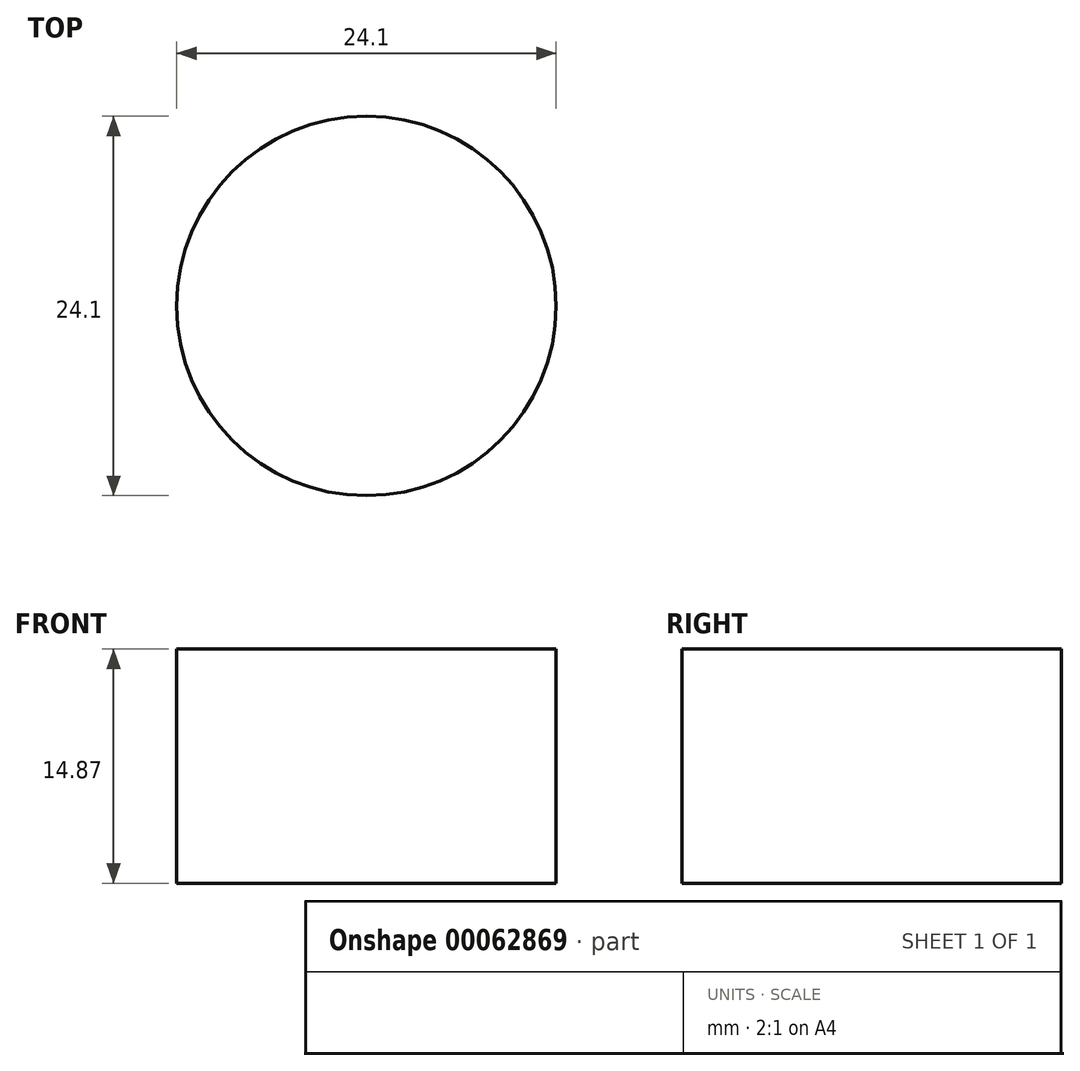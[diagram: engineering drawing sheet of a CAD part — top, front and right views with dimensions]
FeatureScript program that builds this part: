
annotation { "Feature Type Name" : "Feature", "Feature Type Description" : "" }
export const myFeature = defineFeature(function(context is Context, id is Id, definition is map)
    precondition{}
    {
        {
            var Q0;
            Q0=qCreatedBy(makeId("Front.planeOp"),FACE);
            var sketch = newSketch(context, id + "F0", { "sketchPlane" : qUnion([Q0])});
            skLineSegment(sketch, "E0", {"start": v(0, 16.36) * mm, "end": v(0, -28.8) * mm});
            skLineSegment(sketch, "E1", {"start": v(0, 16.36) * mm, "end": v(15.92, 16.36) * mm});
            skLineSegment(sketch, "E2", {"start": v(15.92, 16.36) * mm, "end": v(15.92, -28.8) * mm});
            skLineSegment(sketch, "E3", {"start": v(15.92, -28.8) * mm, "end": v(0, -28.8) * mm});
            skLineSegment(sketch, "E4", {"start": v(0, -28.8) * mm, "end": v(12.05, -28.8) * mm});
            skLineSegment(sketch, "E5", {"start": v(15.92, 16.36) * mm, "end": v(12.05, 16.36) * mm});
            skLineSegment(sketch, "E6", {"start": v(15.92, 16.36) * mm, "end": v(15.92, 12.22) * mm});
            skPoint(sketch, "E7", {"position": v(13.99, 16.36) * mm});
            skPoint(sketch, "E8", {"position": v(15.92, 14.29) * mm});
            skPoint(sketch, "E9", {"position": v(-63.86, 47.5) * mm});
            skLineSegment(sketch, "E10", {"start": v(12.05, 16.36) * mm, "end": v(12.05, -28.8) * mm});
            skLineSegment(sketch, "E11", {"start": v(15.92, -28.8) * mm, "end": v(15.92, -18.05) * mm});
            skLineSegment(sketch, "E12", {"start": v(15.92, -28.8) * mm, "end": v(15.92, -13.8) * mm});
            skLineSegment(sketch, "E13", {"start": v(15.92, -13.8) * mm, "end": v(15.92, -18.55) * mm});
            skLineSegment(sketch, "E14", {"start": v(15.92, -13.8) * mm, "end": v(15.42, -13.8) * mm});
            skLineSegment(sketch, "E15", {"start": v(15.42, -13.8) * mm, "end": v(15.42, -18.55) * mm});
            skLineSegment(sketch, "E16", {"start": v(15.42, -18.55) * mm, "end": v(15.92, -18.55) * mm});
            skLineSegment(sketch, "E17", {"start": v(0, -13.93) * mm, "end": v(8.68, -13.93) * mm});
            skLineSegment(sketch, "E18", {"start": v(8.68, -13.93) * mm, "end": v(12.05, -13.93) * mm});
            skLineSegment(sketch, "E19", {"start": v(8.68, -13.93) * mm, "end": v(8.68, -28.8) * mm});
            skFitSpline(sketch, "E20", {"points": [v(12.05, 16.36) * mm, v(14.39, 15.38) * mm, v(15.92, 12.9) * mm], "startDerivative": vector(3.11, 0) * mm, "endDerivative": vector(0, -5.55) * mm});
            skSolve(sketch);
        }
        {
            var Q0;
            {var subQ0=sQuery(id+"F0.wireOp",EDGE,"d632429b-8b9d-4d76-a169-94f976e06c24");var subQ1=sQuery(id+"F0.wireOp",EDGE,"9AcJyGnw-STYi-GIwg-dRD0-rNDVPBwUBnKr");var subQ2=makeQuery(id+"F0.imprint","INTERSECT",VERTEX,{"disambiguationData":[OD(0.0)],"derivedFrom":[subQ1,subQ0]});Q0=makeQuery(id+"F0.imprint","IMPRINT",FACE,{"disambiguationData":[TD([[makeQuery(id+"F0.imprint","IMPRINT",EDGE,{"disambiguationData":[TD([[subQ2,-1.0]])],"derivedFrom":subQ1}),1.0]])]});}
            var Q1;
            {var subQ1=sQuery(id+"F0.wireOp",EDGE,"E6");var subQ3=sQuery(id+"F0.wireOp",EDGE,"d632429b-8b9d-4d76-a169-94f976e06c24");var subQ4=makeQuery(id+"F0.imprint","INTERSECT",VERTEX,{"derivedFrom":[subQ1,subQ3]});Q1=makeQuery(id+"F0.imprint","IMPRINT",FACE,{"disambiguationData":[TD([[makeQuery(id+"F0.imprint","IMPRINT",EDGE,{"disambiguationData":[TD([[subQ4,1.0]])],"derivedFrom":subQ3}),-1.0]])]});}
            var Q2;
            {var subQ1=sQuery(id+"F0.wireOp",EDGE,"E5");var subQ3=sQuery(id+"F0.wireOp",EDGE,"d632429b-8b9d-4d76-a169-94f976e06c24");var subQ4=makeQuery(id+"F0.imprint","INTERSECT",VERTEX,{"derivedFrom":[subQ1,subQ3]});Q2=makeQuery(id+"F0.imprint","IMPRINT",FACE,{"disambiguationData":[TD([[makeQuery(id+"F0.imprint","IMPRINT",EDGE,{"disambiguationData":[TD([[subQ4,-1.0]])],"derivedFrom":subQ3}),-1.0]])]});}
            var Q3;
            {var subQ1=sQuery(id+"F0.wireOp",EDGE,"9AcJyGnw-STYi-GIwg-dRD0-rNDVPBwUBnKr");var subQ3=sQuery(id+"F0.wireOp",EDGE,"d632429b-8b9d-4d76-a169-94f976e06c24");var subQ4=makeQuery(id+"F0.imprint","INTERSECT",VERTEX,{"disambiguationData":[OD(0.0)],"derivedFrom":[subQ1,subQ3]});Q3=makeQuery(id+"F0.imprint","IMPRINT",FACE,{"disambiguationData":[TD([[makeQuery(id+"F0.imprint","IMPRINT",EDGE,{"disambiguationData":[TD([[subQ4,-1.0]])],"derivedFrom":subQ3}),-1.0]])]});}
            var Q4;
            {var subQ4=sQuery(id+"F0.wireOp",EDGE,"E18");Q4=makeQuery(id+"F0.imprint","IMPRINT",FACE,{"disambiguationData":[TD([[makeQuery(id+"F0.imprint","IMPRINT",EDGE,{"derivedFrom":subQ4}),-1.0]])]});}
            var Q5;
            {var subQ1=sQuery(id+"F0.wireOp",EDGE,"E3");Q5=makeQuery(id+"F0.imprint","IMPRINT",FACE,{"disambiguationData":[TD([[makeQuery(id+"F0.imprint","IMPRINT",EDGE,{"derivedFrom":subQ1}),-1.0]])]});}
            var Q6;
            Q6=sQuery(id+"F0.wireOp",EDGE,"E0");
            revolve(context, id + "F1", {"entities" : qUnion([Q0, Q1, Q2, Q3, Q4, Q5]), "axis" : qUnion([Q6]), "revolveType" : RevolveType.FULL});
        }
        {
            var Q0;
            Q0=qCreatedBy(makeId("Front.planeOp"),FACE);
            var sketch = newSketch(context, id + "F2", { "sketchPlane" : qUnion([Q0])});
            skCircle(sketch, "E21", {"center": v(18.2, -22.31) * mm, "radius": 3 * mm});
            skLineSegment(sketch, "E22", {"start": v(18.2, -22.31) * mm, "end": v(18.2, -40.74) * mm});
            skLineSegment(sketch, "E23", {"start": v(21.2, -22.31) * mm, "end": v(18.2, -22.31) * mm});
            skLineSegment(sketch, "E24", {"start": v(18.2, -40.74) * mm, "end": v(21.2, -40.74) * mm});
            skLineSegment(sketch, "E25", {"start": v(21.2, -22.31) * mm, "end": v(21.2, -40.74) * mm});
            skLineSegment(sketch, "E26", {"start": v(18.2, -22.31) * mm, "end": v(18.2, -19.31) * mm});
            skSolve(sketch);
        }
        {
            var Q0;
            {var subQ0=sQuery(id+"F2.wireOp",EDGE,"E23");Q0=makeQuery(id+"F2.imprint","IMPRINT",FACE,{"disambiguationData":[TD([[makeQuery(id+"F2.imprint","IMPRINT",EDGE,{"derivedFrom":subQ0}),-1.0]])]});}
            var Q1;
            {var subQ0=sQuery(id+"F2.wireOp",EDGE,"E23");Q1=makeQuery(id+"F2.imprint","IMPRINT",FACE,{"disambiguationData":[TD([[makeQuery(id+"F2.imprint","IMPRINT",EDGE,{"derivedFrom":subQ0}),1.0]])]});}
            var Q2;
            {var subQ4=sQuery(id+"F2.wireOp",EDGE,"E24");Q2=makeQuery(id+"F2.imprint","IMPRINT",FACE,{"disambiguationData":[TD([[makeQuery(id+"F2.imprint","IMPRINT",EDGE,{"derivedFrom":subQ4}),1.0]])]});}
            var Q3;
            Q3=sQuery(id+"F2.wireOp",EDGE,"E22");
            revolve(context, id + "F3", {"entities" : qUnion([Q0, Q1, Q2]), "axis" : qUnion([Q3]), "revolveType" : RevolveType.FULL});
        }
        {
            var Q0;
            Q0=qCreatedBy(makeId("Front.planeOp"),FACE);
            var sketch = newSketch(context, id + "F4", { "sketchPlane" : qUnion([Q0])});
            skLineSegment(sketch, "E27.bottom", {"start": v(0, 43.24) * mm, "end": v(-13.77, 43.24) * mm});
            skLineSegment(sketch, "E27.top", {"start": v(0, 31.16) * mm, "end": v(-13.77, 31.16) * mm});
            skLineSegment(sketch, "E27.left", {"start": v(0, 43.24) * mm, "end": v(0, 31.16) * mm});
            skLineSegment(sketch, "E27.right", {"start": v(-13.77, 43.24) * mm, "end": v(-13.77, 31.16) * mm});
            skSolve(sketch);
        }
        {
            var Q0;
            Q0=qSketchRegion(id+"F4",true);
            extrude(context, id + "F5", {"entities" : qUnion([Q0]), "depth" : 25 * mm});
        }
        {
            var Q0;
            Q0=makeQuery(id+"F3.opRevolve","SWEPT_BODY",BODY,{"disambiguationData":[OSD([sQuery(id+"F2.wireOp",EDGE,"E21"),sQuery(id+"F2.wireOp",EDGE,"E22"),sQuery(id+"F2.wireOp",EDGE,"E24"),sQuery(id+"F2.wireOp",EDGE,"E25"),sQuery(id+"F2.wireOp",EDGE,"E26")])]});
            var Q1;
            Q1=makeQuery(id+"F5.opExtrude","CAP_EDGE",EDGE,{"disambiguationData":[OSD([sQuery(id+"F4.wireOp",EDGE,"E27.left")])],"isStart":true});
            transform(context, id + "F6", {"entities" : qUnion([Q0]), "transformType" : TransformType.ROTATION, "transformAxis" : qUnion([Q1]), "angle" : 22.5 * degree, "makeCopy" : true});
        }
        {
            var Q0;
            Q0=makeQuery(id+"F6.opPattern","COPY",BODY,{"derivedFrom":makeQuery(id+"F3.opRevolve","SWEPT_BODY",BODY,{"disambiguationData":[OSD([sQuery(id+"F2.wireOp",EDGE,"E21"),sQuery(id+"F2.wireOp",EDGE,"E22"),sQuery(id+"F2.wireOp",EDGE,"E24"),sQuery(id+"F2.wireOp",EDGE,"E25"),sQuery(id+"F2.wireOp",EDGE,"E26")])]}),"instanceName":"1"});
            var Q1;
            Q1=makeQuery(id+"F3.opRevolve","SWEPT_BODY",BODY,{"disambiguationData":[OSD([sQuery(id+"F2.wireOp",EDGE,"E21"),sQuery(id+"F2.wireOp",EDGE,"E22"),sQuery(id+"F2.wireOp",EDGE,"E24"),sQuery(id+"F2.wireOp",EDGE,"E25"),sQuery(id+"F2.wireOp",EDGE,"E26")])]});
            var Q2;
            Q2=makeQuery(id+"F5.opExtrude","CAP_EDGE",EDGE,{"disambiguationData":[OSD([sQuery(id+"F4.wireOp",EDGE,"E27.left")])],"isStart":true});
            transform(context, id + "F7", {"entities" : qUnion([Q0, Q1]), "transformType" : TransformType.ROTATION, "transformAxis" : qUnion([Q2]), "angle" : 45 * degree, "makeCopy" : true});
        }
        {
            var Q0;
            Q0=makeQuery(id+"F3.opRevolve","SWEPT_BODY",BODY,{"disambiguationData":[OSD([sQuery(id+"F2.wireOp",EDGE,"E21"),sQuery(id+"F2.wireOp",EDGE,"E22"),sQuery(id+"F2.wireOp",EDGE,"E24"),sQuery(id+"F2.wireOp",EDGE,"E25"),sQuery(id+"F2.wireOp",EDGE,"E26")])]});
            var Q1;
            Q1=makeQuery(id+"F6.opPattern","COPY",BODY,{"derivedFrom":makeQuery(id+"F3.opRevolve","SWEPT_BODY",BODY,{"disambiguationData":[OSD([sQuery(id+"F2.wireOp",EDGE,"E21"),sQuery(id+"F2.wireOp",EDGE,"E22"),sQuery(id+"F2.wireOp",EDGE,"E24"),sQuery(id+"F2.wireOp",EDGE,"E25"),sQuery(id+"F2.wireOp",EDGE,"E26")])]}),"instanceName":"1"});
            var Q2;
            Q2=makeQuery(id+"F7.opPattern","COPY",BODY,{"derivedFrom":makeQuery(id+"F3.opRevolve","SWEPT_BODY",BODY,{"disambiguationData":[OSD([sQuery(id+"F2.wireOp",EDGE,"E21"),sQuery(id+"F2.wireOp",EDGE,"E22"),sQuery(id+"F2.wireOp",EDGE,"E24"),sQuery(id+"F2.wireOp",EDGE,"E25"),sQuery(id+"F2.wireOp",EDGE,"E26")])]}),"instanceName":"1"});
            var Q3;
            Q3=makeQuery(id+"F7.opPattern","COPY",BODY,{"derivedFrom":makeQuery(id+"F6.opPattern","COPY",BODY,{"derivedFrom":makeQuery(id+"F3.opRevolve","SWEPT_BODY",BODY,{"disambiguationData":[OSD([sQuery(id+"F2.wireOp",EDGE,"E21"),sQuery(id+"F2.wireOp",EDGE,"E22"),sQuery(id+"F2.wireOp",EDGE,"E24"),sQuery(id+"F2.wireOp",EDGE,"E25"),sQuery(id+"F2.wireOp",EDGE,"E26")])]}),"instanceName":"1"}),"instanceName":"1"});
            var Q4;
            Q4=makeQuery(id+"F5.opExtrude","CAP_EDGE",EDGE,{"disambiguationData":[OSD([sQuery(id+"F4.wireOp",EDGE,"E27.left")])],"isStart":true});
            transform(context, id + "F8", {"entities" : qUnion([Q0, Q1, Q2, Q3]), "transformType" : TransformType.ROTATION, "transformAxis" : qUnion([Q4]), "angle" : 90 * degree, "makeCopy" : true});
        }
        {
            var Q0;
            Q0=makeQuery(id+"F3.opRevolve","SWEPT_BODY",BODY,{"disambiguationData":[OSD([sQuery(id+"F2.wireOp",EDGE,"E21"),sQuery(id+"F2.wireOp",EDGE,"E22"),sQuery(id+"F2.wireOp",EDGE,"E24"),sQuery(id+"F2.wireOp",EDGE,"E25"),sQuery(id+"F2.wireOp",EDGE,"E26")])]});
            var Q1;
            Q1=makeQuery(id+"F6.opPattern","COPY",BODY,{"derivedFrom":makeQuery(id+"F3.opRevolve","SWEPT_BODY",BODY,{"disambiguationData":[OSD([sQuery(id+"F2.wireOp",EDGE,"E21"),sQuery(id+"F2.wireOp",EDGE,"E22"),sQuery(id+"F2.wireOp",EDGE,"E24"),sQuery(id+"F2.wireOp",EDGE,"E25"),sQuery(id+"F2.wireOp",EDGE,"E26")])]}),"instanceName":"1"});
            var Q2;
            Q2=makeQuery(id+"F7.opPattern","COPY",BODY,{"derivedFrom":makeQuery(id+"F3.opRevolve","SWEPT_BODY",BODY,{"disambiguationData":[OSD([sQuery(id+"F2.wireOp",EDGE,"E21"),sQuery(id+"F2.wireOp",EDGE,"E22"),sQuery(id+"F2.wireOp",EDGE,"E24"),sQuery(id+"F2.wireOp",EDGE,"E25"),sQuery(id+"F2.wireOp",EDGE,"E26")])]}),"instanceName":"1"});
            var Q3;
            Q3=makeQuery(id+"F7.opPattern","COPY",BODY,{"derivedFrom":makeQuery(id+"F6.opPattern","COPY",BODY,{"derivedFrom":makeQuery(id+"F3.opRevolve","SWEPT_BODY",BODY,{"disambiguationData":[OSD([sQuery(id+"F2.wireOp",EDGE,"E21"),sQuery(id+"F2.wireOp",EDGE,"E22"),sQuery(id+"F2.wireOp",EDGE,"E24"),sQuery(id+"F2.wireOp",EDGE,"E25"),sQuery(id+"F2.wireOp",EDGE,"E26")])]}),"instanceName":"1"}),"instanceName":"1"});
            var Q4;
            Q4=makeQuery(id+"F8.opPattern","COPY",BODY,{"derivedFrom":makeQuery(id+"F3.opRevolve","SWEPT_BODY",BODY,{"disambiguationData":[OSD([sQuery(id+"F2.wireOp",EDGE,"E21"),sQuery(id+"F2.wireOp",EDGE,"E22"),sQuery(id+"F2.wireOp",EDGE,"E24"),sQuery(id+"F2.wireOp",EDGE,"E25"),sQuery(id+"F2.wireOp",EDGE,"E26")])]}),"instanceName":"1"});
            var Q5;
            Q5=makeQuery(id+"F8.opPattern","COPY",BODY,{"derivedFrom":makeQuery(id+"F6.opPattern","COPY",BODY,{"derivedFrom":makeQuery(id+"F3.opRevolve","SWEPT_BODY",BODY,{"disambiguationData":[OSD([sQuery(id+"F2.wireOp",EDGE,"E21"),sQuery(id+"F2.wireOp",EDGE,"E22"),sQuery(id+"F2.wireOp",EDGE,"E24"),sQuery(id+"F2.wireOp",EDGE,"E25"),sQuery(id+"F2.wireOp",EDGE,"E26")])]}),"instanceName":"1"}),"instanceName":"1"});
            var Q6;
            Q6=makeQuery(id+"F8.opPattern","COPY",BODY,{"derivedFrom":makeQuery(id+"F7.opPattern","COPY",BODY,{"derivedFrom":makeQuery(id+"F3.opRevolve","SWEPT_BODY",BODY,{"disambiguationData":[OSD([sQuery(id+"F2.wireOp",EDGE,"E21"),sQuery(id+"F2.wireOp",EDGE,"E22"),sQuery(id+"F2.wireOp",EDGE,"E24"),sQuery(id+"F2.wireOp",EDGE,"E25"),sQuery(id+"F2.wireOp",EDGE,"E26")])]}),"instanceName":"1"}),"instanceName":"1"});
            var Q7;
            Q7=makeQuery(id+"F8.opPattern","COPY",BODY,{"derivedFrom":makeQuery(id+"F7.opPattern","COPY",BODY,{"derivedFrom":makeQuery(id+"F6.opPattern","COPY",BODY,{"derivedFrom":makeQuery(id+"F3.opRevolve","SWEPT_BODY",BODY,{"disambiguationData":[OSD([sQuery(id+"F2.wireOp",EDGE,"E21"),sQuery(id+"F2.wireOp",EDGE,"E22"),sQuery(id+"F2.wireOp",EDGE,"E24"),sQuery(id+"F2.wireOp",EDGE,"E25"),sQuery(id+"F2.wireOp",EDGE,"E26")])]}),"instanceName":"1"}),"instanceName":"1"}),"instanceName":"1"});
            var Q8;
            Q8=makeQuery(id+"F5.opExtrude","CAP_EDGE",EDGE,{"disambiguationData":[OSD([sQuery(id+"F4.wireOp",EDGE,"E27.left")])],"isStart":true});
            transform(context, id + "F9", {"entities" : qUnion([Q0, Q1, Q2, Q3, Q4, Q5, Q6, Q7]), "transformType" : TransformType.ROTATION, "transformAxis" : qUnion([Q8]), "angle" : 180 * degree, "makeCopy" : true});
        }
        {
            var Q0;
            Q0=makeQuery(id+"F8.opPattern","COPY",BODY,{"derivedFrom":makeQuery(id+"F7.opPattern","COPY",BODY,{"derivedFrom":makeQuery(id+"F6.opPattern","COPY",BODY,{"derivedFrom":makeQuery(id+"F3.opRevolve","SWEPT_BODY",BODY,{"disambiguationData":[OSD([sQuery(id+"F2.wireOp",EDGE,"E21"),sQuery(id+"F2.wireOp",EDGE,"E22"),sQuery(id+"F2.wireOp",EDGE,"E24"),sQuery(id+"F2.wireOp",EDGE,"E25"),sQuery(id+"F2.wireOp",EDGE,"E26")])]}),"instanceName":"1"}),"instanceName":"1"}),"instanceName":"1"});
            var Q1;
            Q1=makeQuery(id+"F9.opPattern","COPY",BODY,{"derivedFrom":makeQuery(id+"F3.opRevolve","SWEPT_BODY",BODY,{"disambiguationData":[OSD([sQuery(id+"F2.wireOp",EDGE,"E21"),sQuery(id+"F2.wireOp",EDGE,"E22"),sQuery(id+"F2.wireOp",EDGE,"E24"),sQuery(id+"F2.wireOp",EDGE,"E25"),sQuery(id+"F2.wireOp",EDGE,"E26")])]}),"instanceName":"1"});
            var Q2;
            Q2=makeQuery(id+"F9.opPattern","COPY",BODY,{"derivedFrom":makeQuery(id+"F6.opPattern","COPY",BODY,{"derivedFrom":makeQuery(id+"F3.opRevolve","SWEPT_BODY",BODY,{"disambiguationData":[OSD([sQuery(id+"F2.wireOp",EDGE,"E21"),sQuery(id+"F2.wireOp",EDGE,"E22"),sQuery(id+"F2.wireOp",EDGE,"E24"),sQuery(id+"F2.wireOp",EDGE,"E25"),sQuery(id+"F2.wireOp",EDGE,"E26")])]}),"instanceName":"1"}),"instanceName":"1"});
            var Q3;
            Q3=makeQuery(id+"F8.opPattern","COPY",BODY,{"derivedFrom":makeQuery(id+"F6.opPattern","COPY",BODY,{"derivedFrom":makeQuery(id+"F3.opRevolve","SWEPT_BODY",BODY,{"disambiguationData":[OSD([sQuery(id+"F2.wireOp",EDGE,"E21"),sQuery(id+"F2.wireOp",EDGE,"E22"),sQuery(id+"F2.wireOp",EDGE,"E24"),sQuery(id+"F2.wireOp",EDGE,"E25"),sQuery(id+"F2.wireOp",EDGE,"E26")])]}),"instanceName":"1"}),"instanceName":"1"});
            var Q4;
            Q4=makeQuery(id+"F8.opPattern","COPY",BODY,{"derivedFrom":makeQuery(id+"F7.opPattern","COPY",BODY,{"derivedFrom":makeQuery(id+"F3.opRevolve","SWEPT_BODY",BODY,{"disambiguationData":[OSD([sQuery(id+"F2.wireOp",EDGE,"E21"),sQuery(id+"F2.wireOp",EDGE,"E22"),sQuery(id+"F2.wireOp",EDGE,"E24"),sQuery(id+"F2.wireOp",EDGE,"E25"),sQuery(id+"F2.wireOp",EDGE,"E26")])]}),"instanceName":"1"}),"instanceName":"1"});
            var Q5;
            Q5=makeQuery(id+"F8.opPattern","COPY",BODY,{"derivedFrom":makeQuery(id+"F3.opRevolve","SWEPT_BODY",BODY,{"disambiguationData":[OSD([sQuery(id+"F2.wireOp",EDGE,"E21"),sQuery(id+"F2.wireOp",EDGE,"E22"),sQuery(id+"F2.wireOp",EDGE,"E24"),sQuery(id+"F2.wireOp",EDGE,"E25"),sQuery(id+"F2.wireOp",EDGE,"E26")])]}),"instanceName":"1"});
            var Q6;
            Q6=makeQuery(id+"F7.opPattern","COPY",BODY,{"derivedFrom":makeQuery(id+"F6.opPattern","COPY",BODY,{"derivedFrom":makeQuery(id+"F3.opRevolve","SWEPT_BODY",BODY,{"disambiguationData":[OSD([sQuery(id+"F2.wireOp",EDGE,"E21"),sQuery(id+"F2.wireOp",EDGE,"E22"),sQuery(id+"F2.wireOp",EDGE,"E24"),sQuery(id+"F2.wireOp",EDGE,"E25"),sQuery(id+"F2.wireOp",EDGE,"E26")])]}),"instanceName":"1"}),"instanceName":"1"});
            var Q7;
            Q7=makeQuery(id+"F7.opPattern","COPY",BODY,{"derivedFrom":makeQuery(id+"F3.opRevolve","SWEPT_BODY",BODY,{"disambiguationData":[OSD([sQuery(id+"F2.wireOp",EDGE,"E21"),sQuery(id+"F2.wireOp",EDGE,"E22"),sQuery(id+"F2.wireOp",EDGE,"E24"),sQuery(id+"F2.wireOp",EDGE,"E25"),sQuery(id+"F2.wireOp",EDGE,"E26")])]}),"instanceName":"1"});
            var Q8;
            Q8=makeQuery(id+"F6.opPattern","COPY",BODY,{"derivedFrom":makeQuery(id+"F3.opRevolve","SWEPT_BODY",BODY,{"disambiguationData":[OSD([sQuery(id+"F2.wireOp",EDGE,"E21"),sQuery(id+"F2.wireOp",EDGE,"E22"),sQuery(id+"F2.wireOp",EDGE,"E24"),sQuery(id+"F2.wireOp",EDGE,"E25"),sQuery(id+"F2.wireOp",EDGE,"E26")])]}),"instanceName":"1"});
            var Q9;
            Q9=makeQuery(id+"F3.opRevolve","SWEPT_BODY",BODY,{"disambiguationData":[OSD([sQuery(id+"F2.wireOp",EDGE,"E21"),sQuery(id+"F2.wireOp",EDGE,"E22"),sQuery(id+"F2.wireOp",EDGE,"E24"),sQuery(id+"F2.wireOp",EDGE,"E25"),sQuery(id+"F2.wireOp",EDGE,"E26")])]});
            var Q10;
            Q10=makeQuery(id+"F9.opPattern","COPY",BODY,{"derivedFrom":makeQuery(id+"F8.opPattern","COPY",BODY,{"derivedFrom":makeQuery(id+"F7.opPattern","COPY",BODY,{"derivedFrom":makeQuery(id+"F6.opPattern","COPY",BODY,{"derivedFrom":makeQuery(id+"F3.opRevolve","SWEPT_BODY",BODY,{"disambiguationData":[OSD([sQuery(id+"F2.wireOp",EDGE,"E21"),sQuery(id+"F2.wireOp",EDGE,"E22"),sQuery(id+"F2.wireOp",EDGE,"E24"),sQuery(id+"F2.wireOp",EDGE,"E25"),sQuery(id+"F2.wireOp",EDGE,"E26")])]}),"instanceName":"1"}),"instanceName":"1"}),"instanceName":"1"}),"instanceName":"1"});
            var Q11;
            Q11=makeQuery(id+"F9.opPattern","COPY",BODY,{"derivedFrom":makeQuery(id+"F8.opPattern","COPY",BODY,{"derivedFrom":makeQuery(id+"F7.opPattern","COPY",BODY,{"derivedFrom":makeQuery(id+"F3.opRevolve","SWEPT_BODY",BODY,{"disambiguationData":[OSD([sQuery(id+"F2.wireOp",EDGE,"E21"),sQuery(id+"F2.wireOp",EDGE,"E22"),sQuery(id+"F2.wireOp",EDGE,"E24"),sQuery(id+"F2.wireOp",EDGE,"E25"),sQuery(id+"F2.wireOp",EDGE,"E26")])]}),"instanceName":"1"}),"instanceName":"1"}),"instanceName":"1"});
            var Q12;
            Q12=makeQuery(id+"F9.opPattern","COPY",BODY,{"derivedFrom":makeQuery(id+"F8.opPattern","COPY",BODY,{"derivedFrom":makeQuery(id+"F6.opPattern","COPY",BODY,{"derivedFrom":makeQuery(id+"F3.opRevolve","SWEPT_BODY",BODY,{"disambiguationData":[OSD([sQuery(id+"F2.wireOp",EDGE,"E21"),sQuery(id+"F2.wireOp",EDGE,"E22"),sQuery(id+"F2.wireOp",EDGE,"E24"),sQuery(id+"F2.wireOp",EDGE,"E25"),sQuery(id+"F2.wireOp",EDGE,"E26")])]}),"instanceName":"1"}),"instanceName":"1"}),"instanceName":"1"});
            var Q13;
            Q13=makeQuery(id+"F9.opPattern","COPY",BODY,{"derivedFrom":makeQuery(id+"F8.opPattern","COPY",BODY,{"derivedFrom":makeQuery(id+"F3.opRevolve","SWEPT_BODY",BODY,{"disambiguationData":[OSD([sQuery(id+"F2.wireOp",EDGE,"E21"),sQuery(id+"F2.wireOp",EDGE,"E22"),sQuery(id+"F2.wireOp",EDGE,"E24"),sQuery(id+"F2.wireOp",EDGE,"E25"),sQuery(id+"F2.wireOp",EDGE,"E26")])]}),"instanceName":"1"}),"instanceName":"1"});
            var Q14;
            Q14=makeQuery(id+"F9.opPattern","COPY",BODY,{"derivedFrom":makeQuery(id+"F7.opPattern","COPY",BODY,{"derivedFrom":makeQuery(id+"F6.opPattern","COPY",BODY,{"derivedFrom":makeQuery(id+"F3.opRevolve","SWEPT_BODY",BODY,{"disambiguationData":[OSD([sQuery(id+"F2.wireOp",EDGE,"E21"),sQuery(id+"F2.wireOp",EDGE,"E22"),sQuery(id+"F2.wireOp",EDGE,"E24"),sQuery(id+"F2.wireOp",EDGE,"E25"),sQuery(id+"F2.wireOp",EDGE,"E26")])]}),"instanceName":"1"}),"instanceName":"1"}),"instanceName":"1"});
            var Q15;
            Q15=makeQuery(id+"F9.opPattern","COPY",BODY,{"derivedFrom":makeQuery(id+"F7.opPattern","COPY",BODY,{"derivedFrom":makeQuery(id+"F3.opRevolve","SWEPT_BODY",BODY,{"disambiguationData":[OSD([sQuery(id+"F2.wireOp",EDGE,"E21"),sQuery(id+"F2.wireOp",EDGE,"E22"),sQuery(id+"F2.wireOp",EDGE,"E24"),sQuery(id+"F2.wireOp",EDGE,"E25"),sQuery(id+"F2.wireOp",EDGE,"E26")])]}),"instanceName":"1"}),"instanceName":"1"});
            var Q16;
            Q16=makeQuery(id+"F1.opRevolve","SWEPT_BODY",BODY,{"disambiguationData":[OSD([sQuery(id+"F0.wireOp",EDGE,"E2"),sQuery(id+"F0.wireOp",EDGE,"E3"),sQuery(id+"F0.wireOp",EDGE,"E5"),sQuery(id+"F0.wireOp",EDGE,"E6"),sQuery(id+"F0.wireOp",EDGE,"d632429b-8b9d-4d76-a169-94f976e06c24"),sQuery(id+"F0.wireOp",EDGE,"E10"),sQuery(id+"F0.wireOp",EDGE,"E11"),sQuery(id+"F0.wireOp",EDGE,"mPbeVBwt-LSE7-foui-vcjy-5yCH7zzkyHPw"),sQuery(id+"F0.wireOp",EDGE,"A7bMU6j7-EvYy-TxjT-9eZQ-hZ58iMjyQqAi"),sQuery(id+"F0.wireOp",EDGE,"rTNWqyM8-7bZb-OHbZ-suaX-VuzeamaOtf12")])]});
            booleanBodies(context, id + "F10", {"operationType" : BooleanOperationType.SUBTRACTION, "tools" : qUnion([Q0, Q1, Q2, Q3, Q4, Q5, Q6, Q7, Q8, Q9, Q10, Q11, Q12, Q13, Q14, Q15]), "targets" : qUnion([Q16])});
        }
        {
            var Q0;
            Q0=qCreatedBy(makeId("Front.planeOp"),FACE);
            var sketch = newSketch(context, id + "F11", { "sketchPlane" : qUnion([Q0])});
            skLineSegment(sketch, "E28", {"start": v(0, 31.16) * mm, "end": v(0, -45.64) * mm});
            skCircle(sketch, "E29", {"center": v(0, 5.07) * mm, "radius": 2.11 * mm});
            skSolve(sketch);
        }
        {
            var Q0;
            {var subQ0=sQuery(id+"F11.wireOp",EDGE,"E29");var subQ1=sQuery(id+"F11.wireOp",EDGE,"E28");var subQ2=makeQuery(id+"F11.imprint","INTERSECT",VERTEX,{"disambiguationData":[OD(0.0)],"derivedFrom":[subQ1,subQ0]});Q0=makeQuery(id+"F11.imprint","IMPRINT",FACE,{"disambiguationData":[TD([[makeQuery(id+"F11.imprint","IMPRINT",EDGE,{"disambiguationData":[TD([[subQ2,1.0]])],"derivedFrom":subQ1}),1.0]])]});}
            var Q1;
            {var subQ0=sQuery(id+"F11.wireOp",EDGE,"E29");var subQ1=sQuery(id+"F11.wireOp",EDGE,"E28");var subQ2=makeQuery(id+"F11.imprint","INTERSECT",VERTEX,{"disambiguationData":[OD(0.0)],"derivedFrom":[subQ1,subQ0]});Q1=makeQuery(id+"F11.imprint","IMPRINT",FACE,{"disambiguationData":[TD([[makeQuery(id+"F11.imprint","IMPRINT",EDGE,{"disambiguationData":[TD([[subQ2,1.0]])],"derivedFrom":subQ1}),-1.0]])]});}
            extrude(context, id + "F12", {"entities" : qUnion([Q0, Q1]), "operationType" : NewBodyOperationType.REMOVE, "endBound" : BoundingType.SYMMETRIC, "oppositeDirection" : true, "depth" : 45 * mm});
        }
        {
            var Q0;
            Q0=qCreatedBy(makeId("Top.planeOp"),FACE);
            var sketch = newSketch(context, id + "F13", { "sketchPlane" : qUnion([Q0])});
            skCircle(sketch, "E30", {"center": v(0, 0) * mm, "radius": 15.72 * mm});
            skLineSegment(sketch, "E31.rect.bottom", {"start": v(0.25, 15.97) * mm, "end": v(-0.25, 15.97) * mm});
            skLineSegment(sketch, "E31.rect.top", {"start": v(0.25, 15.47) * mm, "end": v(-0.25, 15.47) * mm});
            skLineSegment(sketch, "E31.rect.left", {"start": v(0.25, 15.97) * mm, "end": v(0.25, 15.47) * mm});
            skLineSegment(sketch, "E31.rect.right", {"start": v(-0.25, 15.97) * mm, "end": v(-0.25, 15.47) * mm});
            skPoint(sketch, "E31.rect.middle", {"position": v(0, 15.72) * mm});
            skSolve(sketch);
        }
        {
            var Q0;
            {var subQ5=sQuery(id+"F13.wireOp",EDGE,"E31.rect.bottom");Q0=makeQuery(id+"F13.imprint","IMPRINT",FACE,{"disambiguationData":[TD([[makeQuery(id+"F13.imprint","IMPRINT",EDGE,{"derivedFrom":subQ5}),1.0]])]});}
            var Q1;
            {var subQ5=sQuery(id+"F13.wireOp",EDGE,"E31.rect.top");Q1=makeQuery(id+"F13.imprint","IMPRINT",FACE,{"disambiguationData":[TD([[makeQuery(id+"F13.imprint","IMPRINT",EDGE,{"derivedFrom":subQ5}),-1.0]])]});}
            extrude(context, id + "F14", {"entities" : qUnion([Q0, Q1]), "depth" : 26.8 * mm});
        }
        {
            var Q0;
            Q0=makeQuery(id+"F14.opExtrude","SWEPT_BODY",BODY,{"disambiguationData":[OSD([sQuery(id+"F13.wireOp",EDGE,"E31.rect.bottom"),sQuery(id+"F13.wireOp",EDGE,"E31.rect.top"),sQuery(id+"F13.wireOp",EDGE,"E31.rect.left"),sQuery(id+"F13.wireOp",EDGE,"E31.rect.right")])]});
            transform(context, id + "F15", {"entities" : qUnion([Q0]), "transformType" : TransformType.TRANSLATION_3D, "dx" : 0 * mm, "dy" : 0 * mm, "dz" : -13.9 * mm, "makeCopy" : false});
        }
        {
            var Q0;
            Q0=makeQuery(id+"F14.opExtrude","SWEPT_BODY",BODY,{"disambiguationData":[OSD([sQuery(id+"F13.wireOp",EDGE,"E31.rect.bottom"),sQuery(id+"F13.wireOp",EDGE,"E31.rect.top"),sQuery(id+"F13.wireOp",EDGE,"E31.rect.left"),sQuery(id+"F13.wireOp",EDGE,"E31.rect.right")])]});
            var Q1;
            Q1=makeQuery(id+"F5.opExtrude","CAP_EDGE",EDGE,{"disambiguationData":[OSD([sQuery(id+"F4.wireOp",EDGE,"E27.left")])],"isStart":true});
            transform(context, id + "F16", {"entities" : qUnion([Q0]), "transformType" : TransformType.ROTATION, "transformAxis" : qUnion([Q1]), "angle" : 3.6 * degree, "makeCopy" : true});
        }
        {
            var Q0;
            Q0=makeQuery(id+"F16.opPattern","COPY",BODY,{"derivedFrom":makeQuery(id+"F14.opExtrude","SWEPT_BODY",BODY,{"disambiguationData":[OSD([sQuery(id+"F13.wireOp",EDGE,"E31.rect.bottom"),sQuery(id+"F13.wireOp",EDGE,"E31.rect.top"),sQuery(id+"F13.wireOp",EDGE,"E31.rect.left"),sQuery(id+"F13.wireOp",EDGE,"E31.rect.right")])]}),"instanceName":"1"});
            var Q1;
            Q1=makeQuery(id+"F14.opExtrude","SWEPT_BODY",BODY,{"disambiguationData":[OSD([sQuery(id+"F13.wireOp",EDGE,"E31.rect.bottom"),sQuery(id+"F13.wireOp",EDGE,"E31.rect.top"),sQuery(id+"F13.wireOp",EDGE,"E31.rect.left"),sQuery(id+"F13.wireOp",EDGE,"E31.rect.right")])]});
            var Q2;
            Q2=makeQuery(id+"F5.opExtrude","CAP_EDGE",EDGE,{"disambiguationData":[OSD([sQuery(id+"F4.wireOp",EDGE,"E27.left")])],"isStart":true});
            transform(context, id + "F17", {"entities" : qUnion([Q0, Q1]), "transformType" : TransformType.ROTATION, "transformAxis" : qUnion([Q2]), "angle" : 7.2 * degree, "makeCopy" : true});
        }
        {
            var Q0;
            Q0=makeQuery(id+"F17.opPattern","COPY",BODY,{"derivedFrom":makeQuery(id+"F16.opPattern","COPY",BODY,{"derivedFrom":makeQuery(id+"F14.opExtrude","SWEPT_BODY",BODY,{"disambiguationData":[OSD([sQuery(id+"F13.wireOp",EDGE,"E31.rect.bottom"),sQuery(id+"F13.wireOp",EDGE,"E31.rect.top"),sQuery(id+"F13.wireOp",EDGE,"E31.rect.left"),sQuery(id+"F13.wireOp",EDGE,"E31.rect.right")])]}),"instanceName":"1"}),"instanceName":"1"});
            var Q1;
            Q1=makeQuery(id+"F17.opPattern","COPY",BODY,{"derivedFrom":makeQuery(id+"F14.opExtrude","SWEPT_BODY",BODY,{"disambiguationData":[OSD([sQuery(id+"F13.wireOp",EDGE,"E31.rect.bottom"),sQuery(id+"F13.wireOp",EDGE,"E31.rect.top"),sQuery(id+"F13.wireOp",EDGE,"E31.rect.left"),sQuery(id+"F13.wireOp",EDGE,"E31.rect.right")])]}),"instanceName":"1"});
            var Q2;
            Q2=makeQuery(id+"F16.opPattern","COPY",BODY,{"derivedFrom":makeQuery(id+"F14.opExtrude","SWEPT_BODY",BODY,{"disambiguationData":[OSD([sQuery(id+"F13.wireOp",EDGE,"E31.rect.bottom"),sQuery(id+"F13.wireOp",EDGE,"E31.rect.top"),sQuery(id+"F13.wireOp",EDGE,"E31.rect.left"),sQuery(id+"F13.wireOp",EDGE,"E31.rect.right")])]}),"instanceName":"1"});
            var Q3;
            Q3=makeQuery(id+"F14.opExtrude","SWEPT_BODY",BODY,{"disambiguationData":[OSD([sQuery(id+"F13.wireOp",EDGE,"E31.rect.bottom"),sQuery(id+"F13.wireOp",EDGE,"E31.rect.top"),sQuery(id+"F13.wireOp",EDGE,"E31.rect.left"),sQuery(id+"F13.wireOp",EDGE,"E31.rect.right")])]});
            var Q4;
            Q4=makeQuery(id+"F5.opExtrude","CAP_EDGE",EDGE,{"disambiguationData":[OSD([sQuery(id+"F4.wireOp",EDGE,"E27.left")])],"isStart":true});
            transform(context, id + "F18", {"entities" : qUnion([Q0, Q1, Q2, Q3]), "transformType" : TransformType.ROTATION, "transformAxis" : qUnion([Q4]), "angle" : 14.4 * degree, "makeCopy" : true});
        }
        {
            var Q0;
            Q0=makeQuery(id+"F18.opPattern","COPY",BODY,{"derivedFrom":makeQuery(id+"F17.opPattern","COPY",BODY,{"derivedFrom":makeQuery(id+"F16.opPattern","COPY",BODY,{"derivedFrom":makeQuery(id+"F14.opExtrude","SWEPT_BODY",BODY,{"disambiguationData":[OSD([sQuery(id+"F13.wireOp",EDGE,"E31.rect.bottom"),sQuery(id+"F13.wireOp",EDGE,"E31.rect.top"),sQuery(id+"F13.wireOp",EDGE,"E31.rect.left"),sQuery(id+"F13.wireOp",EDGE,"E31.rect.right")])]}),"instanceName":"1"}),"instanceName":"1"}),"instanceName":"1"});
            var Q1;
            Q1=makeQuery(id+"F18.opPattern","COPY",BODY,{"derivedFrom":makeQuery(id+"F17.opPattern","COPY",BODY,{"derivedFrom":makeQuery(id+"F14.opExtrude","SWEPT_BODY",BODY,{"disambiguationData":[OSD([sQuery(id+"F13.wireOp",EDGE,"E31.rect.bottom"),sQuery(id+"F13.wireOp",EDGE,"E31.rect.top"),sQuery(id+"F13.wireOp",EDGE,"E31.rect.left"),sQuery(id+"F13.wireOp",EDGE,"E31.rect.right")])]}),"instanceName":"1"}),"instanceName":"1"});
            var Q2;
            Q2=makeQuery(id+"F18.opPattern","COPY",BODY,{"derivedFrom":makeQuery(id+"F16.opPattern","COPY",BODY,{"derivedFrom":makeQuery(id+"F14.opExtrude","SWEPT_BODY",BODY,{"disambiguationData":[OSD([sQuery(id+"F13.wireOp",EDGE,"E31.rect.bottom"),sQuery(id+"F13.wireOp",EDGE,"E31.rect.top"),sQuery(id+"F13.wireOp",EDGE,"E31.rect.left"),sQuery(id+"F13.wireOp",EDGE,"E31.rect.right")])]}),"instanceName":"1"}),"instanceName":"1"});
            var Q3;
            Q3=makeQuery(id+"F18.opPattern","COPY",BODY,{"derivedFrom":makeQuery(id+"F14.opExtrude","SWEPT_BODY",BODY,{"disambiguationData":[OSD([sQuery(id+"F13.wireOp",EDGE,"E31.rect.bottom"),sQuery(id+"F13.wireOp",EDGE,"E31.rect.top"),sQuery(id+"F13.wireOp",EDGE,"E31.rect.left"),sQuery(id+"F13.wireOp",EDGE,"E31.rect.right")])]}),"instanceName":"1"});
            var Q4;
            Q4=makeQuery(id+"F17.opPattern","COPY",BODY,{"derivedFrom":makeQuery(id+"F16.opPattern","COPY",BODY,{"derivedFrom":makeQuery(id+"F14.opExtrude","SWEPT_BODY",BODY,{"disambiguationData":[OSD([sQuery(id+"F13.wireOp",EDGE,"E31.rect.bottom"),sQuery(id+"F13.wireOp",EDGE,"E31.rect.top"),sQuery(id+"F13.wireOp",EDGE,"E31.rect.left"),sQuery(id+"F13.wireOp",EDGE,"E31.rect.right")])]}),"instanceName":"1"}),"instanceName":"1"});
            var Q5;
            Q5=makeQuery(id+"F17.opPattern","COPY",BODY,{"derivedFrom":makeQuery(id+"F14.opExtrude","SWEPT_BODY",BODY,{"disambiguationData":[OSD([sQuery(id+"F13.wireOp",EDGE,"E31.rect.bottom"),sQuery(id+"F13.wireOp",EDGE,"E31.rect.top"),sQuery(id+"F13.wireOp",EDGE,"E31.rect.left"),sQuery(id+"F13.wireOp",EDGE,"E31.rect.right")])]}),"instanceName":"1"});
            var Q6;
            Q6=makeQuery(id+"F16.opPattern","COPY",BODY,{"derivedFrom":makeQuery(id+"F14.opExtrude","SWEPT_BODY",BODY,{"disambiguationData":[OSD([sQuery(id+"F13.wireOp",EDGE,"E31.rect.bottom"),sQuery(id+"F13.wireOp",EDGE,"E31.rect.top"),sQuery(id+"F13.wireOp",EDGE,"E31.rect.left"),sQuery(id+"F13.wireOp",EDGE,"E31.rect.right")])]}),"instanceName":"1"});
            var Q7;
            Q7=makeQuery(id+"F14.opExtrude","SWEPT_BODY",BODY,{"disambiguationData":[OSD([sQuery(id+"F13.wireOp",EDGE,"E31.rect.bottom"),sQuery(id+"F13.wireOp",EDGE,"E31.rect.top"),sQuery(id+"F13.wireOp",EDGE,"E31.rect.left"),sQuery(id+"F13.wireOp",EDGE,"E31.rect.right")])]});
            var Q8;
            Q8=makeQuery(id+"F5.opExtrude","CAP_EDGE",EDGE,{"disambiguationData":[OSD([sQuery(id+"F4.wireOp",EDGE,"E27.left")])],"isStart":true});
            transform(context, id + "F19", {"entities" : qUnion([Q0, Q1, Q2, Q3, Q4, Q5, Q6, Q7]), "transformType" : TransformType.ROTATION, "transformAxis" : qUnion([Q8]), "angle" : 28.8 * degree, "makeCopy" : true});
        }
        {
            var Q0;
            Q0=makeQuery(id+"F14.opExtrude","SWEPT_BODY",BODY,{"disambiguationData":[OSD([sQuery(id+"F13.wireOp",EDGE,"E31.rect.bottom"),sQuery(id+"F13.wireOp",EDGE,"E31.rect.top"),sQuery(id+"F13.wireOp",EDGE,"E31.rect.left"),sQuery(id+"F13.wireOp",EDGE,"E31.rect.right")])]});
            var Q1;
            Q1=makeQuery(id+"F16.opPattern","COPY",BODY,{"derivedFrom":makeQuery(id+"F14.opExtrude","SWEPT_BODY",BODY,{"disambiguationData":[OSD([sQuery(id+"F13.wireOp",EDGE,"E31.rect.bottom"),sQuery(id+"F13.wireOp",EDGE,"E31.rect.top"),sQuery(id+"F13.wireOp",EDGE,"E31.rect.left"),sQuery(id+"F13.wireOp",EDGE,"E31.rect.right")])]}),"instanceName":"1"});
            var Q2;
            Q2=makeQuery(id+"F17.opPattern","COPY",BODY,{"derivedFrom":makeQuery(id+"F14.opExtrude","SWEPT_BODY",BODY,{"disambiguationData":[OSD([sQuery(id+"F13.wireOp",EDGE,"E31.rect.bottom"),sQuery(id+"F13.wireOp",EDGE,"E31.rect.top"),sQuery(id+"F13.wireOp",EDGE,"E31.rect.left"),sQuery(id+"F13.wireOp",EDGE,"E31.rect.right")])]}),"instanceName":"1"});
            var Q3;
            Q3=makeQuery(id+"F17.opPattern","COPY",BODY,{"derivedFrom":makeQuery(id+"F16.opPattern","COPY",BODY,{"derivedFrom":makeQuery(id+"F14.opExtrude","SWEPT_BODY",BODY,{"disambiguationData":[OSD([sQuery(id+"F13.wireOp",EDGE,"E31.rect.bottom"),sQuery(id+"F13.wireOp",EDGE,"E31.rect.top"),sQuery(id+"F13.wireOp",EDGE,"E31.rect.left"),sQuery(id+"F13.wireOp",EDGE,"E31.rect.right")])]}),"instanceName":"1"}),"instanceName":"1"});
            var Q4;
            Q4=makeQuery(id+"F18.opPattern","COPY",BODY,{"derivedFrom":makeQuery(id+"F14.opExtrude","SWEPT_BODY",BODY,{"disambiguationData":[OSD([sQuery(id+"F13.wireOp",EDGE,"E31.rect.bottom"),sQuery(id+"F13.wireOp",EDGE,"E31.rect.top"),sQuery(id+"F13.wireOp",EDGE,"E31.rect.left"),sQuery(id+"F13.wireOp",EDGE,"E31.rect.right")])]}),"instanceName":"1"});
            var Q5;
            Q5=makeQuery(id+"F18.opPattern","COPY",BODY,{"derivedFrom":makeQuery(id+"F16.opPattern","COPY",BODY,{"derivedFrom":makeQuery(id+"F14.opExtrude","SWEPT_BODY",BODY,{"disambiguationData":[OSD([sQuery(id+"F13.wireOp",EDGE,"E31.rect.bottom"),sQuery(id+"F13.wireOp",EDGE,"E31.rect.top"),sQuery(id+"F13.wireOp",EDGE,"E31.rect.left"),sQuery(id+"F13.wireOp",EDGE,"E31.rect.right")])]}),"instanceName":"1"}),"instanceName":"1"});
            var Q6;
            Q6=makeQuery(id+"F18.opPattern","COPY",BODY,{"derivedFrom":makeQuery(id+"F17.opPattern","COPY",BODY,{"derivedFrom":makeQuery(id+"F14.opExtrude","SWEPT_BODY",BODY,{"disambiguationData":[OSD([sQuery(id+"F13.wireOp",EDGE,"E31.rect.bottom"),sQuery(id+"F13.wireOp",EDGE,"E31.rect.top"),sQuery(id+"F13.wireOp",EDGE,"E31.rect.left"),sQuery(id+"F13.wireOp",EDGE,"E31.rect.right")])]}),"instanceName":"1"}),"instanceName":"1"});
            var Q7;
            Q7=makeQuery(id+"F18.opPattern","COPY",BODY,{"derivedFrom":makeQuery(id+"F17.opPattern","COPY",BODY,{"derivedFrom":makeQuery(id+"F16.opPattern","COPY",BODY,{"derivedFrom":makeQuery(id+"F14.opExtrude","SWEPT_BODY",BODY,{"disambiguationData":[OSD([sQuery(id+"F13.wireOp",EDGE,"E31.rect.bottom"),sQuery(id+"F13.wireOp",EDGE,"E31.rect.top"),sQuery(id+"F13.wireOp",EDGE,"E31.rect.left"),sQuery(id+"F13.wireOp",EDGE,"E31.rect.right")])]}),"instanceName":"1"}),"instanceName":"1"}),"instanceName":"1"});
            var Q8;
            Q8=makeQuery(id+"F19.opPattern","COPY",BODY,{"derivedFrom":makeQuery(id+"F14.opExtrude","SWEPT_BODY",BODY,{"disambiguationData":[OSD([sQuery(id+"F13.wireOp",EDGE,"E31.rect.bottom"),sQuery(id+"F13.wireOp",EDGE,"E31.rect.top"),sQuery(id+"F13.wireOp",EDGE,"E31.rect.left"),sQuery(id+"F13.wireOp",EDGE,"E31.rect.right")])]}),"instanceName":"1"});
            var Q9;
            Q9=makeQuery(id+"F19.opPattern","COPY",BODY,{"derivedFrom":makeQuery(id+"F16.opPattern","COPY",BODY,{"derivedFrom":makeQuery(id+"F14.opExtrude","SWEPT_BODY",BODY,{"disambiguationData":[OSD([sQuery(id+"F13.wireOp",EDGE,"E31.rect.bottom"),sQuery(id+"F13.wireOp",EDGE,"E31.rect.top"),sQuery(id+"F13.wireOp",EDGE,"E31.rect.left"),sQuery(id+"F13.wireOp",EDGE,"E31.rect.right")])]}),"instanceName":"1"}),"instanceName":"1"});
            var Q10;
            Q10=makeQuery(id+"F19.opPattern","COPY",BODY,{"derivedFrom":makeQuery(id+"F17.opPattern","COPY",BODY,{"derivedFrom":makeQuery(id+"F14.opExtrude","SWEPT_BODY",BODY,{"disambiguationData":[OSD([sQuery(id+"F13.wireOp",EDGE,"E31.rect.bottom"),sQuery(id+"F13.wireOp",EDGE,"E31.rect.top"),sQuery(id+"F13.wireOp",EDGE,"E31.rect.left"),sQuery(id+"F13.wireOp",EDGE,"E31.rect.right")])]}),"instanceName":"1"}),"instanceName":"1"});
            var Q11;
            Q11=makeQuery(id+"F19.opPattern","COPY",BODY,{"derivedFrom":makeQuery(id+"F17.opPattern","COPY",BODY,{"derivedFrom":makeQuery(id+"F16.opPattern","COPY",BODY,{"derivedFrom":makeQuery(id+"F14.opExtrude","SWEPT_BODY",BODY,{"disambiguationData":[OSD([sQuery(id+"F13.wireOp",EDGE,"E31.rect.bottom"),sQuery(id+"F13.wireOp",EDGE,"E31.rect.top"),sQuery(id+"F13.wireOp",EDGE,"E31.rect.left"),sQuery(id+"F13.wireOp",EDGE,"E31.rect.right")])]}),"instanceName":"1"}),"instanceName":"1"}),"instanceName":"1"});
            var Q12;
            Q12=makeQuery(id+"F19.opPattern","COPY",BODY,{"derivedFrom":makeQuery(id+"F18.opPattern","COPY",BODY,{"derivedFrom":makeQuery(id+"F14.opExtrude","SWEPT_BODY",BODY,{"disambiguationData":[OSD([sQuery(id+"F13.wireOp",EDGE,"E31.rect.bottom"),sQuery(id+"F13.wireOp",EDGE,"E31.rect.top"),sQuery(id+"F13.wireOp",EDGE,"E31.rect.left"),sQuery(id+"F13.wireOp",EDGE,"E31.rect.right")])]}),"instanceName":"1"}),"instanceName":"1"});
            var Q13;
            Q13=makeQuery(id+"F19.opPattern","COPY",BODY,{"derivedFrom":makeQuery(id+"F18.opPattern","COPY",BODY,{"derivedFrom":makeQuery(id+"F16.opPattern","COPY",BODY,{"derivedFrom":makeQuery(id+"F14.opExtrude","SWEPT_BODY",BODY,{"disambiguationData":[OSD([sQuery(id+"F13.wireOp",EDGE,"E31.rect.bottom"),sQuery(id+"F13.wireOp",EDGE,"E31.rect.top"),sQuery(id+"F13.wireOp",EDGE,"E31.rect.left"),sQuery(id+"F13.wireOp",EDGE,"E31.rect.right")])]}),"instanceName":"1"}),"instanceName":"1"}),"instanceName":"1"});
            var Q14;
            Q14=makeQuery(id+"F19.opPattern","COPY",BODY,{"derivedFrom":makeQuery(id+"F18.opPattern","COPY",BODY,{"derivedFrom":makeQuery(id+"F17.opPattern","COPY",BODY,{"derivedFrom":makeQuery(id+"F14.opExtrude","SWEPT_BODY",BODY,{"disambiguationData":[OSD([sQuery(id+"F13.wireOp",EDGE,"E31.rect.bottom"),sQuery(id+"F13.wireOp",EDGE,"E31.rect.top"),sQuery(id+"F13.wireOp",EDGE,"E31.rect.left"),sQuery(id+"F13.wireOp",EDGE,"E31.rect.right")])]}),"instanceName":"1"}),"instanceName":"1"}),"instanceName":"1"});
            var Q15;
            Q15=makeQuery(id+"F19.opPattern","COPY",BODY,{"derivedFrom":makeQuery(id+"F18.opPattern","COPY",BODY,{"derivedFrom":makeQuery(id+"F17.opPattern","COPY",BODY,{"derivedFrom":makeQuery(id+"F16.opPattern","COPY",BODY,{"derivedFrom":makeQuery(id+"F14.opExtrude","SWEPT_BODY",BODY,{"disambiguationData":[OSD([sQuery(id+"F13.wireOp",EDGE,"E31.rect.bottom"),sQuery(id+"F13.wireOp",EDGE,"E31.rect.top"),sQuery(id+"F13.wireOp",EDGE,"E31.rect.left"),sQuery(id+"F13.wireOp",EDGE,"E31.rect.right")])]}),"instanceName":"1"}),"instanceName":"1"}),"instanceName":"1"}),"instanceName":"1"});
            var Q16;
            Q16=makeQuery(id+"F5.opExtrude","CAP_EDGE",EDGE,{"disambiguationData":[OSD([sQuery(id+"F4.wireOp",EDGE,"E27.left")])],"isStart":true});
            transform(context, id + "F20", {"entities" : qUnion([Q0, Q1, Q2, Q3, Q4, Q5, Q6, Q7, Q8, Q9, Q10, Q11, Q12, Q13, Q14, Q15]), "transformType" : TransformType.ROTATION, "transformAxis" : qUnion([Q16]), "angle" : 57.6 * degree, "makeCopy" : true});
        }
        {
            var Q0;
            Q0=makeQuery(id+"F14.opExtrude","SWEPT_BODY",BODY,{"disambiguationData":[OSD([sQuery(id+"F13.wireOp",EDGE,"E31.rect.bottom"),sQuery(id+"F13.wireOp",EDGE,"E31.rect.top"),sQuery(id+"F13.wireOp",EDGE,"E31.rect.left"),sQuery(id+"F13.wireOp",EDGE,"E31.rect.right")])]});
            var Q1;
            Q1=makeQuery(id+"F16.opPattern","COPY",BODY,{"derivedFrom":makeQuery(id+"F14.opExtrude","SWEPT_BODY",BODY,{"disambiguationData":[OSD([sQuery(id+"F13.wireOp",EDGE,"E31.rect.bottom"),sQuery(id+"F13.wireOp",EDGE,"E31.rect.top"),sQuery(id+"F13.wireOp",EDGE,"E31.rect.left"),sQuery(id+"F13.wireOp",EDGE,"E31.rect.right")])]}),"instanceName":"1"});
            var Q2;
            Q2=makeQuery(id+"F17.opPattern","COPY",BODY,{"derivedFrom":makeQuery(id+"F14.opExtrude","SWEPT_BODY",BODY,{"disambiguationData":[OSD([sQuery(id+"F13.wireOp",EDGE,"E31.rect.bottom"),sQuery(id+"F13.wireOp",EDGE,"E31.rect.top"),sQuery(id+"F13.wireOp",EDGE,"E31.rect.left"),sQuery(id+"F13.wireOp",EDGE,"E31.rect.right")])]}),"instanceName":"1"});
            var Q3;
            Q3=makeQuery(id+"F17.opPattern","COPY",BODY,{"derivedFrom":makeQuery(id+"F16.opPattern","COPY",BODY,{"derivedFrom":makeQuery(id+"F14.opExtrude","SWEPT_BODY",BODY,{"disambiguationData":[OSD([sQuery(id+"F13.wireOp",EDGE,"E31.rect.bottom"),sQuery(id+"F13.wireOp",EDGE,"E31.rect.top"),sQuery(id+"F13.wireOp",EDGE,"E31.rect.left"),sQuery(id+"F13.wireOp",EDGE,"E31.rect.right")])]}),"instanceName":"1"}),"instanceName":"1"});
            var Q4;
            Q4=makeQuery(id+"F18.opPattern","COPY",BODY,{"derivedFrom":makeQuery(id+"F14.opExtrude","SWEPT_BODY",BODY,{"disambiguationData":[OSD([sQuery(id+"F13.wireOp",EDGE,"E31.rect.bottom"),sQuery(id+"F13.wireOp",EDGE,"E31.rect.top"),sQuery(id+"F13.wireOp",EDGE,"E31.rect.left"),sQuery(id+"F13.wireOp",EDGE,"E31.rect.right")])]}),"instanceName":"1"});
            var Q5;
            Q5=makeQuery(id+"F18.opPattern","COPY",BODY,{"derivedFrom":makeQuery(id+"F16.opPattern","COPY",BODY,{"derivedFrom":makeQuery(id+"F14.opExtrude","SWEPT_BODY",BODY,{"disambiguationData":[OSD([sQuery(id+"F13.wireOp",EDGE,"E31.rect.bottom"),sQuery(id+"F13.wireOp",EDGE,"E31.rect.top"),sQuery(id+"F13.wireOp",EDGE,"E31.rect.left"),sQuery(id+"F13.wireOp",EDGE,"E31.rect.right")])]}),"instanceName":"1"}),"instanceName":"1"});
            var Q6;
            Q6=makeQuery(id+"F18.opPattern","COPY",BODY,{"derivedFrom":makeQuery(id+"F17.opPattern","COPY",BODY,{"derivedFrom":makeQuery(id+"F14.opExtrude","SWEPT_BODY",BODY,{"disambiguationData":[OSD([sQuery(id+"F13.wireOp",EDGE,"E31.rect.bottom"),sQuery(id+"F13.wireOp",EDGE,"E31.rect.top"),sQuery(id+"F13.wireOp",EDGE,"E31.rect.left"),sQuery(id+"F13.wireOp",EDGE,"E31.rect.right")])]}),"instanceName":"1"}),"instanceName":"1"});
            var Q7;
            Q7=makeQuery(id+"F18.opPattern","COPY",BODY,{"derivedFrom":makeQuery(id+"F17.opPattern","COPY",BODY,{"derivedFrom":makeQuery(id+"F16.opPattern","COPY",BODY,{"derivedFrom":makeQuery(id+"F14.opExtrude","SWEPT_BODY",BODY,{"disambiguationData":[OSD([sQuery(id+"F13.wireOp",EDGE,"E31.rect.bottom"),sQuery(id+"F13.wireOp",EDGE,"E31.rect.top"),sQuery(id+"F13.wireOp",EDGE,"E31.rect.left"),sQuery(id+"F13.wireOp",EDGE,"E31.rect.right")])]}),"instanceName":"1"}),"instanceName":"1"}),"instanceName":"1"});
            var Q8;
            Q8=makeQuery(id+"F19.opPattern","COPY",BODY,{"derivedFrom":makeQuery(id+"F14.opExtrude","SWEPT_BODY",BODY,{"disambiguationData":[OSD([sQuery(id+"F13.wireOp",EDGE,"E31.rect.bottom"),sQuery(id+"F13.wireOp",EDGE,"E31.rect.top"),sQuery(id+"F13.wireOp",EDGE,"E31.rect.left"),sQuery(id+"F13.wireOp",EDGE,"E31.rect.right")])]}),"instanceName":"1"});
            var Q9;
            Q9=makeQuery(id+"F19.opPattern","COPY",BODY,{"derivedFrom":makeQuery(id+"F16.opPattern","COPY",BODY,{"derivedFrom":makeQuery(id+"F14.opExtrude","SWEPT_BODY",BODY,{"disambiguationData":[OSD([sQuery(id+"F13.wireOp",EDGE,"E31.rect.bottom"),sQuery(id+"F13.wireOp",EDGE,"E31.rect.top"),sQuery(id+"F13.wireOp",EDGE,"E31.rect.left"),sQuery(id+"F13.wireOp",EDGE,"E31.rect.right")])]}),"instanceName":"1"}),"instanceName":"1"});
            var Q10;
            Q10=makeQuery(id+"F19.opPattern","COPY",BODY,{"derivedFrom":makeQuery(id+"F17.opPattern","COPY",BODY,{"derivedFrom":makeQuery(id+"F14.opExtrude","SWEPT_BODY",BODY,{"disambiguationData":[OSD([sQuery(id+"F13.wireOp",EDGE,"E31.rect.bottom"),sQuery(id+"F13.wireOp",EDGE,"E31.rect.top"),sQuery(id+"F13.wireOp",EDGE,"E31.rect.left"),sQuery(id+"F13.wireOp",EDGE,"E31.rect.right")])]}),"instanceName":"1"}),"instanceName":"1"});
            var Q11;
            Q11=makeQuery(id+"F19.opPattern","COPY",BODY,{"derivedFrom":makeQuery(id+"F17.opPattern","COPY",BODY,{"derivedFrom":makeQuery(id+"F16.opPattern","COPY",BODY,{"derivedFrom":makeQuery(id+"F14.opExtrude","SWEPT_BODY",BODY,{"disambiguationData":[OSD([sQuery(id+"F13.wireOp",EDGE,"E31.rect.bottom"),sQuery(id+"F13.wireOp",EDGE,"E31.rect.top"),sQuery(id+"F13.wireOp",EDGE,"E31.rect.left"),sQuery(id+"F13.wireOp",EDGE,"E31.rect.right")])]}),"instanceName":"1"}),"instanceName":"1"}),"instanceName":"1"});
            var Q12;
            Q12=makeQuery(id+"F19.opPattern","COPY",BODY,{"derivedFrom":makeQuery(id+"F18.opPattern","COPY",BODY,{"derivedFrom":makeQuery(id+"F14.opExtrude","SWEPT_BODY",BODY,{"disambiguationData":[OSD([sQuery(id+"F13.wireOp",EDGE,"E31.rect.bottom"),sQuery(id+"F13.wireOp",EDGE,"E31.rect.top"),sQuery(id+"F13.wireOp",EDGE,"E31.rect.left"),sQuery(id+"F13.wireOp",EDGE,"E31.rect.right")])]}),"instanceName":"1"}),"instanceName":"1"});
            var Q13;
            Q13=makeQuery(id+"F19.opPattern","COPY",BODY,{"derivedFrom":makeQuery(id+"F18.opPattern","COPY",BODY,{"derivedFrom":makeQuery(id+"F16.opPattern","COPY",BODY,{"derivedFrom":makeQuery(id+"F14.opExtrude","SWEPT_BODY",BODY,{"disambiguationData":[OSD([sQuery(id+"F13.wireOp",EDGE,"E31.rect.bottom"),sQuery(id+"F13.wireOp",EDGE,"E31.rect.top"),sQuery(id+"F13.wireOp",EDGE,"E31.rect.left"),sQuery(id+"F13.wireOp",EDGE,"E31.rect.right")])]}),"instanceName":"1"}),"instanceName":"1"}),"instanceName":"1"});
            var Q14;
            Q14=makeQuery(id+"F19.opPattern","COPY",BODY,{"derivedFrom":makeQuery(id+"F18.opPattern","COPY",BODY,{"derivedFrom":makeQuery(id+"F17.opPattern","COPY",BODY,{"derivedFrom":makeQuery(id+"F14.opExtrude","SWEPT_BODY",BODY,{"disambiguationData":[OSD([sQuery(id+"F13.wireOp",EDGE,"E31.rect.bottom"),sQuery(id+"F13.wireOp",EDGE,"E31.rect.top"),sQuery(id+"F13.wireOp",EDGE,"E31.rect.left"),sQuery(id+"F13.wireOp",EDGE,"E31.rect.right")])]}),"instanceName":"1"}),"instanceName":"1"}),"instanceName":"1"});
            var Q15;
            Q15=makeQuery(id+"F19.opPattern","COPY",BODY,{"derivedFrom":makeQuery(id+"F18.opPattern","COPY",BODY,{"derivedFrom":makeQuery(id+"F17.opPattern","COPY",BODY,{"derivedFrom":makeQuery(id+"F16.opPattern","COPY",BODY,{"derivedFrom":makeQuery(id+"F14.opExtrude","SWEPT_BODY",BODY,{"disambiguationData":[OSD([sQuery(id+"F13.wireOp",EDGE,"E31.rect.bottom"),sQuery(id+"F13.wireOp",EDGE,"E31.rect.top"),sQuery(id+"F13.wireOp",EDGE,"E31.rect.left"),sQuery(id+"F13.wireOp",EDGE,"E31.rect.right")])]}),"instanceName":"1"}),"instanceName":"1"}),"instanceName":"1"}),"instanceName":"1"});
            var Q16;
            Q16=makeQuery(id+"F20.opPattern","COPY",BODY,{"derivedFrom":makeQuery(id+"F14.opExtrude","SWEPT_BODY",BODY,{"disambiguationData":[OSD([sQuery(id+"F13.wireOp",EDGE,"E31.rect.bottom"),sQuery(id+"F13.wireOp",EDGE,"E31.rect.top"),sQuery(id+"F13.wireOp",EDGE,"E31.rect.left"),sQuery(id+"F13.wireOp",EDGE,"E31.rect.right")])]}),"instanceName":"1"});
            var Q17;
            Q17=makeQuery(id+"F20.opPattern","COPY",BODY,{"derivedFrom":makeQuery(id+"F16.opPattern","COPY",BODY,{"derivedFrom":makeQuery(id+"F14.opExtrude","SWEPT_BODY",BODY,{"disambiguationData":[OSD([sQuery(id+"F13.wireOp",EDGE,"E31.rect.bottom"),sQuery(id+"F13.wireOp",EDGE,"E31.rect.top"),sQuery(id+"F13.wireOp",EDGE,"E31.rect.left"),sQuery(id+"F13.wireOp",EDGE,"E31.rect.right")])]}),"instanceName":"1"}),"instanceName":"1"});
            var Q18;
            Q18=makeQuery(id+"F20.opPattern","COPY",BODY,{"derivedFrom":makeQuery(id+"F17.opPattern","COPY",BODY,{"derivedFrom":makeQuery(id+"F14.opExtrude","SWEPT_BODY",BODY,{"disambiguationData":[OSD([sQuery(id+"F13.wireOp",EDGE,"E31.rect.bottom"),sQuery(id+"F13.wireOp",EDGE,"E31.rect.top"),sQuery(id+"F13.wireOp",EDGE,"E31.rect.left"),sQuery(id+"F13.wireOp",EDGE,"E31.rect.right")])]}),"instanceName":"1"}),"instanceName":"1"});
            var Q19;
            Q19=makeQuery(id+"F20.opPattern","COPY",BODY,{"derivedFrom":makeQuery(id+"F17.opPattern","COPY",BODY,{"derivedFrom":makeQuery(id+"F16.opPattern","COPY",BODY,{"derivedFrom":makeQuery(id+"F14.opExtrude","SWEPT_BODY",BODY,{"disambiguationData":[OSD([sQuery(id+"F13.wireOp",EDGE,"E31.rect.bottom"),sQuery(id+"F13.wireOp",EDGE,"E31.rect.top"),sQuery(id+"F13.wireOp",EDGE,"E31.rect.left"),sQuery(id+"F13.wireOp",EDGE,"E31.rect.right")])]}),"instanceName":"1"}),"instanceName":"1"}),"instanceName":"1"});
            var Q20;
            Q20=makeQuery(id+"F20.opPattern","COPY",BODY,{"derivedFrom":makeQuery(id+"F18.opPattern","COPY",BODY,{"derivedFrom":makeQuery(id+"F14.opExtrude","SWEPT_BODY",BODY,{"disambiguationData":[OSD([sQuery(id+"F13.wireOp",EDGE,"E31.rect.bottom"),sQuery(id+"F13.wireOp",EDGE,"E31.rect.top"),sQuery(id+"F13.wireOp",EDGE,"E31.rect.left"),sQuery(id+"F13.wireOp",EDGE,"E31.rect.right")])]}),"instanceName":"1"}),"instanceName":"1"});
            var Q21;
            Q21=makeQuery(id+"F20.opPattern","COPY",BODY,{"derivedFrom":makeQuery(id+"F18.opPattern","COPY",BODY,{"derivedFrom":makeQuery(id+"F16.opPattern","COPY",BODY,{"derivedFrom":makeQuery(id+"F14.opExtrude","SWEPT_BODY",BODY,{"disambiguationData":[OSD([sQuery(id+"F13.wireOp",EDGE,"E31.rect.bottom"),sQuery(id+"F13.wireOp",EDGE,"E31.rect.top"),sQuery(id+"F13.wireOp",EDGE,"E31.rect.left"),sQuery(id+"F13.wireOp",EDGE,"E31.rect.right")])]}),"instanceName":"1"}),"instanceName":"1"}),"instanceName":"1"});
            var Q22;
            Q22=makeQuery(id+"F20.opPattern","COPY",BODY,{"derivedFrom":makeQuery(id+"F18.opPattern","COPY",BODY,{"derivedFrom":makeQuery(id+"F17.opPattern","COPY",BODY,{"derivedFrom":makeQuery(id+"F14.opExtrude","SWEPT_BODY",BODY,{"disambiguationData":[OSD([sQuery(id+"F13.wireOp",EDGE,"E31.rect.bottom"),sQuery(id+"F13.wireOp",EDGE,"E31.rect.top"),sQuery(id+"F13.wireOp",EDGE,"E31.rect.left"),sQuery(id+"F13.wireOp",EDGE,"E31.rect.right")])]}),"instanceName":"1"}),"instanceName":"1"}),"instanceName":"1"});
            var Q23;
            Q23=makeQuery(id+"F20.opPattern","COPY",BODY,{"derivedFrom":makeQuery(id+"F18.opPattern","COPY",BODY,{"derivedFrom":makeQuery(id+"F17.opPattern","COPY",BODY,{"derivedFrom":makeQuery(id+"F16.opPattern","COPY",BODY,{"derivedFrom":makeQuery(id+"F14.opExtrude","SWEPT_BODY",BODY,{"disambiguationData":[OSD([sQuery(id+"F13.wireOp",EDGE,"E31.rect.bottom"),sQuery(id+"F13.wireOp",EDGE,"E31.rect.top"),sQuery(id+"F13.wireOp",EDGE,"E31.rect.left"),sQuery(id+"F13.wireOp",EDGE,"E31.rect.right")])]}),"instanceName":"1"}),"instanceName":"1"}),"instanceName":"1"}),"instanceName":"1"});
            var Q24;
            Q24=makeQuery(id+"F20.opPattern","COPY",BODY,{"derivedFrom":makeQuery(id+"F19.opPattern","COPY",BODY,{"derivedFrom":makeQuery(id+"F14.opExtrude","SWEPT_BODY",BODY,{"disambiguationData":[OSD([sQuery(id+"F13.wireOp",EDGE,"E31.rect.bottom"),sQuery(id+"F13.wireOp",EDGE,"E31.rect.top"),sQuery(id+"F13.wireOp",EDGE,"E31.rect.left"),sQuery(id+"F13.wireOp",EDGE,"E31.rect.right")])]}),"instanceName":"1"}),"instanceName":"1"});
            var Q25;
            Q25=makeQuery(id+"F20.opPattern","COPY",BODY,{"derivedFrom":makeQuery(id+"F19.opPattern","COPY",BODY,{"derivedFrom":makeQuery(id+"F16.opPattern","COPY",BODY,{"derivedFrom":makeQuery(id+"F14.opExtrude","SWEPT_BODY",BODY,{"disambiguationData":[OSD([sQuery(id+"F13.wireOp",EDGE,"E31.rect.bottom"),sQuery(id+"F13.wireOp",EDGE,"E31.rect.top"),sQuery(id+"F13.wireOp",EDGE,"E31.rect.left"),sQuery(id+"F13.wireOp",EDGE,"E31.rect.right")])]}),"instanceName":"1"}),"instanceName":"1"}),"instanceName":"1"});
            var Q26;
            Q26=makeQuery(id+"F20.opPattern","COPY",BODY,{"derivedFrom":makeQuery(id+"F19.opPattern","COPY",BODY,{"derivedFrom":makeQuery(id+"F17.opPattern","COPY",BODY,{"derivedFrom":makeQuery(id+"F14.opExtrude","SWEPT_BODY",BODY,{"disambiguationData":[OSD([sQuery(id+"F13.wireOp",EDGE,"E31.rect.bottom"),sQuery(id+"F13.wireOp",EDGE,"E31.rect.top"),sQuery(id+"F13.wireOp",EDGE,"E31.rect.left"),sQuery(id+"F13.wireOp",EDGE,"E31.rect.right")])]}),"instanceName":"1"}),"instanceName":"1"}),"instanceName":"1"});
            var Q27;
            Q27=makeQuery(id+"F20.opPattern","COPY",BODY,{"derivedFrom":makeQuery(id+"F19.opPattern","COPY",BODY,{"derivedFrom":makeQuery(id+"F17.opPattern","COPY",BODY,{"derivedFrom":makeQuery(id+"F16.opPattern","COPY",BODY,{"derivedFrom":makeQuery(id+"F14.opExtrude","SWEPT_BODY",BODY,{"disambiguationData":[OSD([sQuery(id+"F13.wireOp",EDGE,"E31.rect.bottom"),sQuery(id+"F13.wireOp",EDGE,"E31.rect.top"),sQuery(id+"F13.wireOp",EDGE,"E31.rect.left"),sQuery(id+"F13.wireOp",EDGE,"E31.rect.right")])]}),"instanceName":"1"}),"instanceName":"1"}),"instanceName":"1"}),"instanceName":"1"});
            var Q28;
            Q28=makeQuery(id+"F20.opPattern","COPY",BODY,{"derivedFrom":makeQuery(id+"F19.opPattern","COPY",BODY,{"derivedFrom":makeQuery(id+"F18.opPattern","COPY",BODY,{"derivedFrom":makeQuery(id+"F14.opExtrude","SWEPT_BODY",BODY,{"disambiguationData":[OSD([sQuery(id+"F13.wireOp",EDGE,"E31.rect.bottom"),sQuery(id+"F13.wireOp",EDGE,"E31.rect.top"),sQuery(id+"F13.wireOp",EDGE,"E31.rect.left"),sQuery(id+"F13.wireOp",EDGE,"E31.rect.right")])]}),"instanceName":"1"}),"instanceName":"1"}),"instanceName":"1"});
            var Q29;
            Q29=makeQuery(id+"F20.opPattern","COPY",BODY,{"derivedFrom":makeQuery(id+"F19.opPattern","COPY",BODY,{"derivedFrom":makeQuery(id+"F18.opPattern","COPY",BODY,{"derivedFrom":makeQuery(id+"F16.opPattern","COPY",BODY,{"derivedFrom":makeQuery(id+"F14.opExtrude","SWEPT_BODY",BODY,{"disambiguationData":[OSD([sQuery(id+"F13.wireOp",EDGE,"E31.rect.bottom"),sQuery(id+"F13.wireOp",EDGE,"E31.rect.top"),sQuery(id+"F13.wireOp",EDGE,"E31.rect.left"),sQuery(id+"F13.wireOp",EDGE,"E31.rect.right")])]}),"instanceName":"1"}),"instanceName":"1"}),"instanceName":"1"}),"instanceName":"1"});
            var Q30;
            Q30=makeQuery(id+"F20.opPattern","COPY",BODY,{"derivedFrom":makeQuery(id+"F19.opPattern","COPY",BODY,{"derivedFrom":makeQuery(id+"F18.opPattern","COPY",BODY,{"derivedFrom":makeQuery(id+"F17.opPattern","COPY",BODY,{"derivedFrom":makeQuery(id+"F14.opExtrude","SWEPT_BODY",BODY,{"disambiguationData":[OSD([sQuery(id+"F13.wireOp",EDGE,"E31.rect.bottom"),sQuery(id+"F13.wireOp",EDGE,"E31.rect.top"),sQuery(id+"F13.wireOp",EDGE,"E31.rect.left"),sQuery(id+"F13.wireOp",EDGE,"E31.rect.right")])]}),"instanceName":"1"}),"instanceName":"1"}),"instanceName":"1"}),"instanceName":"1"});
            var Q31;
            Q31=makeQuery(id+"F20.opPattern","COPY",BODY,{"derivedFrom":makeQuery(id+"F19.opPattern","COPY",BODY,{"derivedFrom":makeQuery(id+"F18.opPattern","COPY",BODY,{"derivedFrom":makeQuery(id+"F17.opPattern","COPY",BODY,{"derivedFrom":makeQuery(id+"F16.opPattern","COPY",BODY,{"derivedFrom":makeQuery(id+"F14.opExtrude","SWEPT_BODY",BODY,{"disambiguationData":[OSD([sQuery(id+"F13.wireOp",EDGE,"E31.rect.bottom"),sQuery(id+"F13.wireOp",EDGE,"E31.rect.top"),sQuery(id+"F13.wireOp",EDGE,"E31.rect.left"),sQuery(id+"F13.wireOp",EDGE,"E31.rect.right")])]}),"instanceName":"1"}),"instanceName":"1"}),"instanceName":"1"}),"instanceName":"1"}),"instanceName":"1"});
            var Q32;
            Q32=makeQuery(id+"F5.opExtrude","CAP_EDGE",EDGE,{"disambiguationData":[OSD([sQuery(id+"F4.wireOp",EDGE,"E27.left")])],"isStart":true});
            transform(context, id + "F21", {"entities" : qUnion([Q0, Q1, Q2, Q3, Q4, Q5, Q6, Q7, Q8, Q9, Q10, Q11, Q12, Q13, Q14, Q15, Q16, Q17, Q18, Q19, Q20, Q21, Q22, Q23, Q24, Q25, Q26, Q27, Q28, Q29, Q30, Q31]), "transformType" : TransformType.ROTATION, "transformAxis" : qUnion([Q32]), "angle" : 115.2 * degree, "makeCopy" : true});
        }
        {
            var Q0;
            Q0=makeQuery(id+"F21.opPattern","COPY",BODY,{"derivedFrom":makeQuery(id+"F20.opPattern","COPY",BODY,{"derivedFrom":makeQuery(id+"F19.opPattern","COPY",BODY,{"derivedFrom":makeQuery(id+"F18.opPattern","COPY",BODY,{"derivedFrom":makeQuery(id+"F17.opPattern","COPY",BODY,{"derivedFrom":makeQuery(id+"F16.opPattern","COPY",BODY,{"derivedFrom":makeQuery(id+"F14.opExtrude","SWEPT_BODY",BODY,{"disambiguationData":[OSD([sQuery(id+"F13.wireOp",EDGE,"E31.rect.bottom"),sQuery(id+"F13.wireOp",EDGE,"E31.rect.top"),sQuery(id+"F13.wireOp",EDGE,"E31.rect.left"),sQuery(id+"F13.wireOp",EDGE,"E31.rect.right")])]}),"instanceName":"1"}),"instanceName":"1"}),"instanceName":"1"}),"instanceName":"1"}),"instanceName":"1"}),"instanceName":"1"});
            var Q1;
            Q1=makeQuery(id+"F21.opPattern","COPY",BODY,{"derivedFrom":makeQuery(id+"F20.opPattern","COPY",BODY,{"derivedFrom":makeQuery(id+"F19.opPattern","COPY",BODY,{"derivedFrom":makeQuery(id+"F18.opPattern","COPY",BODY,{"derivedFrom":makeQuery(id+"F17.opPattern","COPY",BODY,{"derivedFrom":makeQuery(id+"F14.opExtrude","SWEPT_BODY",BODY,{"disambiguationData":[OSD([sQuery(id+"F13.wireOp",EDGE,"E31.rect.bottom"),sQuery(id+"F13.wireOp",EDGE,"E31.rect.top"),sQuery(id+"F13.wireOp",EDGE,"E31.rect.left"),sQuery(id+"F13.wireOp",EDGE,"E31.rect.right")])]}),"instanceName":"1"}),"instanceName":"1"}),"instanceName":"1"}),"instanceName":"1"}),"instanceName":"1"});
            var Q2;
            Q2=makeQuery(id+"F21.opPattern","COPY",BODY,{"derivedFrom":makeQuery(id+"F20.opPattern","COPY",BODY,{"derivedFrom":makeQuery(id+"F19.opPattern","COPY",BODY,{"derivedFrom":makeQuery(id+"F18.opPattern","COPY",BODY,{"derivedFrom":makeQuery(id+"F16.opPattern","COPY",BODY,{"derivedFrom":makeQuery(id+"F14.opExtrude","SWEPT_BODY",BODY,{"disambiguationData":[OSD([sQuery(id+"F13.wireOp",EDGE,"E31.rect.bottom"),sQuery(id+"F13.wireOp",EDGE,"E31.rect.top"),sQuery(id+"F13.wireOp",EDGE,"E31.rect.left"),sQuery(id+"F13.wireOp",EDGE,"E31.rect.right")])]}),"instanceName":"1"}),"instanceName":"1"}),"instanceName":"1"}),"instanceName":"1"}),"instanceName":"1"});
            var Q3;
            Q3=makeQuery(id+"F21.opPattern","COPY",BODY,{"derivedFrom":makeQuery(id+"F20.opPattern","COPY",BODY,{"derivedFrom":makeQuery(id+"F19.opPattern","COPY",BODY,{"derivedFrom":makeQuery(id+"F18.opPattern","COPY",BODY,{"derivedFrom":makeQuery(id+"F14.opExtrude","SWEPT_BODY",BODY,{"disambiguationData":[OSD([sQuery(id+"F13.wireOp",EDGE,"E31.rect.bottom"),sQuery(id+"F13.wireOp",EDGE,"E31.rect.top"),sQuery(id+"F13.wireOp",EDGE,"E31.rect.left"),sQuery(id+"F13.wireOp",EDGE,"E31.rect.right")])]}),"instanceName":"1"}),"instanceName":"1"}),"instanceName":"1"}),"instanceName":"1"});
            var Q4;
            Q4=makeQuery(id+"F21.opPattern","COPY",BODY,{"derivedFrom":makeQuery(id+"F20.opPattern","COPY",BODY,{"derivedFrom":makeQuery(id+"F19.opPattern","COPY",BODY,{"derivedFrom":makeQuery(id+"F17.opPattern","COPY",BODY,{"derivedFrom":makeQuery(id+"F16.opPattern","COPY",BODY,{"derivedFrom":makeQuery(id+"F14.opExtrude","SWEPT_BODY",BODY,{"disambiguationData":[OSD([sQuery(id+"F13.wireOp",EDGE,"E31.rect.bottom"),sQuery(id+"F13.wireOp",EDGE,"E31.rect.top"),sQuery(id+"F13.wireOp",EDGE,"E31.rect.left"),sQuery(id+"F13.wireOp",EDGE,"E31.rect.right")])]}),"instanceName":"1"}),"instanceName":"1"}),"instanceName":"1"}),"instanceName":"1"}),"instanceName":"1"});
            var Q5;
            Q5=makeQuery(id+"F21.opPattern","COPY",BODY,{"derivedFrom":makeQuery(id+"F20.opPattern","COPY",BODY,{"derivedFrom":makeQuery(id+"F19.opPattern","COPY",BODY,{"derivedFrom":makeQuery(id+"F17.opPattern","COPY",BODY,{"derivedFrom":makeQuery(id+"F14.opExtrude","SWEPT_BODY",BODY,{"disambiguationData":[OSD([sQuery(id+"F13.wireOp",EDGE,"E31.rect.bottom"),sQuery(id+"F13.wireOp",EDGE,"E31.rect.top"),sQuery(id+"F13.wireOp",EDGE,"E31.rect.left"),sQuery(id+"F13.wireOp",EDGE,"E31.rect.right")])]}),"instanceName":"1"}),"instanceName":"1"}),"instanceName":"1"}),"instanceName":"1"});
            var Q6;
            Q6=makeQuery(id+"F21.opPattern","COPY",BODY,{"derivedFrom":makeQuery(id+"F20.opPattern","COPY",BODY,{"derivedFrom":makeQuery(id+"F19.opPattern","COPY",BODY,{"derivedFrom":makeQuery(id+"F16.opPattern","COPY",BODY,{"derivedFrom":makeQuery(id+"F14.opExtrude","SWEPT_BODY",BODY,{"disambiguationData":[OSD([sQuery(id+"F13.wireOp",EDGE,"E31.rect.bottom"),sQuery(id+"F13.wireOp",EDGE,"E31.rect.top"),sQuery(id+"F13.wireOp",EDGE,"E31.rect.left"),sQuery(id+"F13.wireOp",EDGE,"E31.rect.right")])]}),"instanceName":"1"}),"instanceName":"1"}),"instanceName":"1"}),"instanceName":"1"});
            var Q7;
            Q7=makeQuery(id+"F21.opPattern","COPY",BODY,{"derivedFrom":makeQuery(id+"F20.opPattern","COPY",BODY,{"derivedFrom":makeQuery(id+"F19.opPattern","COPY",BODY,{"derivedFrom":makeQuery(id+"F14.opExtrude","SWEPT_BODY",BODY,{"disambiguationData":[OSD([sQuery(id+"F13.wireOp",EDGE,"E31.rect.bottom"),sQuery(id+"F13.wireOp",EDGE,"E31.rect.top"),sQuery(id+"F13.wireOp",EDGE,"E31.rect.left"),sQuery(id+"F13.wireOp",EDGE,"E31.rect.right")])]}),"instanceName":"1"}),"instanceName":"1"}),"instanceName":"1"});
            var Q8;
            Q8=makeQuery(id+"F21.opPattern","COPY",BODY,{"derivedFrom":makeQuery(id+"F20.opPattern","COPY",BODY,{"derivedFrom":makeQuery(id+"F18.opPattern","COPY",BODY,{"derivedFrom":makeQuery(id+"F17.opPattern","COPY",BODY,{"derivedFrom":makeQuery(id+"F16.opPattern","COPY",BODY,{"derivedFrom":makeQuery(id+"F14.opExtrude","SWEPT_BODY",BODY,{"disambiguationData":[OSD([sQuery(id+"F13.wireOp",EDGE,"E31.rect.bottom"),sQuery(id+"F13.wireOp",EDGE,"E31.rect.top"),sQuery(id+"F13.wireOp",EDGE,"E31.rect.left"),sQuery(id+"F13.wireOp",EDGE,"E31.rect.right")])]}),"instanceName":"1"}),"instanceName":"1"}),"instanceName":"1"}),"instanceName":"1"}),"instanceName":"1"});
            var Q9;
            Q9=makeQuery(id+"F21.opPattern","COPY",BODY,{"derivedFrom":makeQuery(id+"F20.opPattern","COPY",BODY,{"derivedFrom":makeQuery(id+"F18.opPattern","COPY",BODY,{"derivedFrom":makeQuery(id+"F17.opPattern","COPY",BODY,{"derivedFrom":makeQuery(id+"F14.opExtrude","SWEPT_BODY",BODY,{"disambiguationData":[OSD([sQuery(id+"F13.wireOp",EDGE,"E31.rect.bottom"),sQuery(id+"F13.wireOp",EDGE,"E31.rect.top"),sQuery(id+"F13.wireOp",EDGE,"E31.rect.left"),sQuery(id+"F13.wireOp",EDGE,"E31.rect.right")])]}),"instanceName":"1"}),"instanceName":"1"}),"instanceName":"1"}),"instanceName":"1"});
            var Q10;
            Q10=makeQuery(id+"F21.opPattern","COPY",BODY,{"derivedFrom":makeQuery(id+"F20.opPattern","COPY",BODY,{"derivedFrom":makeQuery(id+"F18.opPattern","COPY",BODY,{"derivedFrom":makeQuery(id+"F16.opPattern","COPY",BODY,{"derivedFrom":makeQuery(id+"F14.opExtrude","SWEPT_BODY",BODY,{"disambiguationData":[OSD([sQuery(id+"F13.wireOp",EDGE,"E31.rect.bottom"),sQuery(id+"F13.wireOp",EDGE,"E31.rect.top"),sQuery(id+"F13.wireOp",EDGE,"E31.rect.left"),sQuery(id+"F13.wireOp",EDGE,"E31.rect.right")])]}),"instanceName":"1"}),"instanceName":"1"}),"instanceName":"1"}),"instanceName":"1"});
            var Q11;
            Q11=makeQuery(id+"F21.opPattern","COPY",BODY,{"derivedFrom":makeQuery(id+"F20.opPattern","COPY",BODY,{"derivedFrom":makeQuery(id+"F18.opPattern","COPY",BODY,{"derivedFrom":makeQuery(id+"F14.opExtrude","SWEPT_BODY",BODY,{"disambiguationData":[OSD([sQuery(id+"F13.wireOp",EDGE,"E31.rect.bottom"),sQuery(id+"F13.wireOp",EDGE,"E31.rect.top"),sQuery(id+"F13.wireOp",EDGE,"E31.rect.left"),sQuery(id+"F13.wireOp",EDGE,"E31.rect.right")])]}),"instanceName":"1"}),"instanceName":"1"}),"instanceName":"1"});
            var Q12;
            Q12=makeQuery(id+"F21.opPattern","COPY",BODY,{"derivedFrom":makeQuery(id+"F20.opPattern","COPY",BODY,{"derivedFrom":makeQuery(id+"F17.opPattern","COPY",BODY,{"derivedFrom":makeQuery(id+"F16.opPattern","COPY",BODY,{"derivedFrom":makeQuery(id+"F14.opExtrude","SWEPT_BODY",BODY,{"disambiguationData":[OSD([sQuery(id+"F13.wireOp",EDGE,"E31.rect.bottom"),sQuery(id+"F13.wireOp",EDGE,"E31.rect.top"),sQuery(id+"F13.wireOp",EDGE,"E31.rect.left"),sQuery(id+"F13.wireOp",EDGE,"E31.rect.right")])]}),"instanceName":"1"}),"instanceName":"1"}),"instanceName":"1"}),"instanceName":"1"});
            var Q13;
            Q13=makeQuery(id+"F21.opPattern","COPY",BODY,{"derivedFrom":makeQuery(id+"F20.opPattern","COPY",BODY,{"derivedFrom":makeQuery(id+"F17.opPattern","COPY",BODY,{"derivedFrom":makeQuery(id+"F14.opExtrude","SWEPT_BODY",BODY,{"disambiguationData":[OSD([sQuery(id+"F13.wireOp",EDGE,"E31.rect.bottom"),sQuery(id+"F13.wireOp",EDGE,"E31.rect.top"),sQuery(id+"F13.wireOp",EDGE,"E31.rect.left"),sQuery(id+"F13.wireOp",EDGE,"E31.rect.right")])]}),"instanceName":"1"}),"instanceName":"1"}),"instanceName":"1"});
            var Q14;
            Q14=makeQuery(id+"F21.opPattern","COPY",BODY,{"derivedFrom":makeQuery(id+"F20.opPattern","COPY",BODY,{"derivedFrom":makeQuery(id+"F16.opPattern","COPY",BODY,{"derivedFrom":makeQuery(id+"F14.opExtrude","SWEPT_BODY",BODY,{"disambiguationData":[OSD([sQuery(id+"F13.wireOp",EDGE,"E31.rect.bottom"),sQuery(id+"F13.wireOp",EDGE,"E31.rect.top"),sQuery(id+"F13.wireOp",EDGE,"E31.rect.left"),sQuery(id+"F13.wireOp",EDGE,"E31.rect.right")])]}),"instanceName":"1"}),"instanceName":"1"}),"instanceName":"1"});
            var Q15;
            Q15=makeQuery(id+"F21.opPattern","COPY",BODY,{"derivedFrom":makeQuery(id+"F20.opPattern","COPY",BODY,{"derivedFrom":makeQuery(id+"F14.opExtrude","SWEPT_BODY",BODY,{"disambiguationData":[OSD([sQuery(id+"F13.wireOp",EDGE,"E31.rect.bottom"),sQuery(id+"F13.wireOp",EDGE,"E31.rect.top"),sQuery(id+"F13.wireOp",EDGE,"E31.rect.left"),sQuery(id+"F13.wireOp",EDGE,"E31.rect.right")])]}),"instanceName":"1"}),"instanceName":"1"});
            var Q16;
            Q16=makeQuery(id+"F5.opExtrude","CAP_EDGE",EDGE,{"disambiguationData":[OSD([sQuery(id+"F4.wireOp",EDGE,"E27.left")])],"isStart":true});
            transform(context, id + "F22", {"entities" : qUnion([Q0, Q1, Q2, Q3, Q4, Q5, Q6, Q7, Q8, Q9, Q10, Q11, Q12, Q13, Q14, Q15]), "transformType" : TransformType.ROTATION, "transformAxis" : qUnion([Q16]), "angle" : 57.6 * degree, "makeCopy" : true});
        }
        {
            var Q0;
            Q0=makeQuery(id+"F22.opPattern","COPY",BODY,{"derivedFrom":makeQuery(id+"F21.opPattern","COPY",BODY,{"derivedFrom":makeQuery(id+"F20.opPattern","COPY",BODY,{"derivedFrom":makeQuery(id+"F19.opPattern","COPY",BODY,{"derivedFrom":makeQuery(id+"F18.opPattern","COPY",BODY,{"derivedFrom":makeQuery(id+"F17.opPattern","COPY",BODY,{"derivedFrom":makeQuery(id+"F16.opPattern","COPY",BODY,{"derivedFrom":makeQuery(id+"F14.opExtrude","SWEPT_BODY",BODY,{"disambiguationData":[OSD([sQuery(id+"F13.wireOp",EDGE,"E31.rect.bottom"),sQuery(id+"F13.wireOp",EDGE,"E31.rect.top"),sQuery(id+"F13.wireOp",EDGE,"E31.rect.left"),sQuery(id+"F13.wireOp",EDGE,"E31.rect.right")])]}),"instanceName":"1"}),"instanceName":"1"}),"instanceName":"1"}),"instanceName":"1"}),"instanceName":"1"}),"instanceName":"1"}),"instanceName":"1"});
            var Q1;
            Q1=makeQuery(id+"F22.opPattern","COPY",BODY,{"derivedFrom":makeQuery(id+"F21.opPattern","COPY",BODY,{"derivedFrom":makeQuery(id+"F20.opPattern","COPY",BODY,{"derivedFrom":makeQuery(id+"F19.opPattern","COPY",BODY,{"derivedFrom":makeQuery(id+"F18.opPattern","COPY",BODY,{"derivedFrom":makeQuery(id+"F17.opPattern","COPY",BODY,{"derivedFrom":makeQuery(id+"F14.opExtrude","SWEPT_BODY",BODY,{"disambiguationData":[OSD([sQuery(id+"F13.wireOp",EDGE,"E31.rect.bottom"),sQuery(id+"F13.wireOp",EDGE,"E31.rect.top"),sQuery(id+"F13.wireOp",EDGE,"E31.rect.left"),sQuery(id+"F13.wireOp",EDGE,"E31.rect.right")])]}),"instanceName":"1"}),"instanceName":"1"}),"instanceName":"1"}),"instanceName":"1"}),"instanceName":"1"}),"instanceName":"1"});
            var Q2;
            Q2=makeQuery(id+"F22.opPattern","COPY",BODY,{"derivedFrom":makeQuery(id+"F21.opPattern","COPY",BODY,{"derivedFrom":makeQuery(id+"F20.opPattern","COPY",BODY,{"derivedFrom":makeQuery(id+"F19.opPattern","COPY",BODY,{"derivedFrom":makeQuery(id+"F18.opPattern","COPY",BODY,{"derivedFrom":makeQuery(id+"F16.opPattern","COPY",BODY,{"derivedFrom":makeQuery(id+"F14.opExtrude","SWEPT_BODY",BODY,{"disambiguationData":[OSD([sQuery(id+"F13.wireOp",EDGE,"E31.rect.bottom"),sQuery(id+"F13.wireOp",EDGE,"E31.rect.top"),sQuery(id+"F13.wireOp",EDGE,"E31.rect.left"),sQuery(id+"F13.wireOp",EDGE,"E31.rect.right")])]}),"instanceName":"1"}),"instanceName":"1"}),"instanceName":"1"}),"instanceName":"1"}),"instanceName":"1"}),"instanceName":"1"});
            var Q3;
            Q3=makeQuery(id+"F22.opPattern","COPY",BODY,{"derivedFrom":makeQuery(id+"F21.opPattern","COPY",BODY,{"derivedFrom":makeQuery(id+"F20.opPattern","COPY",BODY,{"derivedFrom":makeQuery(id+"F19.opPattern","COPY",BODY,{"derivedFrom":makeQuery(id+"F18.opPattern","COPY",BODY,{"derivedFrom":makeQuery(id+"F14.opExtrude","SWEPT_BODY",BODY,{"disambiguationData":[OSD([sQuery(id+"F13.wireOp",EDGE,"E31.rect.bottom"),sQuery(id+"F13.wireOp",EDGE,"E31.rect.top"),sQuery(id+"F13.wireOp",EDGE,"E31.rect.left"),sQuery(id+"F13.wireOp",EDGE,"E31.rect.right")])]}),"instanceName":"1"}),"instanceName":"1"}),"instanceName":"1"}),"instanceName":"1"}),"instanceName":"1"});
            var Q4;
            Q4=makeQuery(id+"F22.opPattern","COPY",BODY,{"derivedFrom":makeQuery(id+"F21.opPattern","COPY",BODY,{"derivedFrom":makeQuery(id+"F20.opPattern","COPY",BODY,{"derivedFrom":makeQuery(id+"F19.opPattern","COPY",BODY,{"derivedFrom":makeQuery(id+"F17.opPattern","COPY",BODY,{"derivedFrom":makeQuery(id+"F16.opPattern","COPY",BODY,{"derivedFrom":makeQuery(id+"F14.opExtrude","SWEPT_BODY",BODY,{"disambiguationData":[OSD([sQuery(id+"F13.wireOp",EDGE,"E31.rect.bottom"),sQuery(id+"F13.wireOp",EDGE,"E31.rect.top"),sQuery(id+"F13.wireOp",EDGE,"E31.rect.left"),sQuery(id+"F13.wireOp",EDGE,"E31.rect.right")])]}),"instanceName":"1"}),"instanceName":"1"}),"instanceName":"1"}),"instanceName":"1"}),"instanceName":"1"}),"instanceName":"1"});
            var Q5;
            Q5=makeQuery(id+"F22.opPattern","COPY",BODY,{"derivedFrom":makeQuery(id+"F21.opPattern","COPY",BODY,{"derivedFrom":makeQuery(id+"F20.opPattern","COPY",BODY,{"derivedFrom":makeQuery(id+"F19.opPattern","COPY",BODY,{"derivedFrom":makeQuery(id+"F17.opPattern","COPY",BODY,{"derivedFrom":makeQuery(id+"F14.opExtrude","SWEPT_BODY",BODY,{"disambiguationData":[OSD([sQuery(id+"F13.wireOp",EDGE,"E31.rect.bottom"),sQuery(id+"F13.wireOp",EDGE,"E31.rect.top"),sQuery(id+"F13.wireOp",EDGE,"E31.rect.left"),sQuery(id+"F13.wireOp",EDGE,"E31.rect.right")])]}),"instanceName":"1"}),"instanceName":"1"}),"instanceName":"1"}),"instanceName":"1"}),"instanceName":"1"});
            var Q6;
            Q6=makeQuery(id+"F22.opPattern","COPY",BODY,{"derivedFrom":makeQuery(id+"F21.opPattern","COPY",BODY,{"derivedFrom":makeQuery(id+"F20.opPattern","COPY",BODY,{"derivedFrom":makeQuery(id+"F19.opPattern","COPY",BODY,{"derivedFrom":makeQuery(id+"F16.opPattern","COPY",BODY,{"derivedFrom":makeQuery(id+"F14.opExtrude","SWEPT_BODY",BODY,{"disambiguationData":[OSD([sQuery(id+"F13.wireOp",EDGE,"E31.rect.bottom"),sQuery(id+"F13.wireOp",EDGE,"E31.rect.top"),sQuery(id+"F13.wireOp",EDGE,"E31.rect.left"),sQuery(id+"F13.wireOp",EDGE,"E31.rect.right")])]}),"instanceName":"1"}),"instanceName":"1"}),"instanceName":"1"}),"instanceName":"1"}),"instanceName":"1"});
            var Q7;
            Q7=makeQuery(id+"F22.opPattern","COPY",BODY,{"derivedFrom":makeQuery(id+"F21.opPattern","COPY",BODY,{"derivedFrom":makeQuery(id+"F20.opPattern","COPY",BODY,{"derivedFrom":makeQuery(id+"F19.opPattern","COPY",BODY,{"derivedFrom":makeQuery(id+"F14.opExtrude","SWEPT_BODY",BODY,{"disambiguationData":[OSD([sQuery(id+"F13.wireOp",EDGE,"E31.rect.bottom"),sQuery(id+"F13.wireOp",EDGE,"E31.rect.top"),sQuery(id+"F13.wireOp",EDGE,"E31.rect.left"),sQuery(id+"F13.wireOp",EDGE,"E31.rect.right")])]}),"instanceName":"1"}),"instanceName":"1"}),"instanceName":"1"}),"instanceName":"1"});
            var Q8;
            Q8=makeQuery(id+"F22.opPattern","COPY",BODY,{"derivedFrom":makeQuery(id+"F21.opPattern","COPY",BODY,{"derivedFrom":makeQuery(id+"F20.opPattern","COPY",BODY,{"derivedFrom":makeQuery(id+"F18.opPattern","COPY",BODY,{"derivedFrom":makeQuery(id+"F17.opPattern","COPY",BODY,{"derivedFrom":makeQuery(id+"F16.opPattern","COPY",BODY,{"derivedFrom":makeQuery(id+"F14.opExtrude","SWEPT_BODY",BODY,{"disambiguationData":[OSD([sQuery(id+"F13.wireOp",EDGE,"E31.rect.bottom"),sQuery(id+"F13.wireOp",EDGE,"E31.rect.top"),sQuery(id+"F13.wireOp",EDGE,"E31.rect.left"),sQuery(id+"F13.wireOp",EDGE,"E31.rect.right")])]}),"instanceName":"1"}),"instanceName":"1"}),"instanceName":"1"}),"instanceName":"1"}),"instanceName":"1"}),"instanceName":"1"});
            var Q9;
            Q9=makeQuery(id+"F22.opPattern","COPY",BODY,{"derivedFrom":makeQuery(id+"F21.opPattern","COPY",BODY,{"derivedFrom":makeQuery(id+"F20.opPattern","COPY",BODY,{"derivedFrom":makeQuery(id+"F18.opPattern","COPY",BODY,{"derivedFrom":makeQuery(id+"F17.opPattern","COPY",BODY,{"derivedFrom":makeQuery(id+"F14.opExtrude","SWEPT_BODY",BODY,{"disambiguationData":[OSD([sQuery(id+"F13.wireOp",EDGE,"E31.rect.bottom"),sQuery(id+"F13.wireOp",EDGE,"E31.rect.top"),sQuery(id+"F13.wireOp",EDGE,"E31.rect.left"),sQuery(id+"F13.wireOp",EDGE,"E31.rect.right")])]}),"instanceName":"1"}),"instanceName":"1"}),"instanceName":"1"}),"instanceName":"1"}),"instanceName":"1"});
            var Q10;
            Q10=makeQuery(id+"F22.opPattern","COPY",BODY,{"derivedFrom":makeQuery(id+"F21.opPattern","COPY",BODY,{"derivedFrom":makeQuery(id+"F20.opPattern","COPY",BODY,{"derivedFrom":makeQuery(id+"F18.opPattern","COPY",BODY,{"derivedFrom":makeQuery(id+"F16.opPattern","COPY",BODY,{"derivedFrom":makeQuery(id+"F14.opExtrude","SWEPT_BODY",BODY,{"disambiguationData":[OSD([sQuery(id+"F13.wireOp",EDGE,"E31.rect.bottom"),sQuery(id+"F13.wireOp",EDGE,"E31.rect.top"),sQuery(id+"F13.wireOp",EDGE,"E31.rect.left"),sQuery(id+"F13.wireOp",EDGE,"E31.rect.right")])]}),"instanceName":"1"}),"instanceName":"1"}),"instanceName":"1"}),"instanceName":"1"}),"instanceName":"1"});
            var Q11;
            Q11=makeQuery(id+"F22.opPattern","COPY",BODY,{"derivedFrom":makeQuery(id+"F21.opPattern","COPY",BODY,{"derivedFrom":makeQuery(id+"F20.opPattern","COPY",BODY,{"derivedFrom":makeQuery(id+"F18.opPattern","COPY",BODY,{"derivedFrom":makeQuery(id+"F14.opExtrude","SWEPT_BODY",BODY,{"disambiguationData":[OSD([sQuery(id+"F13.wireOp",EDGE,"E31.rect.bottom"),sQuery(id+"F13.wireOp",EDGE,"E31.rect.top"),sQuery(id+"F13.wireOp",EDGE,"E31.rect.left"),sQuery(id+"F13.wireOp",EDGE,"E31.rect.right")])]}),"instanceName":"1"}),"instanceName":"1"}),"instanceName":"1"}),"instanceName":"1"});
            var Q12;
            Q12=makeQuery(id+"F22.opPattern","COPY",BODY,{"derivedFrom":makeQuery(id+"F21.opPattern","COPY",BODY,{"derivedFrom":makeQuery(id+"F20.opPattern","COPY",BODY,{"derivedFrom":makeQuery(id+"F17.opPattern","COPY",BODY,{"derivedFrom":makeQuery(id+"F16.opPattern","COPY",BODY,{"derivedFrom":makeQuery(id+"F14.opExtrude","SWEPT_BODY",BODY,{"disambiguationData":[OSD([sQuery(id+"F13.wireOp",EDGE,"E31.rect.bottom"),sQuery(id+"F13.wireOp",EDGE,"E31.rect.top"),sQuery(id+"F13.wireOp",EDGE,"E31.rect.left"),sQuery(id+"F13.wireOp",EDGE,"E31.rect.right")])]}),"instanceName":"1"}),"instanceName":"1"}),"instanceName":"1"}),"instanceName":"1"}),"instanceName":"1"});
            var Q13;
            Q13=makeQuery(id+"F22.opPattern","COPY",BODY,{"derivedFrom":makeQuery(id+"F21.opPattern","COPY",BODY,{"derivedFrom":makeQuery(id+"F20.opPattern","COPY",BODY,{"derivedFrom":makeQuery(id+"F17.opPattern","COPY",BODY,{"derivedFrom":makeQuery(id+"F14.opExtrude","SWEPT_BODY",BODY,{"disambiguationData":[OSD([sQuery(id+"F13.wireOp",EDGE,"E31.rect.bottom"),sQuery(id+"F13.wireOp",EDGE,"E31.rect.top"),sQuery(id+"F13.wireOp",EDGE,"E31.rect.left"),sQuery(id+"F13.wireOp",EDGE,"E31.rect.right")])]}),"instanceName":"1"}),"instanceName":"1"}),"instanceName":"1"}),"instanceName":"1"});
            var Q14;
            Q14=makeQuery(id+"F22.opPattern","COPY",BODY,{"derivedFrom":makeQuery(id+"F21.opPattern","COPY",BODY,{"derivedFrom":makeQuery(id+"F20.opPattern","COPY",BODY,{"derivedFrom":makeQuery(id+"F16.opPattern","COPY",BODY,{"derivedFrom":makeQuery(id+"F14.opExtrude","SWEPT_BODY",BODY,{"disambiguationData":[OSD([sQuery(id+"F13.wireOp",EDGE,"E31.rect.bottom"),sQuery(id+"F13.wireOp",EDGE,"E31.rect.top"),sQuery(id+"F13.wireOp",EDGE,"E31.rect.left"),sQuery(id+"F13.wireOp",EDGE,"E31.rect.right")])]}),"instanceName":"1"}),"instanceName":"1"}),"instanceName":"1"}),"instanceName":"1"});
            var Q15;
            Q15=makeQuery(id+"F22.opPattern","COPY",BODY,{"derivedFrom":makeQuery(id+"F21.opPattern","COPY",BODY,{"derivedFrom":makeQuery(id+"F20.opPattern","COPY",BODY,{"derivedFrom":makeQuery(id+"F14.opExtrude","SWEPT_BODY",BODY,{"disambiguationData":[OSD([sQuery(id+"F13.wireOp",EDGE,"E31.rect.bottom"),sQuery(id+"F13.wireOp",EDGE,"E31.rect.top"),sQuery(id+"F13.wireOp",EDGE,"E31.rect.left"),sQuery(id+"F13.wireOp",EDGE,"E31.rect.right")])]}),"instanceName":"1"}),"instanceName":"1"}),"instanceName":"1"});
            var Q16;
            Q16=makeQuery(id+"F5.opExtrude","CAP_EDGE",EDGE,{"disambiguationData":[OSD([sQuery(id+"F4.wireOp",EDGE,"E27.left")])],"isStart":true});
            transform(context, id + "F23", {"entities" : qUnion([Q0, Q1, Q2, Q3, Q4, Q5, Q6, Q7, Q8, Q9, Q10, Q11, Q12, Q13, Q14, Q15]), "transformType" : TransformType.ROTATION, "transformAxis" : qUnion([Q16]), "angle" : 57.6 * degree, "makeCopy" : true});
        }
        {
            var Q0;
            Q0=makeQuery(id+"F23.opPattern","COPY",BODY,{"derivedFrom":makeQuery(id+"F22.opPattern","COPY",BODY,{"derivedFrom":makeQuery(id+"F21.opPattern","COPY",BODY,{"derivedFrom":makeQuery(id+"F20.opPattern","COPY",BODY,{"derivedFrom":makeQuery(id+"F19.opPattern","COPY",BODY,{"derivedFrom":makeQuery(id+"F18.opPattern","COPY",BODY,{"derivedFrom":makeQuery(id+"F17.opPattern","COPY",BODY,{"derivedFrom":makeQuery(id+"F16.opPattern","COPY",BODY,{"derivedFrom":makeQuery(id+"F14.opExtrude","SWEPT_BODY",BODY,{"disambiguationData":[OSD([sQuery(id+"F13.wireOp",EDGE,"E31.rect.bottom"),sQuery(id+"F13.wireOp",EDGE,"E31.rect.top"),sQuery(id+"F13.wireOp",EDGE,"E31.rect.left"),sQuery(id+"F13.wireOp",EDGE,"E31.rect.right")])]}),"instanceName":"1"}),"instanceName":"1"}),"instanceName":"1"}),"instanceName":"1"}),"instanceName":"1"}),"instanceName":"1"}),"instanceName":"1"}),"instanceName":"1"});
            var Q1;
            Q1=makeQuery(id+"F23.opPattern","COPY",BODY,{"derivedFrom":makeQuery(id+"F22.opPattern","COPY",BODY,{"derivedFrom":makeQuery(id+"F21.opPattern","COPY",BODY,{"derivedFrom":makeQuery(id+"F20.opPattern","COPY",BODY,{"derivedFrom":makeQuery(id+"F19.opPattern","COPY",BODY,{"derivedFrom":makeQuery(id+"F18.opPattern","COPY",BODY,{"derivedFrom":makeQuery(id+"F17.opPattern","COPY",BODY,{"derivedFrom":makeQuery(id+"F14.opExtrude","SWEPT_BODY",BODY,{"disambiguationData":[OSD([sQuery(id+"F13.wireOp",EDGE,"E31.rect.bottom"),sQuery(id+"F13.wireOp",EDGE,"E31.rect.top"),sQuery(id+"F13.wireOp",EDGE,"E31.rect.left"),sQuery(id+"F13.wireOp",EDGE,"E31.rect.right")])]}),"instanceName":"1"}),"instanceName":"1"}),"instanceName":"1"}),"instanceName":"1"}),"instanceName":"1"}),"instanceName":"1"}),"instanceName":"1"});
            var Q2;
            Q2=makeQuery(id+"F23.opPattern","COPY",BODY,{"derivedFrom":makeQuery(id+"F22.opPattern","COPY",BODY,{"derivedFrom":makeQuery(id+"F21.opPattern","COPY",BODY,{"derivedFrom":makeQuery(id+"F20.opPattern","COPY",BODY,{"derivedFrom":makeQuery(id+"F19.opPattern","COPY",BODY,{"derivedFrom":makeQuery(id+"F18.opPattern","COPY",BODY,{"derivedFrom":makeQuery(id+"F16.opPattern","COPY",BODY,{"derivedFrom":makeQuery(id+"F14.opExtrude","SWEPT_BODY",BODY,{"disambiguationData":[OSD([sQuery(id+"F13.wireOp",EDGE,"E31.rect.bottom"),sQuery(id+"F13.wireOp",EDGE,"E31.rect.top"),sQuery(id+"F13.wireOp",EDGE,"E31.rect.left"),sQuery(id+"F13.wireOp",EDGE,"E31.rect.right")])]}),"instanceName":"1"}),"instanceName":"1"}),"instanceName":"1"}),"instanceName":"1"}),"instanceName":"1"}),"instanceName":"1"}),"instanceName":"1"});
            var Q3;
            Q3=makeQuery(id+"F23.opPattern","COPY",BODY,{"derivedFrom":makeQuery(id+"F22.opPattern","COPY",BODY,{"derivedFrom":makeQuery(id+"F21.opPattern","COPY",BODY,{"derivedFrom":makeQuery(id+"F20.opPattern","COPY",BODY,{"derivedFrom":makeQuery(id+"F19.opPattern","COPY",BODY,{"derivedFrom":makeQuery(id+"F18.opPattern","COPY",BODY,{"derivedFrom":makeQuery(id+"F14.opExtrude","SWEPT_BODY",BODY,{"disambiguationData":[OSD([sQuery(id+"F13.wireOp",EDGE,"E31.rect.bottom"),sQuery(id+"F13.wireOp",EDGE,"E31.rect.top"),sQuery(id+"F13.wireOp",EDGE,"E31.rect.left"),sQuery(id+"F13.wireOp",EDGE,"E31.rect.right")])]}),"instanceName":"1"}),"instanceName":"1"}),"instanceName":"1"}),"instanceName":"1"}),"instanceName":"1"}),"instanceName":"1"});
            var Q4;
            Q4=makeQuery(id+"F5.opExtrude","CAP_EDGE",EDGE,{"disambiguationData":[OSD([sQuery(id+"F4.wireOp",EDGE,"E27.left")])],"isStart":true});
            transform(context, id + "F24", {"entities" : qUnion([Q0, Q1, Q2, Q3]), "transformType" : TransformType.ROTATION, "transformAxis" : qUnion([Q4]), "angle" : 14.4 * degree, "makeCopy" : true});
        }
        {
            var Q0;
            Q0=makeQuery(id+"F23.opPattern","COPY",BODY,{"derivedFrom":makeQuery(id+"F22.opPattern","COPY",BODY,{"derivedFrom":makeQuery(id+"F21.opPattern","COPY",BODY,{"derivedFrom":makeQuery(id+"F20.opPattern","COPY",BODY,{"derivedFrom":makeQuery(id+"F18.opPattern","COPY",BODY,{"derivedFrom":makeQuery(id+"F14.opExtrude","SWEPT_BODY",BODY,{"disambiguationData":[OSD([sQuery(id+"F13.wireOp",EDGE,"E31.rect.bottom"),sQuery(id+"F13.wireOp",EDGE,"E31.rect.top"),sQuery(id+"F13.wireOp",EDGE,"E31.rect.left"),sQuery(id+"F13.wireOp",EDGE,"E31.rect.right")])]}),"instanceName":"1"}),"instanceName":"1"}),"instanceName":"1"}),"instanceName":"1"}),"instanceName":"1"});
            var Q1;
            Q1=makeQuery(id+"F19.opPattern","COPY",BODY,{"derivedFrom":makeQuery(id+"F18.opPattern","COPY",BODY,{"derivedFrom":makeQuery(id+"F16.opPattern","COPY",BODY,{"derivedFrom":makeQuery(id+"F14.opExtrude","SWEPT_BODY",BODY,{"disambiguationData":[OSD([sQuery(id+"F13.wireOp",EDGE,"E31.rect.bottom"),sQuery(id+"F13.wireOp",EDGE,"E31.rect.top"),sQuery(id+"F13.wireOp",EDGE,"E31.rect.left"),sQuery(id+"F13.wireOp",EDGE,"E31.rect.right")])]}),"instanceName":"1"}),"instanceName":"1"}),"instanceName":"1"});
            var Q2;
            Q2=makeQuery(id+"F23.opPattern","COPY",BODY,{"derivedFrom":makeQuery(id+"F22.opPattern","COPY",BODY,{"derivedFrom":makeQuery(id+"F21.opPattern","COPY",BODY,{"derivedFrom":makeQuery(id+"F20.opPattern","COPY",BODY,{"derivedFrom":makeQuery(id+"F18.opPattern","COPY",BODY,{"derivedFrom":makeQuery(id+"F17.opPattern","COPY",BODY,{"derivedFrom":makeQuery(id+"F16.opPattern","COPY",BODY,{"derivedFrom":makeQuery(id+"F14.opExtrude","SWEPT_BODY",BODY,{"disambiguationData":[OSD([sQuery(id+"F13.wireOp",EDGE,"E31.rect.bottom"),sQuery(id+"F13.wireOp",EDGE,"E31.rect.top"),sQuery(id+"F13.wireOp",EDGE,"E31.rect.left"),sQuery(id+"F13.wireOp",EDGE,"E31.rect.right")])]}),"instanceName":"1"}),"instanceName":"1"}),"instanceName":"1"}),"instanceName":"1"}),"instanceName":"1"}),"instanceName":"1"}),"instanceName":"1"});
            var Q3;
            Q3=makeQuery(id+"F23.opPattern","COPY",BODY,{"derivedFrom":makeQuery(id+"F22.opPattern","COPY",BODY,{"derivedFrom":makeQuery(id+"F21.opPattern","COPY",BODY,{"derivedFrom":makeQuery(id+"F20.opPattern","COPY",BODY,{"derivedFrom":makeQuery(id+"F19.opPattern","COPY",BODY,{"derivedFrom":makeQuery(id+"F18.opPattern","COPY",BODY,{"derivedFrom":makeQuery(id+"F14.opExtrude","SWEPT_BODY",BODY,{"disambiguationData":[OSD([sQuery(id+"F13.wireOp",EDGE,"E31.rect.bottom"),sQuery(id+"F13.wireOp",EDGE,"E31.rect.top"),sQuery(id+"F13.wireOp",EDGE,"E31.rect.left"),sQuery(id+"F13.wireOp",EDGE,"E31.rect.right")])]}),"instanceName":"1"}),"instanceName":"1"}),"instanceName":"1"}),"instanceName":"1"}),"instanceName":"1"}),"instanceName":"1"});
            var Q4;
            Q4=makeQuery(id+"F23.opPattern","COPY",BODY,{"derivedFrom":makeQuery(id+"F22.opPattern","COPY",BODY,{"derivedFrom":makeQuery(id+"F21.opPattern","COPY",BODY,{"derivedFrom":makeQuery(id+"F20.opPattern","COPY",BODY,{"derivedFrom":makeQuery(id+"F17.opPattern","COPY",BODY,{"derivedFrom":makeQuery(id+"F16.opPattern","COPY",BODY,{"derivedFrom":makeQuery(id+"F14.opExtrude","SWEPT_BODY",BODY,{"disambiguationData":[OSD([sQuery(id+"F13.wireOp",EDGE,"E31.rect.bottom"),sQuery(id+"F13.wireOp",EDGE,"E31.rect.top"),sQuery(id+"F13.wireOp",EDGE,"E31.rect.left"),sQuery(id+"F13.wireOp",EDGE,"E31.rect.right")])]}),"instanceName":"1"}),"instanceName":"1"}),"instanceName":"1"}),"instanceName":"1"}),"instanceName":"1"}),"instanceName":"1"});
            var Q5;
            Q5=makeQuery(id+"F23.opPattern","COPY",BODY,{"derivedFrom":makeQuery(id+"F22.opPattern","COPY",BODY,{"derivedFrom":makeQuery(id+"F21.opPattern","COPY",BODY,{"derivedFrom":makeQuery(id+"F20.opPattern","COPY",BODY,{"derivedFrom":makeQuery(id+"F18.opPattern","COPY",BODY,{"derivedFrom":makeQuery(id+"F17.opPattern","COPY",BODY,{"derivedFrom":makeQuery(id+"F14.opExtrude","SWEPT_BODY",BODY,{"disambiguationData":[OSD([sQuery(id+"F13.wireOp",EDGE,"E31.rect.bottom"),sQuery(id+"F13.wireOp",EDGE,"E31.rect.top"),sQuery(id+"F13.wireOp",EDGE,"E31.rect.left"),sQuery(id+"F13.wireOp",EDGE,"E31.rect.right")])]}),"instanceName":"1"}),"instanceName":"1"}),"instanceName":"1"}),"instanceName":"1"}),"instanceName":"1"}),"instanceName":"1"});
            var Q6;
            Q6=makeQuery(id+"F23.opPattern","COPY",BODY,{"derivedFrom":makeQuery(id+"F22.opPattern","COPY",BODY,{"derivedFrom":makeQuery(id+"F21.opPattern","COPY",BODY,{"derivedFrom":makeQuery(id+"F20.opPattern","COPY",BODY,{"derivedFrom":makeQuery(id+"F19.opPattern","COPY",BODY,{"derivedFrom":makeQuery(id+"F18.opPattern","COPY",BODY,{"derivedFrom":makeQuery(id+"F17.opPattern","COPY",BODY,{"derivedFrom":makeQuery(id+"F14.opExtrude","SWEPT_BODY",BODY,{"disambiguationData":[OSD([sQuery(id+"F13.wireOp",EDGE,"E31.rect.bottom"),sQuery(id+"F13.wireOp",EDGE,"E31.rect.top"),sQuery(id+"F13.wireOp",EDGE,"E31.rect.left"),sQuery(id+"F13.wireOp",EDGE,"E31.rect.right")])]}),"instanceName":"1"}),"instanceName":"1"}),"instanceName":"1"}),"instanceName":"1"}),"instanceName":"1"}),"instanceName":"1"}),"instanceName":"1"});
            var Q7;
            Q7=makeQuery(id+"F21.opPattern","COPY",BODY,{"derivedFrom":makeQuery(id+"F17.opPattern","COPY",BODY,{"derivedFrom":makeQuery(id+"F16.opPattern","COPY",BODY,{"derivedFrom":makeQuery(id+"F14.opExtrude","SWEPT_BODY",BODY,{"disambiguationData":[OSD([sQuery(id+"F13.wireOp",EDGE,"E31.rect.bottom"),sQuery(id+"F13.wireOp",EDGE,"E31.rect.top"),sQuery(id+"F13.wireOp",EDGE,"E31.rect.left"),sQuery(id+"F13.wireOp",EDGE,"E31.rect.right")])]}),"instanceName":"1"}),"instanceName":"1"}),"instanceName":"1"});
            var Q8;
            Q8=makeQuery(id+"F23.opPattern","COPY",BODY,{"derivedFrom":makeQuery(id+"F22.opPattern","COPY",BODY,{"derivedFrom":makeQuery(id+"F21.opPattern","COPY",BODY,{"derivedFrom":makeQuery(id+"F20.opPattern","COPY",BODY,{"derivedFrom":makeQuery(id+"F17.opPattern","COPY",BODY,{"derivedFrom":makeQuery(id+"F14.opExtrude","SWEPT_BODY",BODY,{"disambiguationData":[OSD([sQuery(id+"F13.wireOp",EDGE,"E31.rect.bottom"),sQuery(id+"F13.wireOp",EDGE,"E31.rect.top"),sQuery(id+"F13.wireOp",EDGE,"E31.rect.left"),sQuery(id+"F13.wireOp",EDGE,"E31.rect.right")])]}),"instanceName":"1"}),"instanceName":"1"}),"instanceName":"1"}),"instanceName":"1"}),"instanceName":"1"});
            var Q9;
            Q9=makeQuery(id+"F23.opPattern","COPY",BODY,{"derivedFrom":makeQuery(id+"F22.opPattern","COPY",BODY,{"derivedFrom":makeQuery(id+"F21.opPattern","COPY",BODY,{"derivedFrom":makeQuery(id+"F20.opPattern","COPY",BODY,{"derivedFrom":makeQuery(id+"F19.opPattern","COPY",BODY,{"derivedFrom":makeQuery(id+"F17.opPattern","COPY",BODY,{"derivedFrom":makeQuery(id+"F14.opExtrude","SWEPT_BODY",BODY,{"disambiguationData":[OSD([sQuery(id+"F13.wireOp",EDGE,"E31.rect.bottom"),sQuery(id+"F13.wireOp",EDGE,"E31.rect.top"),sQuery(id+"F13.wireOp",EDGE,"E31.rect.left"),sQuery(id+"F13.wireOp",EDGE,"E31.rect.right")])]}),"instanceName":"1"}),"instanceName":"1"}),"instanceName":"1"}),"instanceName":"1"}),"instanceName":"1"}),"instanceName":"1"});
            var Q10;
            Q10=makeQuery(id+"F22.opPattern","COPY",BODY,{"derivedFrom":makeQuery(id+"F21.opPattern","COPY",BODY,{"derivedFrom":makeQuery(id+"F20.opPattern","COPY",BODY,{"derivedFrom":makeQuery(id+"F19.opPattern","COPY",BODY,{"derivedFrom":makeQuery(id+"F16.opPattern","COPY",BODY,{"derivedFrom":makeQuery(id+"F14.opExtrude","SWEPT_BODY",BODY,{"disambiguationData":[OSD([sQuery(id+"F13.wireOp",EDGE,"E31.rect.bottom"),sQuery(id+"F13.wireOp",EDGE,"E31.rect.top"),sQuery(id+"F13.wireOp",EDGE,"E31.rect.left"),sQuery(id+"F13.wireOp",EDGE,"E31.rect.right")])]}),"instanceName":"1"}),"instanceName":"1"}),"instanceName":"1"}),"instanceName":"1"}),"instanceName":"1"});
            var Q11;
            Q11=makeQuery(id+"F23.opPattern","COPY",BODY,{"derivedFrom":makeQuery(id+"F22.opPattern","COPY",BODY,{"derivedFrom":makeQuery(id+"F21.opPattern","COPY",BODY,{"derivedFrom":makeQuery(id+"F20.opPattern","COPY",BODY,{"derivedFrom":makeQuery(id+"F19.opPattern","COPY",BODY,{"derivedFrom":makeQuery(id+"F16.opPattern","COPY",BODY,{"derivedFrom":makeQuery(id+"F14.opExtrude","SWEPT_BODY",BODY,{"disambiguationData":[OSD([sQuery(id+"F13.wireOp",EDGE,"E31.rect.bottom"),sQuery(id+"F13.wireOp",EDGE,"E31.rect.top"),sQuery(id+"F13.wireOp",EDGE,"E31.rect.left"),sQuery(id+"F13.wireOp",EDGE,"E31.rect.right")])]}),"instanceName":"1"}),"instanceName":"1"}),"instanceName":"1"}),"instanceName":"1"}),"instanceName":"1"}),"instanceName":"1"});
            var Q12;
            Q12=makeQuery(id+"F19.opPattern","COPY",BODY,{"derivedFrom":makeQuery(id+"F18.opPattern","COPY",BODY,{"derivedFrom":makeQuery(id+"F17.opPattern","COPY",BODY,{"derivedFrom":makeQuery(id+"F16.opPattern","COPY",BODY,{"derivedFrom":makeQuery(id+"F14.opExtrude","SWEPT_BODY",BODY,{"disambiguationData":[OSD([sQuery(id+"F13.wireOp",EDGE,"E31.rect.bottom"),sQuery(id+"F13.wireOp",EDGE,"E31.rect.top"),sQuery(id+"F13.wireOp",EDGE,"E31.rect.left"),sQuery(id+"F13.wireOp",EDGE,"E31.rect.right")])]}),"instanceName":"1"}),"instanceName":"1"}),"instanceName":"1"}),"instanceName":"1"});
            var Q13;
            Q13=makeQuery(id+"F19.opPattern","COPY",BODY,{"derivedFrom":makeQuery(id+"F18.opPattern","COPY",BODY,{"derivedFrom":makeQuery(id+"F14.opExtrude","SWEPT_BODY",BODY,{"disambiguationData":[OSD([sQuery(id+"F13.wireOp",EDGE,"E31.rect.bottom"),sQuery(id+"F13.wireOp",EDGE,"E31.rect.top"),sQuery(id+"F13.wireOp",EDGE,"E31.rect.left"),sQuery(id+"F13.wireOp",EDGE,"E31.rect.right")])]}),"instanceName":"1"}),"instanceName":"1"});
            var Q14;
            Q14=makeQuery(id+"F18.opPattern","COPY",BODY,{"derivedFrom":makeQuery(id+"F17.opPattern","COPY",BODY,{"derivedFrom":makeQuery(id+"F14.opExtrude","SWEPT_BODY",BODY,{"disambiguationData":[OSD([sQuery(id+"F13.wireOp",EDGE,"E31.rect.bottom"),sQuery(id+"F13.wireOp",EDGE,"E31.rect.top"),sQuery(id+"F13.wireOp",EDGE,"E31.rect.left"),sQuery(id+"F13.wireOp",EDGE,"E31.rect.right")])]}),"instanceName":"1"}),"instanceName":"1"});
            var Q15;
            Q15=makeQuery(id+"F18.opPattern","COPY",BODY,{"derivedFrom":makeQuery(id+"F17.opPattern","COPY",BODY,{"derivedFrom":makeQuery(id+"F16.opPattern","COPY",BODY,{"derivedFrom":makeQuery(id+"F14.opExtrude","SWEPT_BODY",BODY,{"disambiguationData":[OSD([sQuery(id+"F13.wireOp",EDGE,"E31.rect.bottom"),sQuery(id+"F13.wireOp",EDGE,"E31.rect.top"),sQuery(id+"F13.wireOp",EDGE,"E31.rect.left"),sQuery(id+"F13.wireOp",EDGE,"E31.rect.right")])]}),"instanceName":"1"}),"instanceName":"1"}),"instanceName":"1"});
            var Q16;
            Q16=makeQuery(id+"F23.opPattern","COPY",BODY,{"derivedFrom":makeQuery(id+"F22.opPattern","COPY",BODY,{"derivedFrom":makeQuery(id+"F21.opPattern","COPY",BODY,{"derivedFrom":makeQuery(id+"F20.opPattern","COPY",BODY,{"derivedFrom":makeQuery(id+"F19.opPattern","COPY",BODY,{"derivedFrom":makeQuery(id+"F14.opExtrude","SWEPT_BODY",BODY,{"disambiguationData":[OSD([sQuery(id+"F13.wireOp",EDGE,"E31.rect.bottom"),sQuery(id+"F13.wireOp",EDGE,"E31.rect.top"),sQuery(id+"F13.wireOp",EDGE,"E31.rect.left"),sQuery(id+"F13.wireOp",EDGE,"E31.rect.right")])]}),"instanceName":"1"}),"instanceName":"1"}),"instanceName":"1"}),"instanceName":"1"}),"instanceName":"1"});
            var Q17;
            Q17=makeQuery(id+"F23.opPattern","COPY",BODY,{"derivedFrom":makeQuery(id+"F22.opPattern","COPY",BODY,{"derivedFrom":makeQuery(id+"F21.opPattern","COPY",BODY,{"derivedFrom":makeQuery(id+"F20.opPattern","COPY",BODY,{"derivedFrom":makeQuery(id+"F19.opPattern","COPY",BODY,{"derivedFrom":makeQuery(id+"F18.opPattern","COPY",BODY,{"derivedFrom":makeQuery(id+"F16.opPattern","COPY",BODY,{"derivedFrom":makeQuery(id+"F14.opExtrude","SWEPT_BODY",BODY,{"disambiguationData":[OSD([sQuery(id+"F13.wireOp",EDGE,"E31.rect.bottom"),sQuery(id+"F13.wireOp",EDGE,"E31.rect.top"),sQuery(id+"F13.wireOp",EDGE,"E31.rect.left"),sQuery(id+"F13.wireOp",EDGE,"E31.rect.right")])]}),"instanceName":"1"}),"instanceName":"1"}),"instanceName":"1"}),"instanceName":"1"}),"instanceName":"1"}),"instanceName":"1"}),"instanceName":"1"});
            var Q18;
            Q18=makeQuery(id+"F20.opPattern","COPY",BODY,{"derivedFrom":makeQuery(id+"F19.opPattern","COPY",BODY,{"derivedFrom":makeQuery(id+"F17.opPattern","COPY",BODY,{"derivedFrom":makeQuery(id+"F14.opExtrude","SWEPT_BODY",BODY,{"disambiguationData":[OSD([sQuery(id+"F13.wireOp",EDGE,"E31.rect.bottom"),sQuery(id+"F13.wireOp",EDGE,"E31.rect.top"),sQuery(id+"F13.wireOp",EDGE,"E31.rect.left"),sQuery(id+"F13.wireOp",EDGE,"E31.rect.right")])]}),"instanceName":"1"}),"instanceName":"1"}),"instanceName":"1"});
            var Q19;
            Q19=makeQuery(id+"F19.opPattern","COPY",BODY,{"derivedFrom":makeQuery(id+"F17.opPattern","COPY",BODY,{"derivedFrom":makeQuery(id+"F14.opExtrude","SWEPT_BODY",BODY,{"disambiguationData":[OSD([sQuery(id+"F13.wireOp",EDGE,"E31.rect.bottom"),sQuery(id+"F13.wireOp",EDGE,"E31.rect.top"),sQuery(id+"F13.wireOp",EDGE,"E31.rect.left"),sQuery(id+"F13.wireOp",EDGE,"E31.rect.right")])]}),"instanceName":"1"}),"instanceName":"1"});
            var Q20;
            Q20=makeQuery(id+"F20.opPattern","COPY",BODY,{"derivedFrom":makeQuery(id+"F19.opPattern","COPY",BODY,{"derivedFrom":makeQuery(id+"F18.opPattern","COPY",BODY,{"derivedFrom":makeQuery(id+"F16.opPattern","COPY",BODY,{"derivedFrom":makeQuery(id+"F14.opExtrude","SWEPT_BODY",BODY,{"disambiguationData":[OSD([sQuery(id+"F13.wireOp",EDGE,"E31.rect.bottom"),sQuery(id+"F13.wireOp",EDGE,"E31.rect.top"),sQuery(id+"F13.wireOp",EDGE,"E31.rect.left"),sQuery(id+"F13.wireOp",EDGE,"E31.rect.right")])]}),"instanceName":"1"}),"instanceName":"1"}),"instanceName":"1"}),"instanceName":"1"});
            var Q21;
            Q21=makeQuery(id+"F20.opPattern","COPY",BODY,{"derivedFrom":makeQuery(id+"F18.opPattern","COPY",BODY,{"derivedFrom":makeQuery(id+"F17.opPattern","COPY",BODY,{"derivedFrom":makeQuery(id+"F16.opPattern","COPY",BODY,{"derivedFrom":makeQuery(id+"F14.opExtrude","SWEPT_BODY",BODY,{"disambiguationData":[OSD([sQuery(id+"F13.wireOp",EDGE,"E31.rect.bottom"),sQuery(id+"F13.wireOp",EDGE,"E31.rect.top"),sQuery(id+"F13.wireOp",EDGE,"E31.rect.left"),sQuery(id+"F13.wireOp",EDGE,"E31.rect.right")])]}),"instanceName":"1"}),"instanceName":"1"}),"instanceName":"1"}),"instanceName":"1"});
            var Q22;
            Q22=makeQuery(id+"F22.opPattern","COPY",BODY,{"derivedFrom":makeQuery(id+"F21.opPattern","COPY",BODY,{"derivedFrom":makeQuery(id+"F20.opPattern","COPY",BODY,{"derivedFrom":makeQuery(id+"F18.opPattern","COPY",BODY,{"derivedFrom":makeQuery(id+"F17.opPattern","COPY",BODY,{"derivedFrom":makeQuery(id+"F14.opExtrude","SWEPT_BODY",BODY,{"disambiguationData":[OSD([sQuery(id+"F13.wireOp",EDGE,"E31.rect.bottom"),sQuery(id+"F13.wireOp",EDGE,"E31.rect.top"),sQuery(id+"F13.wireOp",EDGE,"E31.rect.left"),sQuery(id+"F13.wireOp",EDGE,"E31.rect.right")])]}),"instanceName":"1"}),"instanceName":"1"}),"instanceName":"1"}),"instanceName":"1"}),"instanceName":"1"});
            var Q23;
            Q23=makeQuery(id+"F20.opPattern","COPY",BODY,{"derivedFrom":makeQuery(id+"F19.opPattern","COPY",BODY,{"derivedFrom":makeQuery(id+"F18.opPattern","COPY",BODY,{"derivedFrom":makeQuery(id+"F17.opPattern","COPY",BODY,{"derivedFrom":makeQuery(id+"F16.opPattern","COPY",BODY,{"derivedFrom":makeQuery(id+"F14.opExtrude","SWEPT_BODY",BODY,{"disambiguationData":[OSD([sQuery(id+"F13.wireOp",EDGE,"E31.rect.bottom"),sQuery(id+"F13.wireOp",EDGE,"E31.rect.top"),sQuery(id+"F13.wireOp",EDGE,"E31.rect.left"),sQuery(id+"F13.wireOp",EDGE,"E31.rect.right")])]}),"instanceName":"1"}),"instanceName":"1"}),"instanceName":"1"}),"instanceName":"1"}),"instanceName":"1"});
            var Q24;
            Q24=makeQuery(id+"F21.opPattern","COPY",BODY,{"derivedFrom":makeQuery(id+"F18.opPattern","COPY",BODY,{"derivedFrom":makeQuery(id+"F17.opPattern","COPY",BODY,{"derivedFrom":makeQuery(id+"F14.opExtrude","SWEPT_BODY",BODY,{"disambiguationData":[OSD([sQuery(id+"F13.wireOp",EDGE,"E31.rect.bottom"),sQuery(id+"F13.wireOp",EDGE,"E31.rect.top"),sQuery(id+"F13.wireOp",EDGE,"E31.rect.left"),sQuery(id+"F13.wireOp",EDGE,"E31.rect.right")])]}),"instanceName":"1"}),"instanceName":"1"}),"instanceName":"1"});
            var Q25;
            Q25=makeQuery(id+"F23.opPattern","COPY",BODY,{"derivedFrom":makeQuery(id+"F22.opPattern","COPY",BODY,{"derivedFrom":makeQuery(id+"F21.opPattern","COPY",BODY,{"derivedFrom":makeQuery(id+"F20.opPattern","COPY",BODY,{"derivedFrom":makeQuery(id+"F18.opPattern","COPY",BODY,{"derivedFrom":makeQuery(id+"F16.opPattern","COPY",BODY,{"derivedFrom":makeQuery(id+"F14.opExtrude","SWEPT_BODY",BODY,{"disambiguationData":[OSD([sQuery(id+"F13.wireOp",EDGE,"E31.rect.bottom"),sQuery(id+"F13.wireOp",EDGE,"E31.rect.top"),sQuery(id+"F13.wireOp",EDGE,"E31.rect.left"),sQuery(id+"F13.wireOp",EDGE,"E31.rect.right")])]}),"instanceName":"1"}),"instanceName":"1"}),"instanceName":"1"}),"instanceName":"1"}),"instanceName":"1"}),"instanceName":"1"});
            var Q26;
            Q26=makeQuery(id+"F22.opPattern","COPY",BODY,{"derivedFrom":makeQuery(id+"F21.opPattern","COPY",BODY,{"derivedFrom":makeQuery(id+"F20.opPattern","COPY",BODY,{"derivedFrom":makeQuery(id+"F19.opPattern","COPY",BODY,{"derivedFrom":makeQuery(id+"F18.opPattern","COPY",BODY,{"derivedFrom":makeQuery(id+"F17.opPattern","COPY",BODY,{"derivedFrom":makeQuery(id+"F14.opExtrude","SWEPT_BODY",BODY,{"disambiguationData":[OSD([sQuery(id+"F13.wireOp",EDGE,"E31.rect.bottom"),sQuery(id+"F13.wireOp",EDGE,"E31.rect.top"),sQuery(id+"F13.wireOp",EDGE,"E31.rect.left"),sQuery(id+"F13.wireOp",EDGE,"E31.rect.right")])]}),"instanceName":"1"}),"instanceName":"1"}),"instanceName":"1"}),"instanceName":"1"}),"instanceName":"1"}),"instanceName":"1"});
            var Q27;
            Q27=makeQuery(id+"F24.opPattern","COPY",BODY,{"derivedFrom":makeQuery(id+"F23.opPattern","COPY",BODY,{"derivedFrom":makeQuery(id+"F22.opPattern","COPY",BODY,{"derivedFrom":makeQuery(id+"F21.opPattern","COPY",BODY,{"derivedFrom":makeQuery(id+"F20.opPattern","COPY",BODY,{"derivedFrom":makeQuery(id+"F19.opPattern","COPY",BODY,{"derivedFrom":makeQuery(id+"F18.opPattern","COPY",BODY,{"derivedFrom":makeQuery(id+"F17.opPattern","COPY",BODY,{"derivedFrom":makeQuery(id+"F14.opExtrude","SWEPT_BODY",BODY,{"disambiguationData":[OSD([sQuery(id+"F13.wireOp",EDGE,"E31.rect.bottom"),sQuery(id+"F13.wireOp",EDGE,"E31.rect.top"),sQuery(id+"F13.wireOp",EDGE,"E31.rect.left"),sQuery(id+"F13.wireOp",EDGE,"E31.rect.right")])]}),"instanceName":"1"}),"instanceName":"1"}),"instanceName":"1"}),"instanceName":"1"}),"instanceName":"1"}),"instanceName":"1"}),"instanceName":"1"}),"instanceName":"1"});
            var Q28;
            Q28=makeQuery(id+"F22.opPattern","COPY",BODY,{"derivedFrom":makeQuery(id+"F21.opPattern","COPY",BODY,{"derivedFrom":makeQuery(id+"F20.opPattern","COPY",BODY,{"derivedFrom":makeQuery(id+"F18.opPattern","COPY",BODY,{"derivedFrom":makeQuery(id+"F14.opExtrude","SWEPT_BODY",BODY,{"disambiguationData":[OSD([sQuery(id+"F13.wireOp",EDGE,"E31.rect.bottom"),sQuery(id+"F13.wireOp",EDGE,"E31.rect.top"),sQuery(id+"F13.wireOp",EDGE,"E31.rect.left"),sQuery(id+"F13.wireOp",EDGE,"E31.rect.right")])]}),"instanceName":"1"}),"instanceName":"1"}),"instanceName":"1"}),"instanceName":"1"});
            var Q29;
            Q29=makeQuery(id+"F20.opPattern","COPY",BODY,{"derivedFrom":makeQuery(id+"F19.opPattern","COPY",BODY,{"derivedFrom":makeQuery(id+"F16.opPattern","COPY",BODY,{"derivedFrom":makeQuery(id+"F14.opExtrude","SWEPT_BODY",BODY,{"disambiguationData":[OSD([sQuery(id+"F13.wireOp",EDGE,"E31.rect.bottom"),sQuery(id+"F13.wireOp",EDGE,"E31.rect.top"),sQuery(id+"F13.wireOp",EDGE,"E31.rect.left"),sQuery(id+"F13.wireOp",EDGE,"E31.rect.right")])]}),"instanceName":"1"}),"instanceName":"1"}),"instanceName":"1"});
            var Q30;
            Q30=makeQuery(id+"F22.opPattern","COPY",BODY,{"derivedFrom":makeQuery(id+"F21.opPattern","COPY",BODY,{"derivedFrom":makeQuery(id+"F20.opPattern","COPY",BODY,{"derivedFrom":makeQuery(id+"F19.opPattern","COPY",BODY,{"derivedFrom":makeQuery(id+"F18.opPattern","COPY",BODY,{"derivedFrom":makeQuery(id+"F14.opExtrude","SWEPT_BODY",BODY,{"disambiguationData":[OSD([sQuery(id+"F13.wireOp",EDGE,"E31.rect.bottom"),sQuery(id+"F13.wireOp",EDGE,"E31.rect.top"),sQuery(id+"F13.wireOp",EDGE,"E31.rect.left"),sQuery(id+"F13.wireOp",EDGE,"E31.rect.right")])]}),"instanceName":"1"}),"instanceName":"1"}),"instanceName":"1"}),"instanceName":"1"}),"instanceName":"1"});
            var Q31;
            Q31=makeQuery(id+"F23.opPattern","COPY",BODY,{"derivedFrom":makeQuery(id+"F22.opPattern","COPY",BODY,{"derivedFrom":makeQuery(id+"F21.opPattern","COPY",BODY,{"derivedFrom":makeQuery(id+"F20.opPattern","COPY",BODY,{"derivedFrom":makeQuery(id+"F19.opPattern","COPY",BODY,{"derivedFrom":makeQuery(id+"F17.opPattern","COPY",BODY,{"derivedFrom":makeQuery(id+"F16.opPattern","COPY",BODY,{"derivedFrom":makeQuery(id+"F14.opExtrude","SWEPT_BODY",BODY,{"disambiguationData":[OSD([sQuery(id+"F13.wireOp",EDGE,"E31.rect.bottom"),sQuery(id+"F13.wireOp",EDGE,"E31.rect.top"),sQuery(id+"F13.wireOp",EDGE,"E31.rect.left"),sQuery(id+"F13.wireOp",EDGE,"E31.rect.right")])]}),"instanceName":"1"}),"instanceName":"1"}),"instanceName":"1"}),"instanceName":"1"}),"instanceName":"1"}),"instanceName":"1"}),"instanceName":"1"});
            var Q32;
            Q32=makeQuery(id+"F22.opPattern","COPY",BODY,{"derivedFrom":makeQuery(id+"F21.opPattern","COPY",BODY,{"derivedFrom":makeQuery(id+"F20.opPattern","COPY",BODY,{"derivedFrom":makeQuery(id+"F17.opPattern","COPY",BODY,{"derivedFrom":makeQuery(id+"F14.opExtrude","SWEPT_BODY",BODY,{"disambiguationData":[OSD([sQuery(id+"F13.wireOp",EDGE,"E31.rect.bottom"),sQuery(id+"F13.wireOp",EDGE,"E31.rect.top"),sQuery(id+"F13.wireOp",EDGE,"E31.rect.left"),sQuery(id+"F13.wireOp",EDGE,"E31.rect.right")])]}),"instanceName":"1"}),"instanceName":"1"}),"instanceName":"1"}),"instanceName":"1"});
            var Q33;
            Q33=makeQuery(id+"F22.opPattern","COPY",BODY,{"derivedFrom":makeQuery(id+"F21.opPattern","COPY",BODY,{"derivedFrom":makeQuery(id+"F20.opPattern","COPY",BODY,{"derivedFrom":makeQuery(id+"F19.opPattern","COPY",BODY,{"derivedFrom":makeQuery(id+"F17.opPattern","COPY",BODY,{"derivedFrom":makeQuery(id+"F14.opExtrude","SWEPT_BODY",BODY,{"disambiguationData":[OSD([sQuery(id+"F13.wireOp",EDGE,"E31.rect.bottom"),sQuery(id+"F13.wireOp",EDGE,"E31.rect.top"),sQuery(id+"F13.wireOp",EDGE,"E31.rect.left"),sQuery(id+"F13.wireOp",EDGE,"E31.rect.right")])]}),"instanceName":"1"}),"instanceName":"1"}),"instanceName":"1"}),"instanceName":"1"}),"instanceName":"1"});
            var Q34;
            Q34=makeQuery(id+"F19.opPattern","COPY",BODY,{"derivedFrom":makeQuery(id+"F16.opPattern","COPY",BODY,{"derivedFrom":makeQuery(id+"F14.opExtrude","SWEPT_BODY",BODY,{"disambiguationData":[OSD([sQuery(id+"F13.wireOp",EDGE,"E31.rect.bottom"),sQuery(id+"F13.wireOp",EDGE,"E31.rect.top"),sQuery(id+"F13.wireOp",EDGE,"E31.rect.left"),sQuery(id+"F13.wireOp",EDGE,"E31.rect.right")])]}),"instanceName":"1"}),"instanceName":"1"});
            var Q35;
            Q35=makeQuery(id+"F21.opPattern","COPY",BODY,{"derivedFrom":makeQuery(id+"F14.opExtrude","SWEPT_BODY",BODY,{"disambiguationData":[OSD([sQuery(id+"F13.wireOp",EDGE,"E31.rect.bottom"),sQuery(id+"F13.wireOp",EDGE,"E31.rect.top"),sQuery(id+"F13.wireOp",EDGE,"E31.rect.left"),sQuery(id+"F13.wireOp",EDGE,"E31.rect.right")])]}),"instanceName":"1"});
            var Q36;
            Q36=makeQuery(id+"F20.opPattern","COPY",BODY,{"derivedFrom":makeQuery(id+"F16.opPattern","COPY",BODY,{"derivedFrom":makeQuery(id+"F14.opExtrude","SWEPT_BODY",BODY,{"disambiguationData":[OSD([sQuery(id+"F13.wireOp",EDGE,"E31.rect.bottom"),sQuery(id+"F13.wireOp",EDGE,"E31.rect.top"),sQuery(id+"F13.wireOp",EDGE,"E31.rect.left"),sQuery(id+"F13.wireOp",EDGE,"E31.rect.right")])]}),"instanceName":"1"}),"instanceName":"1"});
            var Q37;
            Q37=makeQuery(id+"F20.opPattern","COPY",BODY,{"derivedFrom":makeQuery(id+"F17.opPattern","COPY",BODY,{"derivedFrom":makeQuery(id+"F14.opExtrude","SWEPT_BODY",BODY,{"disambiguationData":[OSD([sQuery(id+"F13.wireOp",EDGE,"E31.rect.bottom"),sQuery(id+"F13.wireOp",EDGE,"E31.rect.top"),sQuery(id+"F13.wireOp",EDGE,"E31.rect.left"),sQuery(id+"F13.wireOp",EDGE,"E31.rect.right")])]}),"instanceName":"1"}),"instanceName":"1"});
            var Q38;
            Q38=makeQuery(id+"F22.opPattern","COPY",BODY,{"derivedFrom":makeQuery(id+"F21.opPattern","COPY",BODY,{"derivedFrom":makeQuery(id+"F20.opPattern","COPY",BODY,{"derivedFrom":makeQuery(id+"F14.opExtrude","SWEPT_BODY",BODY,{"disambiguationData":[OSD([sQuery(id+"F13.wireOp",EDGE,"E31.rect.bottom"),sQuery(id+"F13.wireOp",EDGE,"E31.rect.top"),sQuery(id+"F13.wireOp",EDGE,"E31.rect.left"),sQuery(id+"F13.wireOp",EDGE,"E31.rect.right")])]}),"instanceName":"1"}),"instanceName":"1"}),"instanceName":"1"});
            var Q39;
            Q39=makeQuery(id+"F21.opPattern","COPY",BODY,{"derivedFrom":makeQuery(id+"F16.opPattern","COPY",BODY,{"derivedFrom":makeQuery(id+"F14.opExtrude","SWEPT_BODY",BODY,{"disambiguationData":[OSD([sQuery(id+"F13.wireOp",EDGE,"E31.rect.bottom"),sQuery(id+"F13.wireOp",EDGE,"E31.rect.top"),sQuery(id+"F13.wireOp",EDGE,"E31.rect.left"),sQuery(id+"F13.wireOp",EDGE,"E31.rect.right")])]}),"instanceName":"1"}),"instanceName":"1"});
            var Q40;
            Q40=makeQuery(id+"F23.opPattern","COPY",BODY,{"derivedFrom":makeQuery(id+"F22.opPattern","COPY",BODY,{"derivedFrom":makeQuery(id+"F21.opPattern","COPY",BODY,{"derivedFrom":makeQuery(id+"F20.opPattern","COPY",BODY,{"derivedFrom":makeQuery(id+"F16.opPattern","COPY",BODY,{"derivedFrom":makeQuery(id+"F14.opExtrude","SWEPT_BODY",BODY,{"disambiguationData":[OSD([sQuery(id+"F13.wireOp",EDGE,"E31.rect.bottom"),sQuery(id+"F13.wireOp",EDGE,"E31.rect.top"),sQuery(id+"F13.wireOp",EDGE,"E31.rect.left"),sQuery(id+"F13.wireOp",EDGE,"E31.rect.right")])]}),"instanceName":"1"}),"instanceName":"1"}),"instanceName":"1"}),"instanceName":"1"}),"instanceName":"1"});
            var Q41;
            Q41=makeQuery(id+"F21.opPattern","COPY",BODY,{"derivedFrom":makeQuery(id+"F17.opPattern","COPY",BODY,{"derivedFrom":makeQuery(id+"F14.opExtrude","SWEPT_BODY",BODY,{"disambiguationData":[OSD([sQuery(id+"F13.wireOp",EDGE,"E31.rect.bottom"),sQuery(id+"F13.wireOp",EDGE,"E31.rect.top"),sQuery(id+"F13.wireOp",EDGE,"E31.rect.left"),sQuery(id+"F13.wireOp",EDGE,"E31.rect.right")])]}),"instanceName":"1"}),"instanceName":"1"});
            var Q42;
            Q42=makeQuery(id+"F21.opPattern","COPY",BODY,{"derivedFrom":makeQuery(id+"F20.opPattern","COPY",BODY,{"derivedFrom":makeQuery(id+"F14.opExtrude","SWEPT_BODY",BODY,{"disambiguationData":[OSD([sQuery(id+"F13.wireOp",EDGE,"E31.rect.bottom"),sQuery(id+"F13.wireOp",EDGE,"E31.rect.top"),sQuery(id+"F13.wireOp",EDGE,"E31.rect.left"),sQuery(id+"F13.wireOp",EDGE,"E31.rect.right")])]}),"instanceName":"1"}),"instanceName":"1"});
            var Q43;
            Q43=makeQuery(id+"F23.opPattern","COPY",BODY,{"derivedFrom":makeQuery(id+"F22.opPattern","COPY",BODY,{"derivedFrom":makeQuery(id+"F21.opPattern","COPY",BODY,{"derivedFrom":makeQuery(id+"F20.opPattern","COPY",BODY,{"derivedFrom":makeQuery(id+"F14.opExtrude","SWEPT_BODY",BODY,{"disambiguationData":[OSD([sQuery(id+"F13.wireOp",EDGE,"E31.rect.bottom"),sQuery(id+"F13.wireOp",EDGE,"E31.rect.top"),sQuery(id+"F13.wireOp",EDGE,"E31.rect.left"),sQuery(id+"F13.wireOp",EDGE,"E31.rect.right")])]}),"instanceName":"1"}),"instanceName":"1"}),"instanceName":"1"}),"instanceName":"1"});
            var Q44;
            Q44=makeQuery(id+"F22.opPattern","COPY",BODY,{"derivedFrom":makeQuery(id+"F21.opPattern","COPY",BODY,{"derivedFrom":makeQuery(id+"F20.opPattern","COPY",BODY,{"derivedFrom":makeQuery(id+"F16.opPattern","COPY",BODY,{"derivedFrom":makeQuery(id+"F14.opExtrude","SWEPT_BODY",BODY,{"disambiguationData":[OSD([sQuery(id+"F13.wireOp",EDGE,"E31.rect.bottom"),sQuery(id+"F13.wireOp",EDGE,"E31.rect.top"),sQuery(id+"F13.wireOp",EDGE,"E31.rect.left"),sQuery(id+"F13.wireOp",EDGE,"E31.rect.right")])]}),"instanceName":"1"}),"instanceName":"1"}),"instanceName":"1"}),"instanceName":"1"});
            var Q45;
            Q45=makeQuery(id+"F22.opPattern","COPY",BODY,{"derivedFrom":makeQuery(id+"F21.opPattern","COPY",BODY,{"derivedFrom":makeQuery(id+"F20.opPattern","COPY",BODY,{"derivedFrom":makeQuery(id+"F18.opPattern","COPY",BODY,{"derivedFrom":makeQuery(id+"F17.opPattern","COPY",BODY,{"derivedFrom":makeQuery(id+"F16.opPattern","COPY",BODY,{"derivedFrom":makeQuery(id+"F14.opExtrude","SWEPT_BODY",BODY,{"disambiguationData":[OSD([sQuery(id+"F13.wireOp",EDGE,"E31.rect.bottom"),sQuery(id+"F13.wireOp",EDGE,"E31.rect.top"),sQuery(id+"F13.wireOp",EDGE,"E31.rect.left"),sQuery(id+"F13.wireOp",EDGE,"E31.rect.right")])]}),"instanceName":"1"}),"instanceName":"1"}),"instanceName":"1"}),"instanceName":"1"}),"instanceName":"1"}),"instanceName":"1"});
            var Q46;
            Q46=makeQuery(id+"F22.opPattern","COPY",BODY,{"derivedFrom":makeQuery(id+"F21.opPattern","COPY",BODY,{"derivedFrom":makeQuery(id+"F20.opPattern","COPY",BODY,{"derivedFrom":makeQuery(id+"F19.opPattern","COPY",BODY,{"derivedFrom":makeQuery(id+"F18.opPattern","COPY",BODY,{"derivedFrom":makeQuery(id+"F17.opPattern","COPY",BODY,{"derivedFrom":makeQuery(id+"F16.opPattern","COPY",BODY,{"derivedFrom":makeQuery(id+"F14.opExtrude","SWEPT_BODY",BODY,{"disambiguationData":[OSD([sQuery(id+"F13.wireOp",EDGE,"E31.rect.bottom"),sQuery(id+"F13.wireOp",EDGE,"E31.rect.top"),sQuery(id+"F13.wireOp",EDGE,"E31.rect.left"),sQuery(id+"F13.wireOp",EDGE,"E31.rect.right")])]}),"instanceName":"1"}),"instanceName":"1"}),"instanceName":"1"}),"instanceName":"1"}),"instanceName":"1"}),"instanceName":"1"}),"instanceName":"1"});
            var Q47;
            Q47=makeQuery(id+"F21.opPattern","COPY",BODY,{"derivedFrom":makeQuery(id+"F19.opPattern","COPY",BODY,{"derivedFrom":makeQuery(id+"F14.opExtrude","SWEPT_BODY",BODY,{"disambiguationData":[OSD([sQuery(id+"F13.wireOp",EDGE,"E31.rect.bottom"),sQuery(id+"F13.wireOp",EDGE,"E31.rect.top"),sQuery(id+"F13.wireOp",EDGE,"E31.rect.left"),sQuery(id+"F13.wireOp",EDGE,"E31.rect.right")])]}),"instanceName":"1"}),"instanceName":"1"});
            var Q48;
            Q48=makeQuery(id+"F21.opPattern","COPY",BODY,{"derivedFrom":makeQuery(id+"F18.opPattern","COPY",BODY,{"derivedFrom":makeQuery(id+"F14.opExtrude","SWEPT_BODY",BODY,{"disambiguationData":[OSD([sQuery(id+"F13.wireOp",EDGE,"E31.rect.bottom"),sQuery(id+"F13.wireOp",EDGE,"E31.rect.top"),sQuery(id+"F13.wireOp",EDGE,"E31.rect.left"),sQuery(id+"F13.wireOp",EDGE,"E31.rect.right")])]}),"instanceName":"1"}),"instanceName":"1"});
            var Q49;
            Q49=makeQuery(id+"F20.opPattern","COPY",BODY,{"derivedFrom":makeQuery(id+"F17.opPattern","COPY",BODY,{"derivedFrom":makeQuery(id+"F16.opPattern","COPY",BODY,{"derivedFrom":makeQuery(id+"F14.opExtrude","SWEPT_BODY",BODY,{"disambiguationData":[OSD([sQuery(id+"F13.wireOp",EDGE,"E31.rect.bottom"),sQuery(id+"F13.wireOp",EDGE,"E31.rect.top"),sQuery(id+"F13.wireOp",EDGE,"E31.rect.left"),sQuery(id+"F13.wireOp",EDGE,"E31.rect.right")])]}),"instanceName":"1"}),"instanceName":"1"}),"instanceName":"1"});
            var Q50;
            Q50=makeQuery(id+"F21.opPattern","COPY",BODY,{"derivedFrom":makeQuery(id+"F19.opPattern","COPY",BODY,{"derivedFrom":makeQuery(id+"F18.opPattern","COPY",BODY,{"derivedFrom":makeQuery(id+"F14.opExtrude","SWEPT_BODY",BODY,{"disambiguationData":[OSD([sQuery(id+"F13.wireOp",EDGE,"E31.rect.bottom"),sQuery(id+"F13.wireOp",EDGE,"E31.rect.top"),sQuery(id+"F13.wireOp",EDGE,"E31.rect.left"),sQuery(id+"F13.wireOp",EDGE,"E31.rect.right")])]}),"instanceName":"1"}),"instanceName":"1"}),"instanceName":"1"});
            var Q51;
            Q51=makeQuery(id+"F20.opPattern","COPY",BODY,{"derivedFrom":makeQuery(id+"F19.opPattern","COPY",BODY,{"derivedFrom":makeQuery(id+"F18.opPattern","COPY",BODY,{"derivedFrom":makeQuery(id+"F14.opExtrude","SWEPT_BODY",BODY,{"disambiguationData":[OSD([sQuery(id+"F13.wireOp",EDGE,"E31.rect.bottom"),sQuery(id+"F13.wireOp",EDGE,"E31.rect.top"),sQuery(id+"F13.wireOp",EDGE,"E31.rect.left"),sQuery(id+"F13.wireOp",EDGE,"E31.rect.right")])]}),"instanceName":"1"}),"instanceName":"1"}),"instanceName":"1"});
            var Q52;
            Q52=makeQuery(id+"F19.opPattern","COPY",BODY,{"derivedFrom":makeQuery(id+"F17.opPattern","COPY",BODY,{"derivedFrom":makeQuery(id+"F16.opPattern","COPY",BODY,{"derivedFrom":makeQuery(id+"F14.opExtrude","SWEPT_BODY",BODY,{"disambiguationData":[OSD([sQuery(id+"F13.wireOp",EDGE,"E31.rect.bottom"),sQuery(id+"F13.wireOp",EDGE,"E31.rect.top"),sQuery(id+"F13.wireOp",EDGE,"E31.rect.left"),sQuery(id+"F13.wireOp",EDGE,"E31.rect.right")])]}),"instanceName":"1"}),"instanceName":"1"}),"instanceName":"1"});
            var Q53;
            Q53=makeQuery(id+"F20.opPattern","COPY",BODY,{"derivedFrom":makeQuery(id+"F19.opPattern","COPY",BODY,{"derivedFrom":makeQuery(id+"F14.opExtrude","SWEPT_BODY",BODY,{"disambiguationData":[OSD([sQuery(id+"F13.wireOp",EDGE,"E31.rect.bottom"),sQuery(id+"F13.wireOp",EDGE,"E31.rect.top"),sQuery(id+"F13.wireOp",EDGE,"E31.rect.left"),sQuery(id+"F13.wireOp",EDGE,"E31.rect.right")])]}),"instanceName":"1"}),"instanceName":"1"});
            var Q54;
            Q54=makeQuery(id+"F20.opPattern","COPY",BODY,{"derivedFrom":makeQuery(id+"F18.opPattern","COPY",BODY,{"derivedFrom":makeQuery(id+"F16.opPattern","COPY",BODY,{"derivedFrom":makeQuery(id+"F14.opExtrude","SWEPT_BODY",BODY,{"disambiguationData":[OSD([sQuery(id+"F13.wireOp",EDGE,"E31.rect.bottom"),sQuery(id+"F13.wireOp",EDGE,"E31.rect.top"),sQuery(id+"F13.wireOp",EDGE,"E31.rect.left"),sQuery(id+"F13.wireOp",EDGE,"E31.rect.right")])]}),"instanceName":"1"}),"instanceName":"1"}),"instanceName":"1"});
            var Q55;
            Q55=makeQuery(id+"F19.opPattern","COPY",BODY,{"derivedFrom":makeQuery(id+"F18.opPattern","COPY",BODY,{"derivedFrom":makeQuery(id+"F17.opPattern","COPY",BODY,{"derivedFrom":makeQuery(id+"F14.opExtrude","SWEPT_BODY",BODY,{"disambiguationData":[OSD([sQuery(id+"F13.wireOp",EDGE,"E31.rect.bottom"),sQuery(id+"F13.wireOp",EDGE,"E31.rect.top"),sQuery(id+"F13.wireOp",EDGE,"E31.rect.left"),sQuery(id+"F13.wireOp",EDGE,"E31.rect.right")])]}),"instanceName":"1"}),"instanceName":"1"}),"instanceName":"1"});
            var Q56;
            Q56=makeQuery(id+"F20.opPattern","COPY",BODY,{"derivedFrom":makeQuery(id+"F19.opPattern","COPY",BODY,{"derivedFrom":makeQuery(id+"F18.opPattern","COPY",BODY,{"derivedFrom":makeQuery(id+"F17.opPattern","COPY",BODY,{"derivedFrom":makeQuery(id+"F14.opExtrude","SWEPT_BODY",BODY,{"disambiguationData":[OSD([sQuery(id+"F13.wireOp",EDGE,"E31.rect.bottom"),sQuery(id+"F13.wireOp",EDGE,"E31.rect.top"),sQuery(id+"F13.wireOp",EDGE,"E31.rect.left"),sQuery(id+"F13.wireOp",EDGE,"E31.rect.right")])]}),"instanceName":"1"}),"instanceName":"1"}),"instanceName":"1"}),"instanceName":"1"});
            var Q57;
            Q57=makeQuery(id+"F17.opPattern","COPY",BODY,{"derivedFrom":makeQuery(id+"F14.opExtrude","SWEPT_BODY",BODY,{"disambiguationData":[OSD([sQuery(id+"F13.wireOp",EDGE,"E31.rect.bottom"),sQuery(id+"F13.wireOp",EDGE,"E31.rect.top"),sQuery(id+"F13.wireOp",EDGE,"E31.rect.left"),sQuery(id+"F13.wireOp",EDGE,"E31.rect.right")])]}),"instanceName":"1"});
            var Q58;
            Q58=makeQuery(id+"F17.opPattern","COPY",BODY,{"derivedFrom":makeQuery(id+"F16.opPattern","COPY",BODY,{"derivedFrom":makeQuery(id+"F14.opExtrude","SWEPT_BODY",BODY,{"disambiguationData":[OSD([sQuery(id+"F13.wireOp",EDGE,"E31.rect.bottom"),sQuery(id+"F13.wireOp",EDGE,"E31.rect.top"),sQuery(id+"F13.wireOp",EDGE,"E31.rect.left"),sQuery(id+"F13.wireOp",EDGE,"E31.rect.right")])]}),"instanceName":"1"}),"instanceName":"1"});
            var Q59;
            Q59=makeQuery(id+"F18.opPattern","COPY",BODY,{"derivedFrom":makeQuery(id+"F14.opExtrude","SWEPT_BODY",BODY,{"disambiguationData":[OSD([sQuery(id+"F13.wireOp",EDGE,"E31.rect.bottom"),sQuery(id+"F13.wireOp",EDGE,"E31.rect.top"),sQuery(id+"F13.wireOp",EDGE,"E31.rect.left"),sQuery(id+"F13.wireOp",EDGE,"E31.rect.right")])]}),"instanceName":"1"});
            var Q60;
            Q60=makeQuery(id+"F18.opPattern","COPY",BODY,{"derivedFrom":makeQuery(id+"F16.opPattern","COPY",BODY,{"derivedFrom":makeQuery(id+"F14.opExtrude","SWEPT_BODY",BODY,{"disambiguationData":[OSD([sQuery(id+"F13.wireOp",EDGE,"E31.rect.bottom"),sQuery(id+"F13.wireOp",EDGE,"E31.rect.top"),sQuery(id+"F13.wireOp",EDGE,"E31.rect.left"),sQuery(id+"F13.wireOp",EDGE,"E31.rect.right")])]}),"instanceName":"1"}),"instanceName":"1"});
            var Q61;
            Q61=makeQuery(id+"F19.opPattern","COPY",BODY,{"derivedFrom":makeQuery(id+"F14.opExtrude","SWEPT_BODY",BODY,{"disambiguationData":[OSD([sQuery(id+"F13.wireOp",EDGE,"E31.rect.bottom"),sQuery(id+"F13.wireOp",EDGE,"E31.rect.top"),sQuery(id+"F13.wireOp",EDGE,"E31.rect.left"),sQuery(id+"F13.wireOp",EDGE,"E31.rect.right")])]}),"instanceName":"1"});
            var Q62;
            Q62=makeQuery(id+"F20.opPattern","COPY",BODY,{"derivedFrom":makeQuery(id+"F14.opExtrude","SWEPT_BODY",BODY,{"disambiguationData":[OSD([sQuery(id+"F13.wireOp",EDGE,"E31.rect.bottom"),sQuery(id+"F13.wireOp",EDGE,"E31.rect.top"),sQuery(id+"F13.wireOp",EDGE,"E31.rect.left"),sQuery(id+"F13.wireOp",EDGE,"E31.rect.right")])]}),"instanceName":"1"});
            var Q63;
            Q63=makeQuery(id+"F22.opPattern","COPY",BODY,{"derivedFrom":makeQuery(id+"F21.opPattern","COPY",BODY,{"derivedFrom":makeQuery(id+"F20.opPattern","COPY",BODY,{"derivedFrom":makeQuery(id+"F19.opPattern","COPY",BODY,{"derivedFrom":makeQuery(id+"F18.opPattern","COPY",BODY,{"derivedFrom":makeQuery(id+"F16.opPattern","COPY",BODY,{"derivedFrom":makeQuery(id+"F14.opExtrude","SWEPT_BODY",BODY,{"disambiguationData":[OSD([sQuery(id+"F13.wireOp",EDGE,"E31.rect.bottom"),sQuery(id+"F13.wireOp",EDGE,"E31.rect.top"),sQuery(id+"F13.wireOp",EDGE,"E31.rect.left"),sQuery(id+"F13.wireOp",EDGE,"E31.rect.right")])]}),"instanceName":"1"}),"instanceName":"1"}),"instanceName":"1"}),"instanceName":"1"}),"instanceName":"1"}),"instanceName":"1"});
            var Q64;
            Q64=makeQuery(id+"F21.opPattern","COPY",BODY,{"derivedFrom":makeQuery(id+"F20.opPattern","COPY",BODY,{"derivedFrom":makeQuery(id+"F19.opPattern","COPY",BODY,{"derivedFrom":makeQuery(id+"F18.opPattern","COPY",BODY,{"derivedFrom":makeQuery(id+"F17.opPattern","COPY",BODY,{"derivedFrom":makeQuery(id+"F14.opExtrude","SWEPT_BODY",BODY,{"disambiguationData":[OSD([sQuery(id+"F13.wireOp",EDGE,"E31.rect.bottom"),sQuery(id+"F13.wireOp",EDGE,"E31.rect.top"),sQuery(id+"F13.wireOp",EDGE,"E31.rect.left"),sQuery(id+"F13.wireOp",EDGE,"E31.rect.right")])]}),"instanceName":"1"}),"instanceName":"1"}),"instanceName":"1"}),"instanceName":"1"}),"instanceName":"1"});
            var Q65;
            Q65=makeQuery(id+"F21.opPattern","COPY",BODY,{"derivedFrom":makeQuery(id+"F20.opPattern","COPY",BODY,{"derivedFrom":makeQuery(id+"F19.opPattern","COPY",BODY,{"derivedFrom":makeQuery(id+"F14.opExtrude","SWEPT_BODY",BODY,{"disambiguationData":[OSD([sQuery(id+"F13.wireOp",EDGE,"E31.rect.bottom"),sQuery(id+"F13.wireOp",EDGE,"E31.rect.top"),sQuery(id+"F13.wireOp",EDGE,"E31.rect.left"),sQuery(id+"F13.wireOp",EDGE,"E31.rect.right")])]}),"instanceName":"1"}),"instanceName":"1"}),"instanceName":"1"});
            var Q66;
            Q66=makeQuery(id+"F21.opPattern","COPY",BODY,{"derivedFrom":makeQuery(id+"F19.opPattern","COPY",BODY,{"derivedFrom":makeQuery(id+"F18.opPattern","COPY",BODY,{"derivedFrom":makeQuery(id+"F17.opPattern","COPY",BODY,{"derivedFrom":makeQuery(id+"F14.opExtrude","SWEPT_BODY",BODY,{"disambiguationData":[OSD([sQuery(id+"F13.wireOp",EDGE,"E31.rect.bottom"),sQuery(id+"F13.wireOp",EDGE,"E31.rect.top"),sQuery(id+"F13.wireOp",EDGE,"E31.rect.left"),sQuery(id+"F13.wireOp",EDGE,"E31.rect.right")])]}),"instanceName":"1"}),"instanceName":"1"}),"instanceName":"1"}),"instanceName":"1"});
            var Q67;
            Q67=makeQuery(id+"F22.opPattern","COPY",BODY,{"derivedFrom":makeQuery(id+"F21.opPattern","COPY",BODY,{"derivedFrom":makeQuery(id+"F20.opPattern","COPY",BODY,{"derivedFrom":makeQuery(id+"F18.opPattern","COPY",BODY,{"derivedFrom":makeQuery(id+"F16.opPattern","COPY",BODY,{"derivedFrom":makeQuery(id+"F14.opExtrude","SWEPT_BODY",BODY,{"disambiguationData":[OSD([sQuery(id+"F13.wireOp",EDGE,"E31.rect.bottom"),sQuery(id+"F13.wireOp",EDGE,"E31.rect.top"),sQuery(id+"F13.wireOp",EDGE,"E31.rect.left"),sQuery(id+"F13.wireOp",EDGE,"E31.rect.right")])]}),"instanceName":"1"}),"instanceName":"1"}),"instanceName":"1"}),"instanceName":"1"}),"instanceName":"1"});
            var Q68;
            Q68=makeQuery(id+"F21.opPattern","COPY",BODY,{"derivedFrom":makeQuery(id+"F20.opPattern","COPY",BODY,{"derivedFrom":makeQuery(id+"F19.opPattern","COPY",BODY,{"derivedFrom":makeQuery(id+"F18.opPattern","COPY",BODY,{"derivedFrom":makeQuery(id+"F17.opPattern","COPY",BODY,{"derivedFrom":makeQuery(id+"F16.opPattern","COPY",BODY,{"derivedFrom":makeQuery(id+"F14.opExtrude","SWEPT_BODY",BODY,{"disambiguationData":[OSD([sQuery(id+"F13.wireOp",EDGE,"E31.rect.bottom"),sQuery(id+"F13.wireOp",EDGE,"E31.rect.top"),sQuery(id+"F13.wireOp",EDGE,"E31.rect.left"),sQuery(id+"F13.wireOp",EDGE,"E31.rect.right")])]}),"instanceName":"1"}),"instanceName":"1"}),"instanceName":"1"}),"instanceName":"1"}),"instanceName":"1"}),"instanceName":"1"});
            var Q69;
            Q69=makeQuery(id+"F21.opPattern","COPY",BODY,{"derivedFrom":makeQuery(id+"F19.opPattern","COPY",BODY,{"derivedFrom":makeQuery(id+"F16.opPattern","COPY",BODY,{"derivedFrom":makeQuery(id+"F14.opExtrude","SWEPT_BODY",BODY,{"disambiguationData":[OSD([sQuery(id+"F13.wireOp",EDGE,"E31.rect.bottom"),sQuery(id+"F13.wireOp",EDGE,"E31.rect.top"),sQuery(id+"F13.wireOp",EDGE,"E31.rect.left"),sQuery(id+"F13.wireOp",EDGE,"E31.rect.right")])]}),"instanceName":"1"}),"instanceName":"1"}),"instanceName":"1"});
            var Q70;
            Q70=makeQuery(id+"F21.opPattern","COPY",BODY,{"derivedFrom":makeQuery(id+"F20.opPattern","COPY",BODY,{"derivedFrom":makeQuery(id+"F16.opPattern","COPY",BODY,{"derivedFrom":makeQuery(id+"F14.opExtrude","SWEPT_BODY",BODY,{"disambiguationData":[OSD([sQuery(id+"F13.wireOp",EDGE,"E31.rect.bottom"),sQuery(id+"F13.wireOp",EDGE,"E31.rect.top"),sQuery(id+"F13.wireOp",EDGE,"E31.rect.left"),sQuery(id+"F13.wireOp",EDGE,"E31.rect.right")])]}),"instanceName":"1"}),"instanceName":"1"}),"instanceName":"1"});
            var Q71;
            Q71=makeQuery(id+"F22.opPattern","COPY",BODY,{"derivedFrom":makeQuery(id+"F21.opPattern","COPY",BODY,{"derivedFrom":makeQuery(id+"F20.opPattern","COPY",BODY,{"derivedFrom":makeQuery(id+"F19.opPattern","COPY",BODY,{"derivedFrom":makeQuery(id+"F14.opExtrude","SWEPT_BODY",BODY,{"disambiguationData":[OSD([sQuery(id+"F13.wireOp",EDGE,"E31.rect.bottom"),sQuery(id+"F13.wireOp",EDGE,"E31.rect.top"),sQuery(id+"F13.wireOp",EDGE,"E31.rect.left"),sQuery(id+"F13.wireOp",EDGE,"E31.rect.right")])]}),"instanceName":"1"}),"instanceName":"1"}),"instanceName":"1"}),"instanceName":"1"});
            var Q72;
            Q72=makeQuery(id+"F21.opPattern","COPY",BODY,{"derivedFrom":makeQuery(id+"F19.opPattern","COPY",BODY,{"derivedFrom":makeQuery(id+"F17.opPattern","COPY",BODY,{"derivedFrom":makeQuery(id+"F16.opPattern","COPY",BODY,{"derivedFrom":makeQuery(id+"F14.opExtrude","SWEPT_BODY",BODY,{"disambiguationData":[OSD([sQuery(id+"F13.wireOp",EDGE,"E31.rect.bottom"),sQuery(id+"F13.wireOp",EDGE,"E31.rect.top"),sQuery(id+"F13.wireOp",EDGE,"E31.rect.left"),sQuery(id+"F13.wireOp",EDGE,"E31.rect.right")])]}),"instanceName":"1"}),"instanceName":"1"}),"instanceName":"1"}),"instanceName":"1"});
            var Q73;
            Q73=makeQuery(id+"F21.opPattern","COPY",BODY,{"derivedFrom":makeQuery(id+"F20.opPattern","COPY",BODY,{"derivedFrom":makeQuery(id+"F17.opPattern","COPY",BODY,{"derivedFrom":makeQuery(id+"F14.opExtrude","SWEPT_BODY",BODY,{"disambiguationData":[OSD([sQuery(id+"F13.wireOp",EDGE,"E31.rect.bottom"),sQuery(id+"F13.wireOp",EDGE,"E31.rect.top"),sQuery(id+"F13.wireOp",EDGE,"E31.rect.left"),sQuery(id+"F13.wireOp",EDGE,"E31.rect.right")])]}),"instanceName":"1"}),"instanceName":"1"}),"instanceName":"1"});
            var Q74;
            Q74=makeQuery(id+"F21.opPattern","COPY",BODY,{"derivedFrom":makeQuery(id+"F19.opPattern","COPY",BODY,{"derivedFrom":makeQuery(id+"F18.opPattern","COPY",BODY,{"derivedFrom":makeQuery(id+"F16.opPattern","COPY",BODY,{"derivedFrom":makeQuery(id+"F14.opExtrude","SWEPT_BODY",BODY,{"disambiguationData":[OSD([sQuery(id+"F13.wireOp",EDGE,"E31.rect.bottom"),sQuery(id+"F13.wireOp",EDGE,"E31.rect.top"),sQuery(id+"F13.wireOp",EDGE,"E31.rect.left"),sQuery(id+"F13.wireOp",EDGE,"E31.rect.right")])]}),"instanceName":"1"}),"instanceName":"1"}),"instanceName":"1"}),"instanceName":"1"});
            var Q75;
            Q75=makeQuery(id+"F21.opPattern","COPY",BODY,{"derivedFrom":makeQuery(id+"F20.opPattern","COPY",BODY,{"derivedFrom":makeQuery(id+"F19.opPattern","COPY",BODY,{"derivedFrom":makeQuery(id+"F18.opPattern","COPY",BODY,{"derivedFrom":makeQuery(id+"F16.opPattern","COPY",BODY,{"derivedFrom":makeQuery(id+"F14.opExtrude","SWEPT_BODY",BODY,{"disambiguationData":[OSD([sQuery(id+"F13.wireOp",EDGE,"E31.rect.bottom"),sQuery(id+"F13.wireOp",EDGE,"E31.rect.top"),sQuery(id+"F13.wireOp",EDGE,"E31.rect.left"),sQuery(id+"F13.wireOp",EDGE,"E31.rect.right")])]}),"instanceName":"1"}),"instanceName":"1"}),"instanceName":"1"}),"instanceName":"1"}),"instanceName":"1"});
            var Q76;
            Q76=makeQuery(id+"F20.opPattern","COPY",BODY,{"derivedFrom":makeQuery(id+"F18.opPattern","COPY",BODY,{"derivedFrom":makeQuery(id+"F17.opPattern","COPY",BODY,{"derivedFrom":makeQuery(id+"F14.opExtrude","SWEPT_BODY",BODY,{"disambiguationData":[OSD([sQuery(id+"F13.wireOp",EDGE,"E31.rect.bottom"),sQuery(id+"F13.wireOp",EDGE,"E31.rect.top"),sQuery(id+"F13.wireOp",EDGE,"E31.rect.left"),sQuery(id+"F13.wireOp",EDGE,"E31.rect.right")])]}),"instanceName":"1"}),"instanceName":"1"}),"instanceName":"1"});
            var Q77;
            Q77=makeQuery(id+"F20.opPattern","COPY",BODY,{"derivedFrom":makeQuery(id+"F19.opPattern","COPY",BODY,{"derivedFrom":makeQuery(id+"F17.opPattern","COPY",BODY,{"derivedFrom":makeQuery(id+"F16.opPattern","COPY",BODY,{"derivedFrom":makeQuery(id+"F14.opExtrude","SWEPT_BODY",BODY,{"disambiguationData":[OSD([sQuery(id+"F13.wireOp",EDGE,"E31.rect.bottom"),sQuery(id+"F13.wireOp",EDGE,"E31.rect.top"),sQuery(id+"F13.wireOp",EDGE,"E31.rect.left"),sQuery(id+"F13.wireOp",EDGE,"E31.rect.right")])]}),"instanceName":"1"}),"instanceName":"1"}),"instanceName":"1"}),"instanceName":"1"});
            var Q78;
            Q78=makeQuery(id+"F21.opPattern","COPY",BODY,{"derivedFrom":makeQuery(id+"F19.opPattern","COPY",BODY,{"derivedFrom":makeQuery(id+"F17.opPattern","COPY",BODY,{"derivedFrom":makeQuery(id+"F14.opExtrude","SWEPT_BODY",BODY,{"disambiguationData":[OSD([sQuery(id+"F13.wireOp",EDGE,"E31.rect.bottom"),sQuery(id+"F13.wireOp",EDGE,"E31.rect.top"),sQuery(id+"F13.wireOp",EDGE,"E31.rect.left"),sQuery(id+"F13.wireOp",EDGE,"E31.rect.right")])]}),"instanceName":"1"}),"instanceName":"1"}),"instanceName":"1"});
            var Q79;
            Q79=makeQuery(id+"F21.opPattern","COPY",BODY,{"derivedFrom":makeQuery(id+"F18.opPattern","COPY",BODY,{"derivedFrom":makeQuery(id+"F17.opPattern","COPY",BODY,{"derivedFrom":makeQuery(id+"F16.opPattern","COPY",BODY,{"derivedFrom":makeQuery(id+"F14.opExtrude","SWEPT_BODY",BODY,{"disambiguationData":[OSD([sQuery(id+"F13.wireOp",EDGE,"E31.rect.bottom"),sQuery(id+"F13.wireOp",EDGE,"E31.rect.top"),sQuery(id+"F13.wireOp",EDGE,"E31.rect.left"),sQuery(id+"F13.wireOp",EDGE,"E31.rect.right")])]}),"instanceName":"1"}),"instanceName":"1"}),"instanceName":"1"}),"instanceName":"1"});
            var Q80;
            Q80=makeQuery(id+"F21.opPattern","COPY",BODY,{"derivedFrom":makeQuery(id+"F20.opPattern","COPY",BODY,{"derivedFrom":makeQuery(id+"F18.opPattern","COPY",BODY,{"derivedFrom":makeQuery(id+"F16.opPattern","COPY",BODY,{"derivedFrom":makeQuery(id+"F14.opExtrude","SWEPT_BODY",BODY,{"disambiguationData":[OSD([sQuery(id+"F13.wireOp",EDGE,"E31.rect.bottom"),sQuery(id+"F13.wireOp",EDGE,"E31.rect.top"),sQuery(id+"F13.wireOp",EDGE,"E31.rect.left"),sQuery(id+"F13.wireOp",EDGE,"E31.rect.right")])]}),"instanceName":"1"}),"instanceName":"1"}),"instanceName":"1"}),"instanceName":"1"});
            var Q81;
            Q81=makeQuery(id+"F21.opPattern","COPY",BODY,{"derivedFrom":makeQuery(id+"F20.opPattern","COPY",BODY,{"derivedFrom":makeQuery(id+"F19.opPattern","COPY",BODY,{"derivedFrom":makeQuery(id+"F17.opPattern","COPY",BODY,{"derivedFrom":makeQuery(id+"F14.opExtrude","SWEPT_BODY",BODY,{"disambiguationData":[OSD([sQuery(id+"F13.wireOp",EDGE,"E31.rect.bottom"),sQuery(id+"F13.wireOp",EDGE,"E31.rect.top"),sQuery(id+"F13.wireOp",EDGE,"E31.rect.left"),sQuery(id+"F13.wireOp",EDGE,"E31.rect.right")])]}),"instanceName":"1"}),"instanceName":"1"}),"instanceName":"1"}),"instanceName":"1"});
            var Q82;
            Q82=makeQuery(id+"F24.opPattern","COPY",BODY,{"derivedFrom":makeQuery(id+"F23.opPattern","COPY",BODY,{"derivedFrom":makeQuery(id+"F22.opPattern","COPY",BODY,{"derivedFrom":makeQuery(id+"F21.opPattern","COPY",BODY,{"derivedFrom":makeQuery(id+"F20.opPattern","COPY",BODY,{"derivedFrom":makeQuery(id+"F19.opPattern","COPY",BODY,{"derivedFrom":makeQuery(id+"F18.opPattern","COPY",BODY,{"derivedFrom":makeQuery(id+"F14.opExtrude","SWEPT_BODY",BODY,{"disambiguationData":[OSD([sQuery(id+"F13.wireOp",EDGE,"E31.rect.bottom"),sQuery(id+"F13.wireOp",EDGE,"E31.rect.top"),sQuery(id+"F13.wireOp",EDGE,"E31.rect.left"),sQuery(id+"F13.wireOp",EDGE,"E31.rect.right")])]}),"instanceName":"1"}),"instanceName":"1"}),"instanceName":"1"}),"instanceName":"1"}),"instanceName":"1"}),"instanceName":"1"}),"instanceName":"1"});
            var Q83;
            Q83=makeQuery(id+"F20.opPattern","COPY",BODY,{"derivedFrom":makeQuery(id+"F18.opPattern","COPY",BODY,{"derivedFrom":makeQuery(id+"F14.opExtrude","SWEPT_BODY",BODY,{"disambiguationData":[OSD([sQuery(id+"F13.wireOp",EDGE,"E31.rect.bottom"),sQuery(id+"F13.wireOp",EDGE,"E31.rect.top"),sQuery(id+"F13.wireOp",EDGE,"E31.rect.left"),sQuery(id+"F13.wireOp",EDGE,"E31.rect.right")])]}),"instanceName":"1"}),"instanceName":"1"});
            var Q84;
            Q84=makeQuery(id+"F21.opPattern","COPY",BODY,{"derivedFrom":makeQuery(id+"F18.opPattern","COPY",BODY,{"derivedFrom":makeQuery(id+"F16.opPattern","COPY",BODY,{"derivedFrom":makeQuery(id+"F14.opExtrude","SWEPT_BODY",BODY,{"disambiguationData":[OSD([sQuery(id+"F13.wireOp",EDGE,"E31.rect.bottom"),sQuery(id+"F13.wireOp",EDGE,"E31.rect.top"),sQuery(id+"F13.wireOp",EDGE,"E31.rect.left"),sQuery(id+"F13.wireOp",EDGE,"E31.rect.right")])]}),"instanceName":"1"}),"instanceName":"1"}),"instanceName":"1"});
            var Q85;
            Q85=makeQuery(id+"F21.opPattern","COPY",BODY,{"derivedFrom":makeQuery(id+"F19.opPattern","COPY",BODY,{"derivedFrom":makeQuery(id+"F18.opPattern","COPY",BODY,{"derivedFrom":makeQuery(id+"F17.opPattern","COPY",BODY,{"derivedFrom":makeQuery(id+"F16.opPattern","COPY",BODY,{"derivedFrom":makeQuery(id+"F14.opExtrude","SWEPT_BODY",BODY,{"disambiguationData":[OSD([sQuery(id+"F13.wireOp",EDGE,"E31.rect.bottom"),sQuery(id+"F13.wireOp",EDGE,"E31.rect.top"),sQuery(id+"F13.wireOp",EDGE,"E31.rect.left"),sQuery(id+"F13.wireOp",EDGE,"E31.rect.right")])]}),"instanceName":"1"}),"instanceName":"1"}),"instanceName":"1"}),"instanceName":"1"}),"instanceName":"1"});
            var Q86;
            Q86=makeQuery(id+"F21.opPattern","COPY",BODY,{"derivedFrom":makeQuery(id+"F20.opPattern","COPY",BODY,{"derivedFrom":makeQuery(id+"F17.opPattern","COPY",BODY,{"derivedFrom":makeQuery(id+"F16.opPattern","COPY",BODY,{"derivedFrom":makeQuery(id+"F14.opExtrude","SWEPT_BODY",BODY,{"disambiguationData":[OSD([sQuery(id+"F13.wireOp",EDGE,"E31.rect.bottom"),sQuery(id+"F13.wireOp",EDGE,"E31.rect.top"),sQuery(id+"F13.wireOp",EDGE,"E31.rect.left"),sQuery(id+"F13.wireOp",EDGE,"E31.rect.right")])]}),"instanceName":"1"}),"instanceName":"1"}),"instanceName":"1"}),"instanceName":"1"});
            var Q87;
            Q87=makeQuery(id+"F23.opPattern","COPY",BODY,{"derivedFrom":makeQuery(id+"F22.opPattern","COPY",BODY,{"derivedFrom":makeQuery(id+"F21.opPattern","COPY",BODY,{"derivedFrom":makeQuery(id+"F20.opPattern","COPY",BODY,{"derivedFrom":makeQuery(id+"F19.opPattern","COPY",BODY,{"derivedFrom":makeQuery(id+"F18.opPattern","COPY",BODY,{"derivedFrom":makeQuery(id+"F17.opPattern","COPY",BODY,{"derivedFrom":makeQuery(id+"F16.opPattern","COPY",BODY,{"derivedFrom":makeQuery(id+"F14.opExtrude","SWEPT_BODY",BODY,{"disambiguationData":[OSD([sQuery(id+"F13.wireOp",EDGE,"E31.rect.bottom"),sQuery(id+"F13.wireOp",EDGE,"E31.rect.top"),sQuery(id+"F13.wireOp",EDGE,"E31.rect.left"),sQuery(id+"F13.wireOp",EDGE,"E31.rect.right")])]}),"instanceName":"1"}),"instanceName":"1"}),"instanceName":"1"}),"instanceName":"1"}),"instanceName":"1"}),"instanceName":"1"}),"instanceName":"1"}),"instanceName":"1"});
            var Q88;
            Q88=makeQuery(id+"F21.opPattern","COPY",BODY,{"derivedFrom":makeQuery(id+"F20.opPattern","COPY",BODY,{"derivedFrom":makeQuery(id+"F18.opPattern","COPY",BODY,{"derivedFrom":makeQuery(id+"F14.opExtrude","SWEPT_BODY",BODY,{"disambiguationData":[OSD([sQuery(id+"F13.wireOp",EDGE,"E31.rect.bottom"),sQuery(id+"F13.wireOp",EDGE,"E31.rect.top"),sQuery(id+"F13.wireOp",EDGE,"E31.rect.left"),sQuery(id+"F13.wireOp",EDGE,"E31.rect.right")])]}),"instanceName":"1"}),"instanceName":"1"}),"instanceName":"1"});
            var Q89;
            Q89=makeQuery(id+"F21.opPattern","COPY",BODY,{"derivedFrom":makeQuery(id+"F20.opPattern","COPY",BODY,{"derivedFrom":makeQuery(id+"F19.opPattern","COPY",BODY,{"derivedFrom":makeQuery(id+"F17.opPattern","COPY",BODY,{"derivedFrom":makeQuery(id+"F16.opPattern","COPY",BODY,{"derivedFrom":makeQuery(id+"F14.opExtrude","SWEPT_BODY",BODY,{"disambiguationData":[OSD([sQuery(id+"F13.wireOp",EDGE,"E31.rect.bottom"),sQuery(id+"F13.wireOp",EDGE,"E31.rect.top"),sQuery(id+"F13.wireOp",EDGE,"E31.rect.left"),sQuery(id+"F13.wireOp",EDGE,"E31.rect.right")])]}),"instanceName":"1"}),"instanceName":"1"}),"instanceName":"1"}),"instanceName":"1"}),"instanceName":"1"});
            var Q90;
            Q90=makeQuery(id+"F22.opPattern","COPY",BODY,{"derivedFrom":makeQuery(id+"F21.opPattern","COPY",BODY,{"derivedFrom":makeQuery(id+"F20.opPattern","COPY",BODY,{"derivedFrom":makeQuery(id+"F17.opPattern","COPY",BODY,{"derivedFrom":makeQuery(id+"F16.opPattern","COPY",BODY,{"derivedFrom":makeQuery(id+"F14.opExtrude","SWEPT_BODY",BODY,{"disambiguationData":[OSD([sQuery(id+"F13.wireOp",EDGE,"E31.rect.bottom"),sQuery(id+"F13.wireOp",EDGE,"E31.rect.top"),sQuery(id+"F13.wireOp",EDGE,"E31.rect.left"),sQuery(id+"F13.wireOp",EDGE,"E31.rect.right")])]}),"instanceName":"1"}),"instanceName":"1"}),"instanceName":"1"}),"instanceName":"1"}),"instanceName":"1"});
            var Q91;
            Q91=makeQuery(id+"F21.opPattern","COPY",BODY,{"derivedFrom":makeQuery(id+"F20.opPattern","COPY",BODY,{"derivedFrom":makeQuery(id+"F19.opPattern","COPY",BODY,{"derivedFrom":makeQuery(id+"F18.opPattern","COPY",BODY,{"derivedFrom":makeQuery(id+"F14.opExtrude","SWEPT_BODY",BODY,{"disambiguationData":[OSD([sQuery(id+"F13.wireOp",EDGE,"E31.rect.bottom"),sQuery(id+"F13.wireOp",EDGE,"E31.rect.top"),sQuery(id+"F13.wireOp",EDGE,"E31.rect.left"),sQuery(id+"F13.wireOp",EDGE,"E31.rect.right")])]}),"instanceName":"1"}),"instanceName":"1"}),"instanceName":"1"}),"instanceName":"1"});
            var Q92;
            Q92=makeQuery(id+"F24.opPattern","COPY",BODY,{"derivedFrom":makeQuery(id+"F23.opPattern","COPY",BODY,{"derivedFrom":makeQuery(id+"F22.opPattern","COPY",BODY,{"derivedFrom":makeQuery(id+"F21.opPattern","COPY",BODY,{"derivedFrom":makeQuery(id+"F20.opPattern","COPY",BODY,{"derivedFrom":makeQuery(id+"F19.opPattern","COPY",BODY,{"derivedFrom":makeQuery(id+"F18.opPattern","COPY",BODY,{"derivedFrom":makeQuery(id+"F16.opPattern","COPY",BODY,{"derivedFrom":makeQuery(id+"F14.opExtrude","SWEPT_BODY",BODY,{"disambiguationData":[OSD([sQuery(id+"F13.wireOp",EDGE,"E31.rect.bottom"),sQuery(id+"F13.wireOp",EDGE,"E31.rect.top"),sQuery(id+"F13.wireOp",EDGE,"E31.rect.left"),sQuery(id+"F13.wireOp",EDGE,"E31.rect.right")])]}),"instanceName":"1"}),"instanceName":"1"}),"instanceName":"1"}),"instanceName":"1"}),"instanceName":"1"}),"instanceName":"1"}),"instanceName":"1"}),"instanceName":"1"});
            var Q93;
            Q93=makeQuery(id+"F21.opPattern","COPY",BODY,{"derivedFrom":makeQuery(id+"F20.opPattern","COPY",BODY,{"derivedFrom":makeQuery(id+"F19.opPattern","COPY",BODY,{"derivedFrom":makeQuery(id+"F16.opPattern","COPY",BODY,{"derivedFrom":makeQuery(id+"F14.opExtrude","SWEPT_BODY",BODY,{"disambiguationData":[OSD([sQuery(id+"F13.wireOp",EDGE,"E31.rect.bottom"),sQuery(id+"F13.wireOp",EDGE,"E31.rect.top"),sQuery(id+"F13.wireOp",EDGE,"E31.rect.left"),sQuery(id+"F13.wireOp",EDGE,"E31.rect.right")])]}),"instanceName":"1"}),"instanceName":"1"}),"instanceName":"1"}),"instanceName":"1"});
            var Q94;
            Q94=makeQuery(id+"F21.opPattern","COPY",BODY,{"derivedFrom":makeQuery(id+"F20.opPattern","COPY",BODY,{"derivedFrom":makeQuery(id+"F18.opPattern","COPY",BODY,{"derivedFrom":makeQuery(id+"F17.opPattern","COPY",BODY,{"derivedFrom":makeQuery(id+"F16.opPattern","COPY",BODY,{"derivedFrom":makeQuery(id+"F14.opExtrude","SWEPT_BODY",BODY,{"disambiguationData":[OSD([sQuery(id+"F13.wireOp",EDGE,"E31.rect.bottom"),sQuery(id+"F13.wireOp",EDGE,"E31.rect.top"),sQuery(id+"F13.wireOp",EDGE,"E31.rect.left"),sQuery(id+"F13.wireOp",EDGE,"E31.rect.right")])]}),"instanceName":"1"}),"instanceName":"1"}),"instanceName":"1"}),"instanceName":"1"}),"instanceName":"1"});
            var Q95;
            Q95=makeQuery(id+"F22.opPattern","COPY",BODY,{"derivedFrom":makeQuery(id+"F21.opPattern","COPY",BODY,{"derivedFrom":makeQuery(id+"F20.opPattern","COPY",BODY,{"derivedFrom":makeQuery(id+"F19.opPattern","COPY",BODY,{"derivedFrom":makeQuery(id+"F17.opPattern","COPY",BODY,{"derivedFrom":makeQuery(id+"F16.opPattern","COPY",BODY,{"derivedFrom":makeQuery(id+"F14.opExtrude","SWEPT_BODY",BODY,{"disambiguationData":[OSD([sQuery(id+"F13.wireOp",EDGE,"E31.rect.bottom"),sQuery(id+"F13.wireOp",EDGE,"E31.rect.top"),sQuery(id+"F13.wireOp",EDGE,"E31.rect.left"),sQuery(id+"F13.wireOp",EDGE,"E31.rect.right")])]}),"instanceName":"1"}),"instanceName":"1"}),"instanceName":"1"}),"instanceName":"1"}),"instanceName":"1"}),"instanceName":"1"});
            var Q96;
            Q96=makeQuery(id+"F16.opPattern","COPY",BODY,{"derivedFrom":makeQuery(id+"F14.opExtrude","SWEPT_BODY",BODY,{"disambiguationData":[OSD([sQuery(id+"F13.wireOp",EDGE,"E31.rect.bottom"),sQuery(id+"F13.wireOp",EDGE,"E31.rect.top"),sQuery(id+"F13.wireOp",EDGE,"E31.rect.left"),sQuery(id+"F13.wireOp",EDGE,"E31.rect.right")])]}),"instanceName":"1"});
            var Q97;
            Q97=makeQuery(id+"F14.opExtrude","SWEPT_BODY",BODY,{"disambiguationData":[OSD([sQuery(id+"F13.wireOp",EDGE,"E31.rect.bottom"),sQuery(id+"F13.wireOp",EDGE,"E31.rect.top"),sQuery(id+"F13.wireOp",EDGE,"E31.rect.left"),sQuery(id+"F13.wireOp",EDGE,"E31.rect.right")])]});
            var Q98;
            Q98=makeQuery(id+"F24.opPattern","COPY",BODY,{"derivedFrom":makeQuery(id+"F23.opPattern","COPY",BODY,{"derivedFrom":makeQuery(id+"F22.opPattern","COPY",BODY,{"derivedFrom":makeQuery(id+"F21.opPattern","COPY",BODY,{"derivedFrom":makeQuery(id+"F20.opPattern","COPY",BODY,{"derivedFrom":makeQuery(id+"F19.opPattern","COPY",BODY,{"derivedFrom":makeQuery(id+"F18.opPattern","COPY",BODY,{"derivedFrom":makeQuery(id+"F17.opPattern","COPY",BODY,{"derivedFrom":makeQuery(id+"F16.opPattern","COPY",BODY,{"derivedFrom":makeQuery(id+"F14.opExtrude","SWEPT_BODY",BODY,{"disambiguationData":[OSD([sQuery(id+"F13.wireOp",EDGE,"E31.rect.bottom"),sQuery(id+"F13.wireOp",EDGE,"E31.rect.top"),sQuery(id+"F13.wireOp",EDGE,"E31.rect.left"),sQuery(id+"F13.wireOp",EDGE,"E31.rect.right")])]}),"instanceName":"1"}),"instanceName":"1"}),"instanceName":"1"}),"instanceName":"1"}),"instanceName":"1"}),"instanceName":"1"}),"instanceName":"1"}),"instanceName":"1"}),"instanceName":"1"});
            var Q99;
            Q99=makeQuery(id+"F21.opPattern","COPY",BODY,{"derivedFrom":makeQuery(id+"F20.opPattern","COPY",BODY,{"derivedFrom":makeQuery(id+"F18.opPattern","COPY",BODY,{"derivedFrom":makeQuery(id+"F17.opPattern","COPY",BODY,{"derivedFrom":makeQuery(id+"F14.opExtrude","SWEPT_BODY",BODY,{"disambiguationData":[OSD([sQuery(id+"F13.wireOp",EDGE,"E31.rect.bottom"),sQuery(id+"F13.wireOp",EDGE,"E31.rect.top"),sQuery(id+"F13.wireOp",EDGE,"E31.rect.left"),sQuery(id+"F13.wireOp",EDGE,"E31.rect.right")])]}),"instanceName":"1"}),"instanceName":"1"}),"instanceName":"1"}),"instanceName":"1"});
            var Q100;
            Q100=makeQuery(id+"F1.opRevolve","SWEPT_BODY",BODY,{"disambiguationData":[OSD([sQuery(id+"F0.wireOp",EDGE,"E2"),sQuery(id+"F0.wireOp",EDGE,"E3"),sQuery(id+"F0.wireOp",EDGE,"E4"),sQuery(id+"F0.wireOp",EDGE,"E10"),sQuery(id+"F0.wireOp",EDGE,"E12"),sQuery(id+"F0.wireOp",EDGE,"E14"),sQuery(id+"F0.wireOp",EDGE,"E15"),sQuery(id+"F0.wireOp",EDGE,"E16"),sQuery(id+"F0.wireOp",EDGE,"E18"),sQuery(id+"F0.wireOp",EDGE,"E19"),sQuery(id+"F0.wireOp",EDGE,"E20")])]});
            booleanBodies(context, id + "F25", {"operationType" : BooleanOperationType.SUBTRACTION, "tools" : qUnion([Q0, Q1, Q2, Q3, Q4, Q5, Q6, Q7, Q8, Q9, Q10, Q11, Q12, Q13, Q14, Q15, Q16, Q17, Q18, Q19, Q20, Q21, Q22, Q23, Q24, Q25, Q26, Q27, Q28, Q29, Q30, Q31, Q32, Q33, Q34, Q35, Q36, Q37, Q38, Q39, Q40, Q41, Q42, Q43, Q44, Q45, Q46, Q47, Q48, Q49, Q50, Q51, Q52, Q53, Q54, Q55, Q56, Q57, Q58, Q59, Q60, Q61, Q62, Q63, Q64, Q65, Q66, Q67, Q68, Q69, Q70, Q71, Q72, Q73, Q74, Q75, Q76, Q77, Q78, Q79, Q80, Q81, Q82, Q83, Q84, Q85, Q86, Q87, Q88, Q89, Q90, Q91, Q92, Q93, Q94, Q95, Q96, Q97, Q98, Q99]), "targets" : qUnion([Q100])});
        }
        {
            var Q0;
            Q0=makeQuery(id+"F5.opExtrude","SWEPT_BODY",BODY,{"disambiguationData":[OSD([sQuery(id+"F4.wireOp",EDGE,"E27.bottom"),sQuery(id+"F4.wireOp",EDGE,"E27.top"),sQuery(id+"F4.wireOp",EDGE,"E27.left"),sQuery(id+"F4.wireOp",EDGE,"E27.right")])]});
            deleteBodies(context, id + "F26", {"entities" : qUnion([Q0])});
        }
    });
